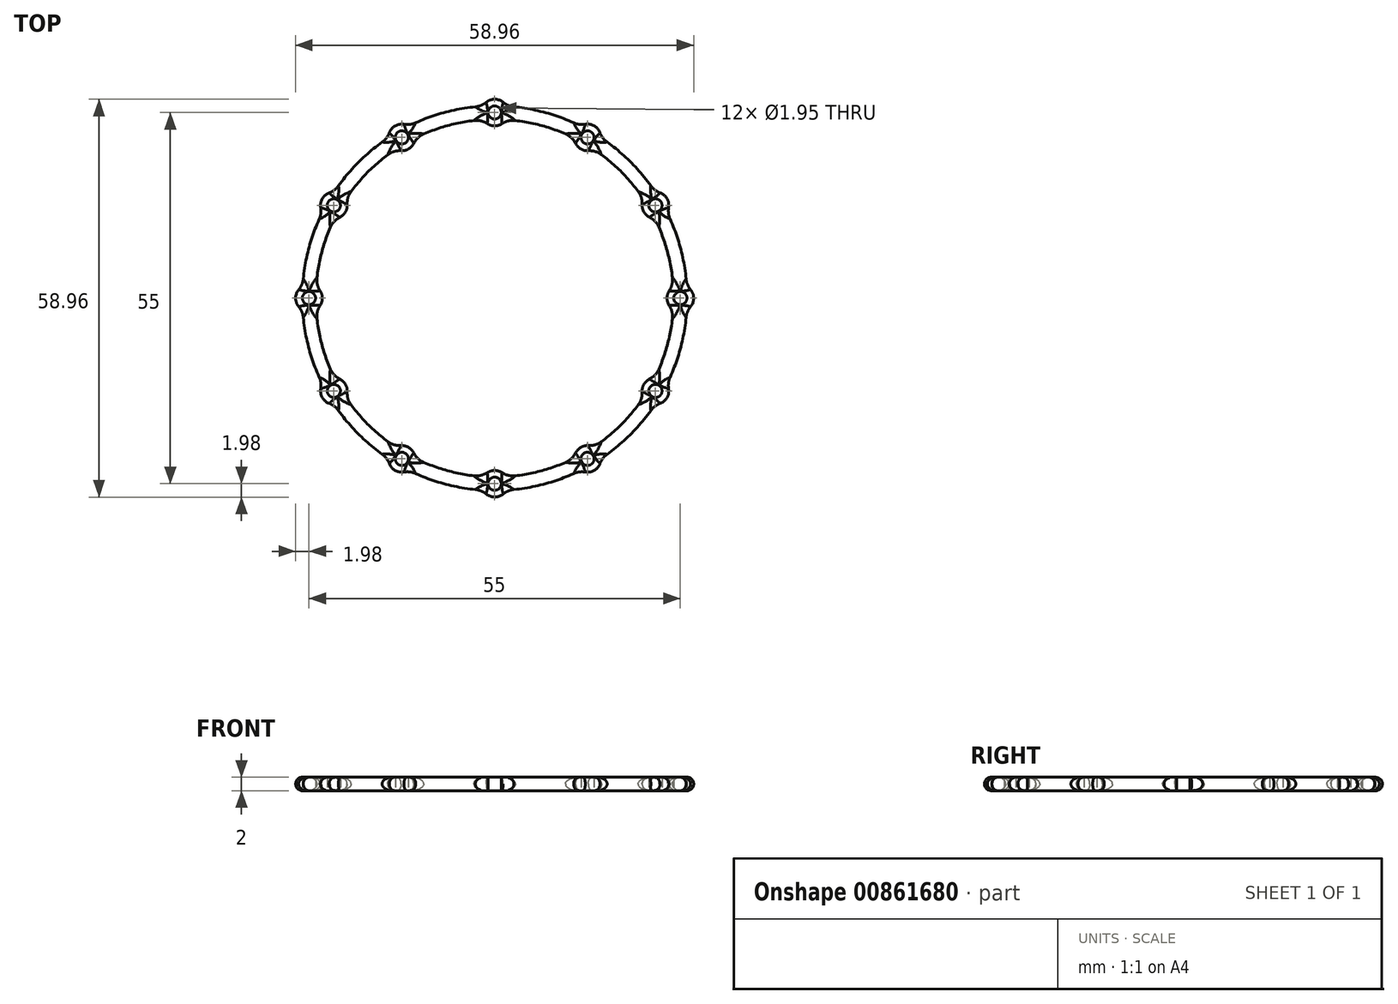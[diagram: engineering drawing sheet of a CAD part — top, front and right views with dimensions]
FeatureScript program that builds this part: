
annotation { "Feature Type Name" : "Feature", "Feature Type Description" : "" }
export const myFeature = defineFeature(function(context is Context, id is Id, definition is map)
    precondition{}
    {
        {
            var Q0;
            Q0=qCreatedBy(makeId("Top.planeOp"),FACE);
            var sketch = newSketch(context, id + "F0", { "sketchPlane" : qUnion([Q0])});
            skCircle(sketch, "E0", {"center": v(0, 0) * mm, "radius": 27.5 * mm});
            skCircle(sketch, "E1", {"center": v(0, 27.5) * mm, "radius": 0.97 * mm});
            skCircle(sketch, "E2.0", {"center": v(0, 27.5) * mm, "radius": 2.98 * mm});
            skCircle(sketch, "E3.0", {"center": v(0, 0) * mm, "radius": 28.5 * mm});
            skCircle(sketch, "E4.0", {"center": v(0, 0) * mm, "radius": 26.5 * mm});
            skCircle(sketch, "E5.0", {"center": v(0, 27.5) * mm, "radius": 1.98 * mm});
            skCircle(sketch, "E6.1.0", {"center": v(13.75, 23.82) * mm, "radius": 2.98 * mm});
            skCircle(sketch, "E6.1.1", {"center": v(13.75, 23.82) * mm, "radius": 1.98 * mm});
            skCircle(sketch, "E6.1.2", {"center": v(13.75, 23.82) * mm, "radius": 0.97 * mm});
            skCircle(sketch, "E6.2.0", {"center": v(23.82, 13.75) * mm, "radius": 2.98 * mm});
            skCircle(sketch, "E6.2.1", {"center": v(23.82, 13.75) * mm, "radius": 1.98 * mm});
            skCircle(sketch, "E6.2.2", {"center": v(23.82, 13.75) * mm, "radius": 0.97 * mm});
            skCircle(sketch, "E6.3.0", {"center": v(27.5, 0) * mm, "radius": 2.98 * mm});
            skCircle(sketch, "E6.3.1", {"center": v(27.5, 0) * mm, "radius": 1.98 * mm});
            skCircle(sketch, "E6.3.2", {"center": v(27.5, 0) * mm, "radius": 0.97 * mm});
            skCircle(sketch, "E6.4.0", {"center": v(23.82, -13.75) * mm, "radius": 2.98 * mm});
            skCircle(sketch, "E6.4.1", {"center": v(23.82, -13.75) * mm, "radius": 1.98 * mm});
            skCircle(sketch, "E6.4.2", {"center": v(23.82, -13.75) * mm, "radius": 0.97 * mm});
            skCircle(sketch, "E6.5.0", {"center": v(13.75, -23.82) * mm, "radius": 2.98 * mm});
            skCircle(sketch, "E6.5.1", {"center": v(13.75, -23.82) * mm, "radius": 1.98 * mm});
            skCircle(sketch, "E6.5.2", {"center": v(13.75, -23.82) * mm, "radius": 0.97 * mm});
            skCircle(sketch, "E6.6.0", {"center": v(0, -27.5) * mm, "radius": 2.98 * mm});
            skCircle(sketch, "E6.6.1", {"center": v(0, -27.5) * mm, "radius": 1.98 * mm});
            skCircle(sketch, "E6.6.2", {"center": v(0, -27.5) * mm, "radius": 0.97 * mm});
            skCircle(sketch, "E6.7.0", {"center": v(-13.75, -23.82) * mm, "radius": 2.98 * mm});
            skCircle(sketch, "E6.7.1", {"center": v(-13.75, -23.82) * mm, "radius": 1.98 * mm});
            skCircle(sketch, "E6.7.2", {"center": v(-13.75, -23.82) * mm, "radius": 0.97 * mm});
            skCircle(sketch, "E6.8.0", {"center": v(-23.82, -13.75) * mm, "radius": 2.98 * mm});
            skCircle(sketch, "E6.8.1", {"center": v(-23.82, -13.75) * mm, "radius": 1.98 * mm});
            skCircle(sketch, "E6.8.2", {"center": v(-23.82, -13.75) * mm, "radius": 0.97 * mm});
            skCircle(sketch, "E6.9.0", {"center": v(-27.5, 0) * mm, "radius": 2.98 * mm});
            skCircle(sketch, "E6.9.1", {"center": v(-27.5, 0) * mm, "radius": 1.98 * mm});
            skCircle(sketch, "E6.9.2", {"center": v(-27.5, 0) * mm, "radius": 0.97 * mm});
            skCircle(sketch, "E6.10.0", {"center": v(-23.82, 13.75) * mm, "radius": 2.98 * mm});
            skCircle(sketch, "E6.10.1", {"center": v(-23.82, 13.75) * mm, "radius": 1.98 * mm});
            skCircle(sketch, "E6.10.2", {"center": v(-23.82, 13.75) * mm, "radius": 0.97 * mm});
            skCircle(sketch, "E6.11.0", {"center": v(-13.75, 23.82) * mm, "radius": 2.98 * mm});
            skCircle(sketch, "E6.11.1", {"center": v(-13.75, 23.82) * mm, "radius": 1.98 * mm});
            skCircle(sketch, "E6.11.2", {"center": v(-13.75, 23.82) * mm, "radius": 0.97 * mm});
            skLineSegment(sketch, "E6.anchor1", {"start": v(0, 0) * mm, "end": v(0, 27.5) * mm, "construction": true});
            skLineSegment(sketch, "E6.anchor2", {"start": v(0, 0) * mm, "end": v(-13.75, 23.82) * mm, "construction": true});
            skSolve(sketch);
        }
        {
            var Q0;
            {var subQ0=sQuery(id+"F0.wireOp",EDGE,"E6.11.0");var subQ1=sQuery(id+"F0.wireOp",EDGE,"E0");var subQ2=makeQuery(id+"F0.imprint","INTERSECT",VERTEX,{"disambiguationData":[OD(1.0)],"derivedFrom":[subQ1,subQ0]});Q0=makeQuery(id+"F0.imprint","IMPRINT",FACE,{"disambiguationData":[TD([[makeQuery(id+"F0.imprint","IMPRINT",EDGE,{"disambiguationData":[TD([[subQ2,-1.0]])],"derivedFrom":subQ1}),-1.0]])]});}
            var Q1;
            {var subQ0=sQuery(id+"F0.wireOp",EDGE,"E6.11.0");var subQ1=sQuery(id+"F0.wireOp",EDGE,"E0");var subQ2=makeQuery(id+"F0.imprint","INTERSECT",VERTEX,{"disambiguationData":[OD(1.0)],"derivedFrom":[subQ1,subQ0]});Q1=makeQuery(id+"F0.imprint","IMPRINT",FACE,{"disambiguationData":[TD([[makeQuery(id+"F0.imprint","IMPRINT",EDGE,{"disambiguationData":[TD([[subQ2,-1.0]])],"derivedFrom":subQ1}),1.0]])]});}
            var Q2;
            {var subQ0=sQuery(id+"F0.wireOp",EDGE,"E6.11.1");var subQ1=sQuery(id+"F0.wireOp",EDGE,"E3.0");var subQ2=makeQuery(id+"F0.imprint","INTERSECT",VERTEX,{"disambiguationData":[OD(0.0)],"derivedFrom":[subQ1,subQ0]});Q2=makeQuery(id+"F0.imprint","IMPRINT",FACE,{"disambiguationData":[TD([[makeQuery(id+"F0.imprint","IMPRINT",EDGE,{"disambiguationData":[TD([[subQ2,-1.0]])],"derivedFrom":subQ1}),-1.0]])]});}
            var Q3;
            {var subQ0=sQuery(id+"F0.wireOp",EDGE,"E6.11.1");var subQ4=sQuery(id+"F0.wireOp",EDGE,"E0");var subQ8=makeQuery(id+"F0.imprint","INTERSECT",VERTEX,{"disambiguationData":[OD(0.0)],"derivedFrom":[subQ4,subQ0]});Q3=makeQuery(id+"F0.imprint","IMPRINT",FACE,{"disambiguationData":[TD([[makeQuery(id+"F0.imprint","IMPRINT",EDGE,{"disambiguationData":[TD([[subQ8,-1.0]])],"derivedFrom":subQ4}),-1.0]])]});}
            var Q4;
            {var subQ0=sQuery(id+"F0.wireOp",EDGE,"E6.11.1");var subQ1=sQuery(id+"F0.wireOp",EDGE,"E0");var subQ6=makeQuery(id+"F0.imprint","INTERSECT",VERTEX,{"disambiguationData":[OD(0.0)],"derivedFrom":[subQ1,subQ0]});Q4=makeQuery(id+"F0.imprint","IMPRINT",FACE,{"disambiguationData":[TD([[makeQuery(id+"F0.imprint","IMPRINT",EDGE,{"disambiguationData":[TD([[subQ6,-1.0]])],"derivedFrom":subQ1}),1.0]])]});}
            var Q5;
            {var subQ0=sQuery(id+"F0.wireOp",EDGE,"E6.11.1");var subQ1=sQuery(id+"F0.wireOp",EDGE,"E4.0");var subQ2=makeQuery(id+"F0.imprint","INTERSECT",VERTEX,{"disambiguationData":[OD(0.0)],"derivedFrom":[subQ1,subQ0]});Q5=makeQuery(id+"F0.imprint","IMPRINT",FACE,{"disambiguationData":[TD([[makeQuery(id+"F0.imprint","IMPRINT",EDGE,{"disambiguationData":[TD([[subQ2,-1.0]])],"derivedFrom":subQ1}),1.0]])]});}
            var Q6;
            {var subQ0=sQuery(id+"F0.wireOp",EDGE,"E6.11.1");var subQ1=sQuery(id+"F0.wireOp",EDGE,"E0");var subQ2=makeQuery(id+"F0.imprint","INTERSECT",VERTEX,{"disambiguationData":[OD(1.0)],"derivedFrom":[subQ1,subQ0]});Q6=makeQuery(id+"F0.imprint","IMPRINT",FACE,{"disambiguationData":[TD([[makeQuery(id+"F0.imprint","IMPRINT",EDGE,{"disambiguationData":[TD([[subQ2,-1.0]])],"derivedFrom":subQ1}),1.0]])]});}
            var Q7;
            {var subQ0=sQuery(id+"F0.wireOp",EDGE,"E6.11.1");var subQ1=sQuery(id+"F0.wireOp",EDGE,"E0");var subQ2=makeQuery(id+"F0.imprint","INTERSECT",VERTEX,{"disambiguationData":[OD(1.0)],"derivedFrom":[subQ1,subQ0]});Q7=makeQuery(id+"F0.imprint","IMPRINT",FACE,{"disambiguationData":[TD([[makeQuery(id+"F0.imprint","IMPRINT",EDGE,{"disambiguationData":[TD([[subQ2,-1.0]])],"derivedFrom":subQ1}),-1.0]])]});}
            var Q8;
            {var subQ0=sQuery(id+"F0.wireOp",EDGE,"E6.11.0");var subQ1=sQuery(id+"F0.wireOp",EDGE,"E0");var subQ2=makeQuery(id+"F0.imprint","INTERSECT",VERTEX,{"disambiguationData":[OD(0.0)],"derivedFrom":[subQ1,subQ0]});Q8=makeQuery(id+"F0.imprint","IMPRINT",FACE,{"disambiguationData":[TD([[makeQuery(id+"F0.imprint","IMPRINT",EDGE,{"disambiguationData":[TD([[subQ2,-1.0]])],"derivedFrom":subQ1}),-1.0]])]});}
            var Q9;
            {var subQ0=sQuery(id+"F0.wireOp",EDGE,"E6.11.0");var subQ1=sQuery(id+"F0.wireOp",EDGE,"E0");var subQ2=makeQuery(id+"F0.imprint","INTERSECT",VERTEX,{"disambiguationData":[OD(0.0)],"derivedFrom":[subQ1,subQ0]});Q9=makeQuery(id+"F0.imprint","IMPRINT",FACE,{"disambiguationData":[TD([[makeQuery(id+"F0.imprint","IMPRINT",EDGE,{"disambiguationData":[TD([[subQ2,-1.0]])],"derivedFrom":subQ1}),1.0]])]});}
            var Q10;
            {var subQ0=sQuery(id+"F0.wireOp",EDGE,"E2.0");var subQ1=sQuery(id+"F0.wireOp",EDGE,"E0");var subQ2=makeQuery(id+"F0.imprint","INTERSECT",VERTEX,{"disambiguationData":[OD(1.0)],"derivedFrom":[subQ1,subQ0]});Q10=makeQuery(id+"F0.imprint","IMPRINT",FACE,{"disambiguationData":[TD([[makeQuery(id+"F0.imprint","IMPRINT",EDGE,{"disambiguationData":[TD([[subQ2,-1.0]])],"derivedFrom":subQ1}),1.0]])]});}
            var Q11;
            {var subQ0=sQuery(id+"F0.wireOp",EDGE,"E2.0");var subQ1=sQuery(id+"F0.wireOp",EDGE,"E0");var subQ2=makeQuery(id+"F0.imprint","INTERSECT",VERTEX,{"disambiguationData":[OD(1.0)],"derivedFrom":[subQ1,subQ0]});Q11=makeQuery(id+"F0.imprint","IMPRINT",FACE,{"disambiguationData":[TD([[makeQuery(id+"F0.imprint","IMPRINT",EDGE,{"disambiguationData":[TD([[subQ2,-1.0]])],"derivedFrom":subQ1}),-1.0]])]});}
            var Q12;
            {var subQ0=sQuery(id+"F0.wireOp",EDGE,"E5.0");var subQ1=sQuery(id+"F0.wireOp",EDGE,"E0");var subQ2=makeQuery(id+"F0.imprint","INTERSECT",VERTEX,{"disambiguationData":[OD(1.0)],"derivedFrom":[subQ1,subQ0]});Q12=makeQuery(id+"F0.imprint","IMPRINT",FACE,{"disambiguationData":[TD([[makeQuery(id+"F0.imprint","IMPRINT",EDGE,{"disambiguationData":[TD([[subQ2,-1.0]])],"derivedFrom":subQ1}),-1.0]])]});}
            var Q13;
            {var subQ0=sQuery(id+"F0.wireOp",EDGE,"E5.0");var subQ1=sQuery(id+"F0.wireOp",EDGE,"E0");var subQ2=makeQuery(id+"F0.imprint","INTERSECT",VERTEX,{"disambiguationData":[OD(1.0)],"derivedFrom":[subQ1,subQ0]});Q13=makeQuery(id+"F0.imprint","IMPRINT",FACE,{"disambiguationData":[TD([[makeQuery(id+"F0.imprint","IMPRINT",EDGE,{"disambiguationData":[TD([[subQ2,-1.0]])],"derivedFrom":subQ1}),1.0]])]});}
            var Q14;
            {var subQ0=sQuery(id+"F0.wireOp",EDGE,"E5.0");var subQ5=sQuery(id+"F0.wireOp",EDGE,"E0");var subQ9=makeQuery(id+"F0.imprint","INTERSECT",VERTEX,{"disambiguationData":[OD(0.0)],"derivedFrom":[subQ5,subQ0]});Q14=makeQuery(id+"F0.imprint","IMPRINT",FACE,{"disambiguationData":[TD([[makeQuery(id+"F0.imprint","IMPRINT",EDGE,{"disambiguationData":[TD([[subQ9,-1.0]])],"derivedFrom":subQ5}),1.0]])]});}
            var Q15;
            {var subQ1=sQuery(id+"F0.wireOp",EDGE,"E0");var subQ4=sQuery(id+"F0.wireOp",EDGE,"E5.0");var subQ9=makeQuery(id+"F0.imprint","INTERSECT",VERTEX,{"disambiguationData":[OD(0.0)],"derivedFrom":[subQ1,subQ4]});Q15=makeQuery(id+"F0.imprint","IMPRINT",FACE,{"disambiguationData":[TD([[makeQuery(id+"F0.imprint","IMPRINT",EDGE,{"disambiguationData":[TD([[subQ9,-1.0]])],"derivedFrom":subQ1}),-1.0]])]});}
            var Q16;
            {var subQ0=sQuery(id+"F0.wireOp",EDGE,"E2.0");var subQ1=sQuery(id+"F0.wireOp",EDGE,"E0");var subQ2=makeQuery(id+"F0.imprint","INTERSECT",VERTEX,{"disambiguationData":[OD(0.0)],"derivedFrom":[subQ1,subQ0]});Q16=makeQuery(id+"F0.imprint","IMPRINT",FACE,{"disambiguationData":[TD([[makeQuery(id+"F0.imprint","IMPRINT",EDGE,{"disambiguationData":[TD([[subQ2,-1.0]])],"derivedFrom":subQ1}),-1.0]])]});}
            var Q17;
            {var subQ0=sQuery(id+"F0.wireOp",EDGE,"E2.0");var subQ1=sQuery(id+"F0.wireOp",EDGE,"E0");var subQ2=makeQuery(id+"F0.imprint","INTERSECT",VERTEX,{"disambiguationData":[OD(0.0)],"derivedFrom":[subQ1,subQ0]});Q17=makeQuery(id+"F0.imprint","IMPRINT",FACE,{"disambiguationData":[TD([[makeQuery(id+"F0.imprint","IMPRINT",EDGE,{"disambiguationData":[TD([[subQ2,-1.0]])],"derivedFrom":subQ1}),1.0]])]});}
            var Q18;
            {var subQ0=sQuery(id+"F0.wireOp",EDGE,"E5.0");var subQ1=sQuery(id+"F0.wireOp",EDGE,"E4.0");var subQ2=makeQuery(id+"F0.imprint","INTERSECT",VERTEX,{"disambiguationData":[OD(0.0)],"derivedFrom":[subQ1,subQ0]});Q18=makeQuery(id+"F0.imprint","IMPRINT",FACE,{"disambiguationData":[TD([[makeQuery(id+"F0.imprint","IMPRINT",EDGE,{"disambiguationData":[TD([[subQ2,-1.0]])],"derivedFrom":subQ1}),1.0]])]});}
            var Q19;
            {var subQ0=sQuery(id+"F0.wireOp",EDGE,"E5.0");var subQ1=sQuery(id+"F0.wireOp",EDGE,"E3.0");var subQ2=makeQuery(id+"F0.imprint","INTERSECT",VERTEX,{"disambiguationData":[OD(0.0)],"derivedFrom":[subQ1,subQ0]});Q19=makeQuery(id+"F0.imprint","IMPRINT",FACE,{"disambiguationData":[TD([[makeQuery(id+"F0.imprint","IMPRINT",EDGE,{"disambiguationData":[TD([[subQ2,-1.0]])],"derivedFrom":subQ1}),-1.0]])]});}
            var Q20;
            {var subQ0=sQuery(id+"F0.wireOp",EDGE,"E6.1.0");var subQ1=sQuery(id+"F0.wireOp",EDGE,"E0");var subQ2=makeQuery(id+"F0.imprint","INTERSECT",VERTEX,{"disambiguationData":[OD(1.0)],"derivedFrom":[subQ1,subQ0]});Q20=makeQuery(id+"F0.imprint","IMPRINT",FACE,{"disambiguationData":[TD([[makeQuery(id+"F0.imprint","IMPRINT",EDGE,{"disambiguationData":[TD([[subQ2,-1.0]])],"derivedFrom":subQ1}),1.0]])]});}
            var Q21;
            {var subQ0=sQuery(id+"F0.wireOp",EDGE,"E6.1.0");var subQ1=sQuery(id+"F0.wireOp",EDGE,"E0");var subQ2=makeQuery(id+"F0.imprint","INTERSECT",VERTEX,{"disambiguationData":[OD(1.0)],"derivedFrom":[subQ1,subQ0]});Q21=makeQuery(id+"F0.imprint","IMPRINT",FACE,{"disambiguationData":[TD([[makeQuery(id+"F0.imprint","IMPRINT",EDGE,{"disambiguationData":[TD([[subQ2,-1.0]])],"derivedFrom":subQ1}),-1.0]])]});}
            var Q22;
            {var subQ0=sQuery(id+"F0.wireOp",EDGE,"E6.1.1");var subQ1=sQuery(id+"F0.wireOp",EDGE,"E0");var subQ2=makeQuery(id+"F0.imprint","INTERSECT",VERTEX,{"disambiguationData":[OD(1.0)],"derivedFrom":[subQ1,subQ0]});Q22=makeQuery(id+"F0.imprint","IMPRINT",FACE,{"disambiguationData":[TD([[makeQuery(id+"F0.imprint","IMPRINT",EDGE,{"disambiguationData":[TD([[subQ2,-1.0]])],"derivedFrom":subQ1}),1.0]])]});}
            var Q23;
            {var subQ0=sQuery(id+"F0.wireOp",EDGE,"E6.1.1");var subQ1=sQuery(id+"F0.wireOp",EDGE,"E0");var subQ2=makeQuery(id+"F0.imprint","INTERSECT",VERTEX,{"disambiguationData":[OD(1.0)],"derivedFrom":[subQ1,subQ0]});Q23=makeQuery(id+"F0.imprint","IMPRINT",FACE,{"disambiguationData":[TD([[makeQuery(id+"F0.imprint","IMPRINT",EDGE,{"disambiguationData":[TD([[subQ2,-1.0]])],"derivedFrom":subQ1}),-1.0]])]});}
            var Q24;
            {var subQ0=sQuery(id+"F0.wireOp",EDGE,"E6.1.1");var subQ1=sQuery(id+"F0.wireOp",EDGE,"E0");var subQ6=makeQuery(id+"F0.imprint","INTERSECT",VERTEX,{"disambiguationData":[OD(0.0)],"derivedFrom":[subQ1,subQ0]});Q24=makeQuery(id+"F0.imprint","IMPRINT",FACE,{"disambiguationData":[TD([[makeQuery(id+"F0.imprint","IMPRINT",EDGE,{"disambiguationData":[TD([[subQ6,-1.0]])],"derivedFrom":subQ1}),-1.0]])]});}
            var Q25;
            {var subQ1=sQuery(id+"F0.wireOp",EDGE,"E0");var subQ3=sQuery(id+"F0.wireOp",EDGE,"E6.1.1");var subQ8=makeQuery(id+"F0.imprint","INTERSECT",VERTEX,{"disambiguationData":[OD(0.0)],"derivedFrom":[subQ1,subQ3]});Q25=makeQuery(id+"F0.imprint","IMPRINT",FACE,{"disambiguationData":[TD([[makeQuery(id+"F0.imprint","IMPRINT",EDGE,{"disambiguationData":[TD([[subQ8,-1.0]])],"derivedFrom":subQ1}),1.0]])]});}
            var Q26;
            {var subQ0=sQuery(id+"F0.wireOp",EDGE,"E6.1.1");var subQ1=sQuery(id+"F0.wireOp",EDGE,"E4.0");var subQ2=makeQuery(id+"F0.imprint","INTERSECT",VERTEX,{"disambiguationData":[OD(0.0)],"derivedFrom":[subQ1,subQ0]});Q26=makeQuery(id+"F0.imprint","IMPRINT",FACE,{"disambiguationData":[TD([[makeQuery(id+"F0.imprint","IMPRINT",EDGE,{"disambiguationData":[TD([[subQ2,-1.0]])],"derivedFrom":subQ1}),1.0]])]});}
            var Q27;
            {var subQ0=sQuery(id+"F0.wireOp",EDGE,"E6.1.1");var subQ1=sQuery(id+"F0.wireOp",EDGE,"E3.0");var subQ2=makeQuery(id+"F0.imprint","INTERSECT",VERTEX,{"disambiguationData":[OD(0.0)],"derivedFrom":[subQ1,subQ0]});Q27=makeQuery(id+"F0.imprint","IMPRINT",FACE,{"disambiguationData":[TD([[makeQuery(id+"F0.imprint","IMPRINT",EDGE,{"disambiguationData":[TD([[subQ2,-1.0]])],"derivedFrom":subQ1}),-1.0]])]});}
            var Q28;
            {var subQ0=sQuery(id+"F0.wireOp",EDGE,"E6.2.0");var subQ1=sQuery(id+"F0.wireOp",EDGE,"E0");var subQ2=makeQuery(id+"F0.imprint","INTERSECT",VERTEX,{"disambiguationData":[OD(1.0)],"derivedFrom":[subQ1,subQ0]});Q28=makeQuery(id+"F0.imprint","IMPRINT",FACE,{"disambiguationData":[TD([[makeQuery(id+"F0.imprint","IMPRINT",EDGE,{"disambiguationData":[TD([[subQ2,-1.0]])],"derivedFrom":subQ1}),1.0]])]});}
            var Q29;
            {var subQ0=sQuery(id+"F0.wireOp",EDGE,"E6.1.0");var subQ1=sQuery(id+"F0.wireOp",EDGE,"E0");var subQ2=makeQuery(id+"F0.imprint","INTERSECT",VERTEX,{"disambiguationData":[OD(0.0)],"derivedFrom":[subQ1,subQ0]});Q29=makeQuery(id+"F0.imprint","IMPRINT",FACE,{"disambiguationData":[TD([[makeQuery(id+"F0.imprint","IMPRINT",EDGE,{"disambiguationData":[TD([[subQ2,-1.0]])],"derivedFrom":subQ1}),-1.0]])]});}
            var Q30;
            {var subQ0=sQuery(id+"F0.wireOp",EDGE,"E6.1.0");var subQ1=sQuery(id+"F0.wireOp",EDGE,"E0");var subQ2=makeQuery(id+"F0.imprint","INTERSECT",VERTEX,{"disambiguationData":[OD(0.0)],"derivedFrom":[subQ1,subQ0]});Q30=makeQuery(id+"F0.imprint","IMPRINT",FACE,{"disambiguationData":[TD([[makeQuery(id+"F0.imprint","IMPRINT",EDGE,{"disambiguationData":[TD([[subQ2,-1.0]])],"derivedFrom":subQ1}),1.0]])]});}
            var Q31;
            {var subQ0=sQuery(id+"F0.wireOp",EDGE,"E6.2.0");var subQ1=sQuery(id+"F0.wireOp",EDGE,"E0");var subQ2=makeQuery(id+"F0.imprint","INTERSECT",VERTEX,{"disambiguationData":[OD(1.0)],"derivedFrom":[subQ1,subQ0]});Q31=makeQuery(id+"F0.imprint","IMPRINT",FACE,{"disambiguationData":[TD([[makeQuery(id+"F0.imprint","IMPRINT",EDGE,{"disambiguationData":[TD([[subQ2,-1.0]])],"derivedFrom":subQ1}),-1.0]])]});}
            var Q32;
            {var subQ0=sQuery(id+"F0.wireOp",EDGE,"E6.2.1");var subQ1=sQuery(id+"F0.wireOp",EDGE,"E0");var subQ2=makeQuery(id+"F0.imprint","INTERSECT",VERTEX,{"disambiguationData":[OD(1.0)],"derivedFrom":[subQ1,subQ0]});Q32=makeQuery(id+"F0.imprint","IMPRINT",FACE,{"disambiguationData":[TD([[makeQuery(id+"F0.imprint","IMPRINT",EDGE,{"disambiguationData":[TD([[subQ2,-1.0]])],"derivedFrom":subQ1}),1.0]])]});}
            var Q33;
            {var subQ0=sQuery(id+"F0.wireOp",EDGE,"E6.2.1");var subQ1=sQuery(id+"F0.wireOp",EDGE,"E0");var subQ2=makeQuery(id+"F0.imprint","INTERSECT",VERTEX,{"disambiguationData":[OD(1.0)],"derivedFrom":[subQ1,subQ0]});Q33=makeQuery(id+"F0.imprint","IMPRINT",FACE,{"disambiguationData":[TD([[makeQuery(id+"F0.imprint","IMPRINT",EDGE,{"disambiguationData":[TD([[subQ2,-1.0]])],"derivedFrom":subQ1}),-1.0]])]});}
            var Q34;
            {var subQ0=sQuery(id+"F0.wireOp",EDGE,"E6.2.1");var subQ5=sQuery(id+"F0.wireOp",EDGE,"E0");var subQ9=makeQuery(id+"F0.imprint","INTERSECT",VERTEX,{"disambiguationData":[OD(0.0)],"derivedFrom":[subQ5,subQ0]});Q34=makeQuery(id+"F0.imprint","IMPRINT",FACE,{"disambiguationData":[TD([[makeQuery(id+"F0.imprint","IMPRINT",EDGE,{"disambiguationData":[TD([[subQ9,-1.0]])],"derivedFrom":subQ5}),1.0]])]});}
            var Q35;
            {var subQ0=sQuery(id+"F0.wireOp",EDGE,"E6.2.1");var subQ1=sQuery(id+"F0.wireOp",EDGE,"E0");var subQ8=makeQuery(id+"F0.imprint","INTERSECT",VERTEX,{"disambiguationData":[OD(0.0)],"derivedFrom":[subQ1,subQ0]});Q35=makeQuery(id+"F0.imprint","IMPRINT",FACE,{"disambiguationData":[TD([[makeQuery(id+"F0.imprint","IMPRINT",EDGE,{"disambiguationData":[TD([[subQ8,-1.0]])],"derivedFrom":subQ1}),-1.0]])]});}
            var Q36;
            {var subQ0=sQuery(id+"F0.wireOp",EDGE,"E6.2.1");var subQ1=sQuery(id+"F0.wireOp",EDGE,"E4.0");var subQ2=makeQuery(id+"F0.imprint","INTERSECT",VERTEX,{"disambiguationData":[OD(0.0)],"derivedFrom":[subQ1,subQ0]});Q36=makeQuery(id+"F0.imprint","IMPRINT",FACE,{"disambiguationData":[TD([[makeQuery(id+"F0.imprint","IMPRINT",EDGE,{"disambiguationData":[TD([[subQ2,-1.0]])],"derivedFrom":subQ1}),1.0]])]});}
            var Q37;
            {var subQ0=sQuery(id+"F0.wireOp",EDGE,"E6.2.1");var subQ1=sQuery(id+"F0.wireOp",EDGE,"E3.0");var subQ2=makeQuery(id+"F0.imprint","INTERSECT",VERTEX,{"disambiguationData":[OD(0.0)],"derivedFrom":[subQ1,subQ0]});Q37=makeQuery(id+"F0.imprint","IMPRINT",FACE,{"disambiguationData":[TD([[makeQuery(id+"F0.imprint","IMPRINT",EDGE,{"disambiguationData":[TD([[subQ2,-1.0]])],"derivedFrom":subQ1}),-1.0]])]});}
            var Q38;
            {var subQ0=sQuery(id+"F0.wireOp",EDGE,"E6.2.0");var subQ1=sQuery(id+"F0.wireOp",EDGE,"E0");var subQ2=makeQuery(id+"F0.imprint","INTERSECT",VERTEX,{"disambiguationData":[OD(0.0)],"derivedFrom":[subQ1,subQ0]});Q38=makeQuery(id+"F0.imprint","IMPRINT",FACE,{"disambiguationData":[TD([[makeQuery(id+"F0.imprint","IMPRINT",EDGE,{"disambiguationData":[TD([[subQ2,-1.0]])],"derivedFrom":subQ1}),1.0]])]});}
            var Q39;
            {var subQ0=sQuery(id+"F0.wireOp",EDGE,"E6.3.0");var subQ1=sQuery(id+"F0.wireOp",EDGE,"E0");var subQ2=makeQuery(id+"F0.imprint","INTERSECT",VERTEX,{"disambiguationData":[OD(0.0)],"derivedFrom":[subQ1,subQ0]});Q39=makeQuery(id+"F0.imprint","IMPRINT",FACE,{"disambiguationData":[TD([[makeQuery(id+"F0.imprint","IMPRINT",EDGE,{"disambiguationData":[TD([[subQ2,-1.0]])],"derivedFrom":subQ1}),-1.0]])]});}
            var Q40;
            {var subQ0=sQuery(id+"F0.wireOp",EDGE,"E6.3.0");var subQ1=sQuery(id+"F0.wireOp",EDGE,"E0");var subQ2=makeQuery(id+"F0.imprint","INTERSECT",VERTEX,{"disambiguationData":[OD(0.0)],"derivedFrom":[subQ1,subQ0]});Q40=makeQuery(id+"F0.imprint","IMPRINT",FACE,{"disambiguationData":[TD([[makeQuery(id+"F0.imprint","IMPRINT",EDGE,{"disambiguationData":[TD([[subQ2,-1.0]])],"derivedFrom":subQ1}),1.0]])]});}
            var Q41;
            {var subQ0=sQuery(id+"F0.wireOp",EDGE,"E6.2.0");var subQ1=sQuery(id+"F0.wireOp",EDGE,"E0");var subQ2=makeQuery(id+"F0.imprint","INTERSECT",VERTEX,{"disambiguationData":[OD(0.0)],"derivedFrom":[subQ1,subQ0]});Q41=makeQuery(id+"F0.imprint","IMPRINT",FACE,{"disambiguationData":[TD([[makeQuery(id+"F0.imprint","IMPRINT",EDGE,{"disambiguationData":[TD([[subQ2,-1.0]])],"derivedFrom":subQ1}),-1.0]])]});}
            var Q42;
            {var subQ0=sQuery(id+"F0.wireOp",EDGE,"E6.3.1");var subQ1=sQuery(id+"F0.wireOp",EDGE,"E4.0");var subQ2=makeQuery(id+"F0.imprint","INTERSECT",VERTEX,{"disambiguationData":[OD(0.0)],"derivedFrom":[subQ1,subQ0]});Q42=makeQuery(id+"F0.imprint","IMPRINT",FACE,{"disambiguationData":[TD([[makeQuery(id+"F0.imprint","IMPRINT",EDGE,{"disambiguationData":[TD([[subQ2,1.0]])],"derivedFrom":subQ1}),1.0]])]});}
            var Q43;
            {var subQ0=sQuery(id+"F0.wireOp",EDGE,"E6.3.1");var subQ1=sQuery(id+"F0.wireOp",EDGE,"E0");var subQ2=makeQuery(id+"F0.imprint","INTERSECT",VERTEX,{"disambiguationData":[OD(0.0)],"derivedFrom":[subQ1,subQ0]});Q43=makeQuery(id+"F0.imprint","IMPRINT",FACE,{"disambiguationData":[TD([[makeQuery(id+"F0.imprint","IMPRINT",EDGE,{"disambiguationData":[TD([[subQ2,1.0]])],"derivedFrom":subQ1}),1.0]])]});}
            var Q44;
            {var subQ0=sQuery(id+"F0.wireOp",EDGE,"E6.3.1");var subQ1=sQuery(id+"F0.wireOp",EDGE,"E0");var subQ2=makeQuery(id+"F0.imprint","INTERSECT",VERTEX,{"disambiguationData":[OD(0.0)],"derivedFrom":[subQ1,subQ0]});Q44=makeQuery(id+"F0.imprint","IMPRINT",FACE,{"disambiguationData":[TD([[makeQuery(id+"F0.imprint","IMPRINT",EDGE,{"disambiguationData":[TD([[subQ2,1.0]])],"derivedFrom":subQ1}),-1.0]])]});}
            var Q45;
            {var subQ0=sQuery(id+"F0.wireOp",EDGE,"E6.3.1");var subQ1=sQuery(id+"F0.wireOp",EDGE,"E0");var subQ2=makeQuery(id+"F0.imprint","INTERSECT",VERTEX,{"disambiguationData":[OD(0.0)],"derivedFrom":[subQ1,subQ0]});Q45=makeQuery(id+"F0.imprint","IMPRINT",FACE,{"disambiguationData":[TD([[makeQuery(id+"F0.imprint","IMPRINT",EDGE,{"disambiguationData":[TD([[subQ2,-1.0]])],"derivedFrom":subQ1}),1.0]])]});}
            var Q46;
            {var subQ0=sQuery(id+"F0.wireOp",EDGE,"E6.3.1");var subQ1=sQuery(id+"F0.wireOp",EDGE,"E0");var subQ2=makeQuery(id+"F0.imprint","INTERSECT",VERTEX,{"disambiguationData":[OD(0.0)],"derivedFrom":[subQ1,subQ0]});Q46=makeQuery(id+"F0.imprint","IMPRINT",FACE,{"disambiguationData":[TD([[makeQuery(id+"F0.imprint","IMPRINT",EDGE,{"disambiguationData":[TD([[subQ2,-1.0]])],"derivedFrom":subQ1}),-1.0]])]});}
            var Q47;
            {var subQ0=sQuery(id+"F0.wireOp",EDGE,"E6.3.0");var subQ1=sQuery(id+"F0.wireOp",EDGE,"E0");var subQ2=makeQuery(id+"F0.imprint","INTERSECT",VERTEX,{"disambiguationData":[OD(1.0)],"derivedFrom":[subQ1,subQ0]});Q47=makeQuery(id+"F0.imprint","IMPRINT",FACE,{"disambiguationData":[TD([[makeQuery(id+"F0.imprint","IMPRINT",EDGE,{"disambiguationData":[TD([[subQ2,-1.0]])],"derivedFrom":subQ1}),-1.0]])]});}
            var Q48;
            {var subQ0=sQuery(id+"F0.wireOp",EDGE,"E6.4.0");var subQ1=sQuery(id+"F0.wireOp",EDGE,"E0");var subQ2=makeQuery(id+"F0.imprint","INTERSECT",VERTEX,{"disambiguationData":[OD(1.0)],"derivedFrom":[subQ1,subQ0]});Q48=makeQuery(id+"F0.imprint","IMPRINT",FACE,{"disambiguationData":[TD([[makeQuery(id+"F0.imprint","IMPRINT",EDGE,{"disambiguationData":[TD([[subQ2,-1.0]])],"derivedFrom":subQ1}),1.0]])]});}
            var Q49;
            {var subQ0=sQuery(id+"F0.wireOp",EDGE,"E6.3.0");var subQ1=sQuery(id+"F0.wireOp",EDGE,"E0");var subQ2=makeQuery(id+"F0.imprint","INTERSECT",VERTEX,{"disambiguationData":[OD(1.0)],"derivedFrom":[subQ1,subQ0]});Q49=makeQuery(id+"F0.imprint","IMPRINT",FACE,{"disambiguationData":[TD([[makeQuery(id+"F0.imprint","IMPRINT",EDGE,{"disambiguationData":[TD([[subQ2,-1.0]])],"derivedFrom":subQ1}),1.0]])]});}
            var Q50;
            {var subQ0=sQuery(id+"F0.wireOp",EDGE,"E6.4.0");var subQ1=sQuery(id+"F0.wireOp",EDGE,"E0");var subQ2=makeQuery(id+"F0.imprint","INTERSECT",VERTEX,{"disambiguationData":[OD(1.0)],"derivedFrom":[subQ1,subQ0]});Q50=makeQuery(id+"F0.imprint","IMPRINT",FACE,{"disambiguationData":[TD([[makeQuery(id+"F0.imprint","IMPRINT",EDGE,{"disambiguationData":[TD([[subQ2,-1.0]])],"derivedFrom":subQ1}),-1.0]])]});}
            var Q51;
            {var subQ0=sQuery(id+"F0.wireOp",EDGE,"E6.5.1");var subQ1=sQuery(id+"F0.wireOp",EDGE,"E4.0");var subQ2=makeQuery(id+"F0.imprint","INTERSECT",VERTEX,{"disambiguationData":[OD(0.0)],"derivedFrom":[subQ1,subQ0]});Q51=makeQuery(id+"F0.imprint","IMPRINT",FACE,{"disambiguationData":[TD([[makeQuery(id+"F0.imprint","IMPRINT",EDGE,{"disambiguationData":[TD([[subQ2,-1.0]])],"derivedFrom":subQ1}),1.0]])]});}
            var Q52;
            {var subQ0=sQuery(id+"F0.wireOp",EDGE,"E6.4.1");var subQ1=sQuery(id+"F0.wireOp",EDGE,"E4.0");var subQ2=makeQuery(id+"F0.imprint","INTERSECT",VERTEX,{"disambiguationData":[OD(0.0)],"derivedFrom":[subQ1,subQ0]});Q52=makeQuery(id+"F0.imprint","IMPRINT",FACE,{"disambiguationData":[TD([[makeQuery(id+"F0.imprint","IMPRINT",EDGE,{"disambiguationData":[TD([[subQ2,-1.0]])],"derivedFrom":subQ1}),1.0]])]});}
            var Q53;
            {var subQ0=sQuery(id+"F0.wireOp",EDGE,"E6.4.1");var subQ1=sQuery(id+"F0.wireOp",EDGE,"E3.0");var subQ2=makeQuery(id+"F0.imprint","INTERSECT",VERTEX,{"disambiguationData":[OD(0.0)],"derivedFrom":[subQ1,subQ0]});Q53=makeQuery(id+"F0.imprint","IMPRINT",FACE,{"disambiguationData":[TD([[makeQuery(id+"F0.imprint","IMPRINT",EDGE,{"disambiguationData":[TD([[subQ2,-1.0]])],"derivedFrom":subQ1}),-1.0]])]});}
            var Q54;
            {var subQ0=sQuery(id+"F0.wireOp",EDGE,"E6.5.1");var subQ1=sQuery(id+"F0.wireOp",EDGE,"E3.0");var subQ2=makeQuery(id+"F0.imprint","INTERSECT",VERTEX,{"disambiguationData":[OD(0.0)],"derivedFrom":[subQ1,subQ0]});Q54=makeQuery(id+"F0.imprint","IMPRINT",FACE,{"disambiguationData":[TD([[makeQuery(id+"F0.imprint","IMPRINT",EDGE,{"disambiguationData":[TD([[subQ2,-1.0]])],"derivedFrom":subQ1}),-1.0]])]});}
            var Q55;
            {var subQ0=sQuery(id+"F0.wireOp",EDGE,"E6.5.1");var subQ5=sQuery(id+"F0.wireOp",EDGE,"E0");var subQ9=makeQuery(id+"F0.imprint","INTERSECT",VERTEX,{"disambiguationData":[OD(0.0)],"derivedFrom":[subQ5,subQ0]});Q55=makeQuery(id+"F0.imprint","IMPRINT",FACE,{"disambiguationData":[TD([[makeQuery(id+"F0.imprint","IMPRINT",EDGE,{"disambiguationData":[TD([[subQ9,-1.0]])],"derivedFrom":subQ5}),-1.0]])]});}
            var Q56;
            {var subQ0=sQuery(id+"F0.wireOp",EDGE,"E6.5.1");var subQ1=sQuery(id+"F0.wireOp",EDGE,"E0");var subQ8=makeQuery(id+"F0.imprint","INTERSECT",VERTEX,{"disambiguationData":[OD(0.0)],"derivedFrom":[subQ1,subQ0]});Q56=makeQuery(id+"F0.imprint","IMPRINT",FACE,{"disambiguationData":[TD([[makeQuery(id+"F0.imprint","IMPRINT",EDGE,{"disambiguationData":[TD([[subQ8,-1.0]])],"derivedFrom":subQ1}),1.0]])]});}
            var Q57;
            {var subQ0=sQuery(id+"F0.wireOp",EDGE,"E6.4.1");var subQ4=sQuery(id+"F0.wireOp",EDGE,"E0");var subQ8=makeQuery(id+"F0.imprint","INTERSECT",VERTEX,{"disambiguationData":[OD(0.0)],"derivedFrom":[subQ4,subQ0]});Q57=makeQuery(id+"F0.imprint","IMPRINT",FACE,{"disambiguationData":[TD([[makeQuery(id+"F0.imprint","IMPRINT",EDGE,{"disambiguationData":[TD([[subQ8,-1.0]])],"derivedFrom":subQ4}),-1.0]])]});}
            var Q58;
            {var subQ0=sQuery(id+"F0.wireOp",EDGE,"E6.4.1");var subQ1=sQuery(id+"F0.wireOp",EDGE,"E0");var subQ8=makeQuery(id+"F0.imprint","INTERSECT",VERTEX,{"disambiguationData":[OD(0.0)],"derivedFrom":[subQ1,subQ0]});Q58=makeQuery(id+"F0.imprint","IMPRINT",FACE,{"disambiguationData":[TD([[makeQuery(id+"F0.imprint","IMPRINT",EDGE,{"disambiguationData":[TD([[subQ8,-1.0]])],"derivedFrom":subQ1}),1.0]])]});}
            var Q59;
            {var subQ0=sQuery(id+"F0.wireOp",EDGE,"E6.5.0");var subQ1=sQuery(id+"F0.wireOp",EDGE,"E0");var subQ2=makeQuery(id+"F0.imprint","INTERSECT",VERTEX,{"disambiguationData":[OD(1.0)],"derivedFrom":[subQ1,subQ0]});Q59=makeQuery(id+"F0.imprint","IMPRINT",FACE,{"disambiguationData":[TD([[makeQuery(id+"F0.imprint","IMPRINT",EDGE,{"disambiguationData":[TD([[subQ2,-1.0]])],"derivedFrom":subQ1}),-1.0]])]});}
            var Q60;
            {var subQ0=sQuery(id+"F0.wireOp",EDGE,"E6.6.0");var subQ1=sQuery(id+"F0.wireOp",EDGE,"E0");var subQ2=makeQuery(id+"F0.imprint","INTERSECT",VERTEX,{"disambiguationData":[OD(1.0)],"derivedFrom":[subQ1,subQ0]});Q60=makeQuery(id+"F0.imprint","IMPRINT",FACE,{"disambiguationData":[TD([[makeQuery(id+"F0.imprint","IMPRINT",EDGE,{"disambiguationData":[TD([[subQ2,-1.0]])],"derivedFrom":subQ1}),-1.0]])]});}
            var Q61;
            {var subQ0=sQuery(id+"F0.wireOp",EDGE,"E6.4.1");var subQ1=sQuery(id+"F0.wireOp",EDGE,"E0");var subQ2=makeQuery(id+"F0.imprint","INTERSECT",VERTEX,{"disambiguationData":[OD(1.0)],"derivedFrom":[subQ1,subQ0]});Q61=makeQuery(id+"F0.imprint","IMPRINT",FACE,{"disambiguationData":[TD([[makeQuery(id+"F0.imprint","IMPRINT",EDGE,{"disambiguationData":[TD([[subQ2,-1.0]])],"derivedFrom":subQ1}),1.0]])]});}
            var Q62;
            {var subQ0=sQuery(id+"F0.wireOp",EDGE,"E6.4.1");var subQ1=sQuery(id+"F0.wireOp",EDGE,"E0");var subQ2=makeQuery(id+"F0.imprint","INTERSECT",VERTEX,{"disambiguationData":[OD(1.0)],"derivedFrom":[subQ1,subQ0]});Q62=makeQuery(id+"F0.imprint","IMPRINT",FACE,{"disambiguationData":[TD([[makeQuery(id+"F0.imprint","IMPRINT",EDGE,{"disambiguationData":[TD([[subQ2,-1.0]])],"derivedFrom":subQ1}),-1.0]])]});}
            var Q63;
            {var subQ0=sQuery(id+"F0.wireOp",EDGE,"E6.4.0");var subQ1=sQuery(id+"F0.wireOp",EDGE,"E0");var subQ2=makeQuery(id+"F0.imprint","INTERSECT",VERTEX,{"disambiguationData":[OD(0.0)],"derivedFrom":[subQ1,subQ0]});Q63=makeQuery(id+"F0.imprint","IMPRINT",FACE,{"disambiguationData":[TD([[makeQuery(id+"F0.imprint","IMPRINT",EDGE,{"disambiguationData":[TD([[subQ2,-1.0]])],"derivedFrom":subQ1}),1.0]])]});}
            var Q64;
            {var subQ0=sQuery(id+"F0.wireOp",EDGE,"E6.4.0");var subQ1=sQuery(id+"F0.wireOp",EDGE,"E0");var subQ2=makeQuery(id+"F0.imprint","INTERSECT",VERTEX,{"disambiguationData":[OD(0.0)],"derivedFrom":[subQ1,subQ0]});Q64=makeQuery(id+"F0.imprint","IMPRINT",FACE,{"disambiguationData":[TD([[makeQuery(id+"F0.imprint","IMPRINT",EDGE,{"disambiguationData":[TD([[subQ2,-1.0]])],"derivedFrom":subQ1}),-1.0]])]});}
            var Q65;
            {var subQ0=sQuery(id+"F0.wireOp",EDGE,"E6.5.0");var subQ1=sQuery(id+"F0.wireOp",EDGE,"E0");var subQ2=makeQuery(id+"F0.imprint","INTERSECT",VERTEX,{"disambiguationData":[OD(1.0)],"derivedFrom":[subQ1,subQ0]});Q65=makeQuery(id+"F0.imprint","IMPRINT",FACE,{"disambiguationData":[TD([[makeQuery(id+"F0.imprint","IMPRINT",EDGE,{"disambiguationData":[TD([[subQ2,-1.0]])],"derivedFrom":subQ1}),1.0]])]});}
            var Q66;
            {var subQ0=sQuery(id+"F0.wireOp",EDGE,"E6.5.1");var subQ1=sQuery(id+"F0.wireOp",EDGE,"E0");var subQ2=makeQuery(id+"F0.imprint","INTERSECT",VERTEX,{"disambiguationData":[OD(1.0)],"derivedFrom":[subQ1,subQ0]});Q66=makeQuery(id+"F0.imprint","IMPRINT",FACE,{"disambiguationData":[TD([[makeQuery(id+"F0.imprint","IMPRINT",EDGE,{"disambiguationData":[TD([[subQ2,-1.0]])],"derivedFrom":subQ1}),1.0]])]});}
            var Q67;
            {var subQ0=sQuery(id+"F0.wireOp",EDGE,"E6.5.1");var subQ1=sQuery(id+"F0.wireOp",EDGE,"E0");var subQ2=makeQuery(id+"F0.imprint","INTERSECT",VERTEX,{"disambiguationData":[OD(1.0)],"derivedFrom":[subQ1,subQ0]});Q67=makeQuery(id+"F0.imprint","IMPRINT",FACE,{"disambiguationData":[TD([[makeQuery(id+"F0.imprint","IMPRINT",EDGE,{"disambiguationData":[TD([[subQ2,-1.0]])],"derivedFrom":subQ1}),-1.0]])]});}
            var Q68;
            {var subQ0=sQuery(id+"F0.wireOp",EDGE,"E6.5.0");var subQ1=sQuery(id+"F0.wireOp",EDGE,"E0");var subQ2=makeQuery(id+"F0.imprint","INTERSECT",VERTEX,{"disambiguationData":[OD(0.0)],"derivedFrom":[subQ1,subQ0]});Q68=makeQuery(id+"F0.imprint","IMPRINT",FACE,{"disambiguationData":[TD([[makeQuery(id+"F0.imprint","IMPRINT",EDGE,{"disambiguationData":[TD([[subQ2,-1.0]])],"derivedFrom":subQ1}),1.0]])]});}
            var Q69;
            {var subQ0=sQuery(id+"F0.wireOp",EDGE,"E6.5.0");var subQ1=sQuery(id+"F0.wireOp",EDGE,"E0");var subQ2=makeQuery(id+"F0.imprint","INTERSECT",VERTEX,{"disambiguationData":[OD(0.0)],"derivedFrom":[subQ1,subQ0]});Q69=makeQuery(id+"F0.imprint","IMPRINT",FACE,{"disambiguationData":[TD([[makeQuery(id+"F0.imprint","IMPRINT",EDGE,{"disambiguationData":[TD([[subQ2,-1.0]])],"derivedFrom":subQ1}),-1.0]])]});}
            var Q70;
            {var subQ0=sQuery(id+"F0.wireOp",EDGE,"E6.6.0");var subQ1=sQuery(id+"F0.wireOp",EDGE,"E0");var subQ2=makeQuery(id+"F0.imprint","INTERSECT",VERTEX,{"disambiguationData":[OD(1.0)],"derivedFrom":[subQ1,subQ0]});Q70=makeQuery(id+"F0.imprint","IMPRINT",FACE,{"disambiguationData":[TD([[makeQuery(id+"F0.imprint","IMPRINT",EDGE,{"disambiguationData":[TD([[subQ2,-1.0]])],"derivedFrom":subQ1}),1.0]])]});}
            var Q71;
            {var subQ0=sQuery(id+"F0.wireOp",EDGE,"E6.10.1");var subQ1=sQuery(id+"F0.wireOp",EDGE,"E4.0");var subQ2=makeQuery(id+"F0.imprint","INTERSECT",VERTEX,{"disambiguationData":[OD(0.0)],"derivedFrom":[subQ1,subQ0]});Q71=makeQuery(id+"F0.imprint","IMPRINT",FACE,{"disambiguationData":[TD([[makeQuery(id+"F0.imprint","IMPRINT",EDGE,{"disambiguationData":[TD([[subQ2,-1.0]])],"derivedFrom":subQ1}),1.0]])]});}
            var Q72;
            {var subQ0=sQuery(id+"F0.wireOp",EDGE,"E6.10.1");var subQ1=sQuery(id+"F0.wireOp",EDGE,"E3.0");var subQ2=makeQuery(id+"F0.imprint","INTERSECT",VERTEX,{"disambiguationData":[OD(0.0)],"derivedFrom":[subQ1,subQ0]});Q72=makeQuery(id+"F0.imprint","IMPRINT",FACE,{"disambiguationData":[TD([[makeQuery(id+"F0.imprint","IMPRINT",EDGE,{"disambiguationData":[TD([[subQ2,-1.0]])],"derivedFrom":subQ1}),-1.0]])]});}
            var Q73;
            {var subQ0=sQuery(id+"F0.wireOp",EDGE,"E6.10.1");var subQ4=sQuery(id+"F0.wireOp",EDGE,"E0");var subQ5=makeQuery(id+"F0.imprint","INTERSECT",VERTEX,{"disambiguationData":[OD(0.0)],"derivedFrom":[subQ4,subQ0]});Q73=makeQuery(id+"F0.imprint","IMPRINT",FACE,{"disambiguationData":[TD([[makeQuery(id+"F0.imprint","IMPRINT",EDGE,{"disambiguationData":[TD([[subQ5,-1.0]])],"derivedFrom":subQ4}),-1.0]])]});}
            var Q74;
            {var subQ0=sQuery(id+"F0.wireOp",EDGE,"E6.10.1");var subQ1=sQuery(id+"F0.wireOp",EDGE,"E0");var subQ8=makeQuery(id+"F0.imprint","INTERSECT",VERTEX,{"disambiguationData":[OD(0.0)],"derivedFrom":[subQ1,subQ0]});Q74=makeQuery(id+"F0.imprint","IMPRINT",FACE,{"disambiguationData":[TD([[makeQuery(id+"F0.imprint","IMPRINT",EDGE,{"disambiguationData":[TD([[subQ8,-1.0]])],"derivedFrom":subQ1}),1.0]])]});}
            var Q75;
            {var subQ0=sQuery(id+"F0.wireOp",EDGE,"E6.10.0");var subQ1=sQuery(id+"F0.wireOp",EDGE,"E0");var subQ2=makeQuery(id+"F0.imprint","INTERSECT",VERTEX,{"disambiguationData":[OD(1.0)],"derivedFrom":[subQ1,subQ0]});Q75=makeQuery(id+"F0.imprint","IMPRINT",FACE,{"disambiguationData":[TD([[makeQuery(id+"F0.imprint","IMPRINT",EDGE,{"disambiguationData":[TD([[subQ2,-1.0]])],"derivedFrom":subQ1}),1.0]])]});}
            var Q76;
            {var subQ0=sQuery(id+"F0.wireOp",EDGE,"E6.10.0");var subQ1=sQuery(id+"F0.wireOp",EDGE,"E0");var subQ2=makeQuery(id+"F0.imprint","INTERSECT",VERTEX,{"disambiguationData":[OD(1.0)],"derivedFrom":[subQ1,subQ0]});Q76=makeQuery(id+"F0.imprint","IMPRINT",FACE,{"disambiguationData":[TD([[makeQuery(id+"F0.imprint","IMPRINT",EDGE,{"disambiguationData":[TD([[subQ2,-1.0]])],"derivedFrom":subQ1}),-1.0]])]});}
            var Q77;
            {var subQ0=sQuery(id+"F0.wireOp",EDGE,"E6.10.0");var subQ1=sQuery(id+"F0.wireOp",EDGE,"E0");var subQ2=makeQuery(id+"F0.imprint","INTERSECT",VERTEX,{"disambiguationData":[OD(0.0)],"derivedFrom":[subQ1,subQ0]});Q77=makeQuery(id+"F0.imprint","IMPRINT",FACE,{"disambiguationData":[TD([[makeQuery(id+"F0.imprint","IMPRINT",EDGE,{"disambiguationData":[TD([[subQ2,-1.0]])],"derivedFrom":subQ1}),-1.0]])]});}
            var Q78;
            {var subQ0=sQuery(id+"F0.wireOp",EDGE,"E6.10.1");var subQ1=sQuery(id+"F0.wireOp",EDGE,"E0");var subQ2=makeQuery(id+"F0.imprint","INTERSECT",VERTEX,{"disambiguationData":[OD(1.0)],"derivedFrom":[subQ1,subQ0]});Q78=makeQuery(id+"F0.imprint","IMPRINT",FACE,{"disambiguationData":[TD([[makeQuery(id+"F0.imprint","IMPRINT",EDGE,{"disambiguationData":[TD([[subQ2,-1.0]])],"derivedFrom":subQ1}),-1.0]])]});}
            var Q79;
            {var subQ0=sQuery(id+"F0.wireOp",EDGE,"E6.10.1");var subQ1=sQuery(id+"F0.wireOp",EDGE,"E0");var subQ2=makeQuery(id+"F0.imprint","INTERSECT",VERTEX,{"disambiguationData":[OD(1.0)],"derivedFrom":[subQ1,subQ0]});Q79=makeQuery(id+"F0.imprint","IMPRINT",FACE,{"disambiguationData":[TD([[makeQuery(id+"F0.imprint","IMPRINT",EDGE,{"disambiguationData":[TD([[subQ2,-1.0]])],"derivedFrom":subQ1}),1.0]])]});}
            var Q80;
            {var subQ0=sQuery(id+"F0.wireOp",EDGE,"E6.10.0");var subQ1=sQuery(id+"F0.wireOp",EDGE,"E0");var subQ2=makeQuery(id+"F0.imprint","INTERSECT",VERTEX,{"disambiguationData":[OD(0.0)],"derivedFrom":[subQ1,subQ0]});Q80=makeQuery(id+"F0.imprint","IMPRINT",FACE,{"disambiguationData":[TD([[makeQuery(id+"F0.imprint","IMPRINT",EDGE,{"disambiguationData":[TD([[subQ2,-1.0]])],"derivedFrom":subQ1}),1.0]])]});}
            var Q81;
            {var subQ0=sQuery(id+"F0.wireOp",EDGE,"E6.3.1");var subQ1=sQuery(id+"F0.wireOp",EDGE,"E3.0");var subQ2=makeQuery(id+"F0.imprint","INTERSECT",VERTEX,{"disambiguationData":[OD(0.0)],"derivedFrom":[subQ1,subQ0]});Q81=makeQuery(id+"F0.imprint","IMPRINT",FACE,{"disambiguationData":[TD([[makeQuery(id+"F0.imprint","IMPRINT",EDGE,{"disambiguationData":[TD([[subQ2,1.0]])],"derivedFrom":subQ1}),-1.0]])]});}
            var Q82;
            {var subQ0=sQuery(id+"F0.wireOp",EDGE,"E6.9.1");var subQ1=sQuery(id+"F0.wireOp",EDGE,"E4.0");var subQ2=makeQuery(id+"F0.imprint","INTERSECT",VERTEX,{"disambiguationData":[OD(0.0)],"derivedFrom":[subQ1,subQ0]});Q82=makeQuery(id+"F0.imprint","IMPRINT",FACE,{"disambiguationData":[TD([[makeQuery(id+"F0.imprint","IMPRINT",EDGE,{"disambiguationData":[TD([[subQ2,-1.0]])],"derivedFrom":subQ1}),1.0]])]});}
            var Q83;
            {var subQ0=sQuery(id+"F0.wireOp",EDGE,"E6.9.1");var subQ4=sQuery(id+"F0.wireOp",EDGE,"E0");var subQ8=makeQuery(id+"F0.imprint","INTERSECT",VERTEX,{"disambiguationData":[OD(0.0)],"derivedFrom":[subQ4,subQ0]});Q83=makeQuery(id+"F0.imprint","IMPRINT",FACE,{"disambiguationData":[TD([[makeQuery(id+"F0.imprint","IMPRINT",EDGE,{"disambiguationData":[TD([[subQ8,-1.0]])],"derivedFrom":subQ4}),-1.0]])]});}
            var Q84;
            {var subQ0=sQuery(id+"F0.wireOp",EDGE,"E6.9.0");var subQ1=sQuery(id+"F0.wireOp",EDGE,"E0");var subQ2=makeQuery(id+"F0.imprint","INTERSECT",VERTEX,{"disambiguationData":[OD(0.0)],"derivedFrom":[subQ1,subQ0]});Q84=makeQuery(id+"F0.imprint","IMPRINT",FACE,{"disambiguationData":[TD([[makeQuery(id+"F0.imprint","IMPRINT",EDGE,{"disambiguationData":[TD([[subQ2,-1.0]])],"derivedFrom":subQ1}),-1.0]])]});}
            var Q85;
            {var subQ0=sQuery(id+"F0.wireOp",EDGE,"E6.9.0");var subQ1=sQuery(id+"F0.wireOp",EDGE,"E0");var subQ2=makeQuery(id+"F0.imprint","INTERSECT",VERTEX,{"disambiguationData":[OD(0.0)],"derivedFrom":[subQ1,subQ0]});Q85=makeQuery(id+"F0.imprint","IMPRINT",FACE,{"disambiguationData":[TD([[makeQuery(id+"F0.imprint","IMPRINT",EDGE,{"disambiguationData":[TD([[subQ2,-1.0]])],"derivedFrom":subQ1}),1.0]])]});}
            var Q86;
            {var subQ0=sQuery(id+"F0.wireOp",EDGE,"E6.9.1");var subQ1=sQuery(id+"F0.wireOp",EDGE,"E0");var subQ8=makeQuery(id+"F0.imprint","INTERSECT",VERTEX,{"disambiguationData":[OD(0.0)],"derivedFrom":[subQ1,subQ0]});Q86=makeQuery(id+"F0.imprint","IMPRINT",FACE,{"disambiguationData":[TD([[makeQuery(id+"F0.imprint","IMPRINT",EDGE,{"disambiguationData":[TD([[subQ8,-1.0]])],"derivedFrom":subQ1}),1.0]])]});}
            var Q87;
            {var subQ0=sQuery(id+"F0.wireOp",EDGE,"E6.9.1");var subQ1=sQuery(id+"F0.wireOp",EDGE,"E0");var subQ2=makeQuery(id+"F0.imprint","INTERSECT",VERTEX,{"disambiguationData":[OD(1.0)],"derivedFrom":[subQ1,subQ0]});Q87=makeQuery(id+"F0.imprint","IMPRINT",FACE,{"disambiguationData":[TD([[makeQuery(id+"F0.imprint","IMPRINT",EDGE,{"disambiguationData":[TD([[subQ2,-1.0]])],"derivedFrom":subQ1}),1.0]])]});}
            var Q88;
            {var subQ0=sQuery(id+"F0.wireOp",EDGE,"E6.9.1");var subQ1=sQuery(id+"F0.wireOp",EDGE,"E0");var subQ2=makeQuery(id+"F0.imprint","INTERSECT",VERTEX,{"disambiguationData":[OD(1.0)],"derivedFrom":[subQ1,subQ0]});Q88=makeQuery(id+"F0.imprint","IMPRINT",FACE,{"disambiguationData":[TD([[makeQuery(id+"F0.imprint","IMPRINT",EDGE,{"disambiguationData":[TD([[subQ2,-1.0]])],"derivedFrom":subQ1}),-1.0]])]});}
            var Q89;
            {var subQ0=sQuery(id+"F0.wireOp",EDGE,"E6.9.0");var subQ1=sQuery(id+"F0.wireOp",EDGE,"E0");var subQ2=makeQuery(id+"F0.imprint","INTERSECT",VERTEX,{"disambiguationData":[OD(1.0)],"derivedFrom":[subQ1,subQ0]});Q89=makeQuery(id+"F0.imprint","IMPRINT",FACE,{"disambiguationData":[TD([[makeQuery(id+"F0.imprint","IMPRINT",EDGE,{"disambiguationData":[TD([[subQ2,-1.0]])],"derivedFrom":subQ1}),-1.0]])]});}
            var Q90;
            {var subQ0=sQuery(id+"F0.wireOp",EDGE,"E6.9.0");var subQ1=sQuery(id+"F0.wireOp",EDGE,"E0");var subQ2=makeQuery(id+"F0.imprint","INTERSECT",VERTEX,{"disambiguationData":[OD(1.0)],"derivedFrom":[subQ1,subQ0]});Q90=makeQuery(id+"F0.imprint","IMPRINT",FACE,{"disambiguationData":[TD([[makeQuery(id+"F0.imprint","IMPRINT",EDGE,{"disambiguationData":[TD([[subQ2,-1.0]])],"derivedFrom":subQ1}),1.0]])]});}
            var Q91;
            {var subQ0=sQuery(id+"F0.wireOp",EDGE,"E6.8.0");var subQ1=sQuery(id+"F0.wireOp",EDGE,"E0");var subQ2=makeQuery(id+"F0.imprint","INTERSECT",VERTEX,{"disambiguationData":[OD(0.0)],"derivedFrom":[subQ1,subQ0]});Q91=makeQuery(id+"F0.imprint","IMPRINT",FACE,{"disambiguationData":[TD([[makeQuery(id+"F0.imprint","IMPRINT",EDGE,{"disambiguationData":[TD([[subQ2,-1.0]])],"derivedFrom":subQ1}),-1.0]])]});}
            var Q92;
            {var subQ0=sQuery(id+"F0.wireOp",EDGE,"E6.8.0");var subQ1=sQuery(id+"F0.wireOp",EDGE,"E0");var subQ2=makeQuery(id+"F0.imprint","INTERSECT",VERTEX,{"disambiguationData":[OD(0.0)],"derivedFrom":[subQ1,subQ0]});Q92=makeQuery(id+"F0.imprint","IMPRINT",FACE,{"disambiguationData":[TD([[makeQuery(id+"F0.imprint","IMPRINT",EDGE,{"disambiguationData":[TD([[subQ2,-1.0]])],"derivedFrom":subQ1}),1.0]])]});}
            var Q93;
            {var subQ0=sQuery(id+"F0.wireOp",EDGE,"E6.8.1");var subQ1=sQuery(id+"F0.wireOp",EDGE,"E0");var subQ8=makeQuery(id+"F0.imprint","INTERSECT",VERTEX,{"disambiguationData":[OD(0.0)],"derivedFrom":[subQ1,subQ0]});Q93=makeQuery(id+"F0.imprint","IMPRINT",FACE,{"disambiguationData":[TD([[makeQuery(id+"F0.imprint","IMPRINT",EDGE,{"disambiguationData":[TD([[subQ8,-1.0]])],"derivedFrom":subQ1}),-1.0]])]});}
            var Q94;
            {var subQ0=sQuery(id+"F0.wireOp",EDGE,"E6.8.1");var subQ1=sQuery(id+"F0.wireOp",EDGE,"E0");var subQ2=makeQuery(id+"F0.imprint","INTERSECT",VERTEX,{"disambiguationData":[OD(1.0)],"derivedFrom":[subQ1,subQ0]});Q94=makeQuery(id+"F0.imprint","IMPRINT",FACE,{"disambiguationData":[TD([[makeQuery(id+"F0.imprint","IMPRINT",EDGE,{"disambiguationData":[TD([[subQ2,-1.0]])],"derivedFrom":subQ1}),-1.0]])]});}
            var Q95;
            {var subQ0=sQuery(id+"F0.wireOp",EDGE,"E6.8.1");var subQ1=sQuery(id+"F0.wireOp",EDGE,"E0");var subQ2=makeQuery(id+"F0.imprint","INTERSECT",VERTEX,{"disambiguationData":[OD(1.0)],"derivedFrom":[subQ1,subQ0]});Q95=makeQuery(id+"F0.imprint","IMPRINT",FACE,{"disambiguationData":[TD([[makeQuery(id+"F0.imprint","IMPRINT",EDGE,{"disambiguationData":[TD([[subQ2,-1.0]])],"derivedFrom":subQ1}),1.0]])]});}
            var Q96;
            {var subQ0=sQuery(id+"F0.wireOp",EDGE,"E6.8.1");var subQ1=sQuery(id+"F0.wireOp",EDGE,"E0");var subQ8=makeQuery(id+"F0.imprint","INTERSECT",VERTEX,{"disambiguationData":[OD(0.0)],"derivedFrom":[subQ1,subQ0]});Q96=makeQuery(id+"F0.imprint","IMPRINT",FACE,{"disambiguationData":[TD([[makeQuery(id+"F0.imprint","IMPRINT",EDGE,{"disambiguationData":[TD([[subQ8,-1.0]])],"derivedFrom":subQ1}),1.0]])]});}
            var Q97;
            {var subQ0=sQuery(id+"F0.wireOp",EDGE,"E6.9.1");var subQ1=sQuery(id+"F0.wireOp",EDGE,"E3.0");var subQ2=makeQuery(id+"F0.imprint","INTERSECT",VERTEX,{"disambiguationData":[OD(0.0)],"derivedFrom":[subQ1,subQ0]});Q97=makeQuery(id+"F0.imprint","IMPRINT",FACE,{"disambiguationData":[TD([[makeQuery(id+"F0.imprint","IMPRINT",EDGE,{"disambiguationData":[TD([[subQ2,-1.0]])],"derivedFrom":subQ1}),-1.0]])]});}
            var Q98;
            {var subQ0=sQuery(id+"F0.wireOp",EDGE,"E6.8.1");var subQ1=sQuery(id+"F0.wireOp",EDGE,"E3.0");var subQ2=makeQuery(id+"F0.imprint","INTERSECT",VERTEX,{"disambiguationData":[OD(0.0)],"derivedFrom":[subQ1,subQ0]});Q98=makeQuery(id+"F0.imprint","IMPRINT",FACE,{"disambiguationData":[TD([[makeQuery(id+"F0.imprint","IMPRINT",EDGE,{"disambiguationData":[TD([[subQ2,-1.0]])],"derivedFrom":subQ1}),-1.0]])]});}
            var Q99;
            {var subQ0=sQuery(id+"F0.wireOp",EDGE,"E6.8.1");var subQ1=sQuery(id+"F0.wireOp",EDGE,"E4.0");var subQ2=makeQuery(id+"F0.imprint","INTERSECT",VERTEX,{"disambiguationData":[OD(0.0)],"derivedFrom":[subQ1,subQ0]});Q99=makeQuery(id+"F0.imprint","IMPRINT",FACE,{"disambiguationData":[TD([[makeQuery(id+"F0.imprint","IMPRINT",EDGE,{"disambiguationData":[TD([[subQ2,-1.0]])],"derivedFrom":subQ1}),1.0]])]});}
            var Q100;
            {var subQ0=sQuery(id+"F0.wireOp",EDGE,"E6.7.1");var subQ1=sQuery(id+"F0.wireOp",EDGE,"E3.0");var subQ2=makeQuery(id+"F0.imprint","INTERSECT",VERTEX,{"disambiguationData":[OD(0.0)],"derivedFrom":[subQ1,subQ0]});Q100=makeQuery(id+"F0.imprint","IMPRINT",FACE,{"disambiguationData":[TD([[makeQuery(id+"F0.imprint","IMPRINT",EDGE,{"disambiguationData":[TD([[subQ2,-1.0]])],"derivedFrom":subQ1}),-1.0]])]});}
            var Q101;
            {var subQ0=sQuery(id+"F0.wireOp",EDGE,"E6.7.1");var subQ1=sQuery(id+"F0.wireOp",EDGE,"E4.0");var subQ2=makeQuery(id+"F0.imprint","INTERSECT",VERTEX,{"disambiguationData":[OD(0.0)],"derivedFrom":[subQ1,subQ0]});Q101=makeQuery(id+"F0.imprint","IMPRINT",FACE,{"disambiguationData":[TD([[makeQuery(id+"F0.imprint","IMPRINT",EDGE,{"disambiguationData":[TD([[subQ2,-1.0]])],"derivedFrom":subQ1}),1.0]])]});}
            var Q102;
            {var subQ0=sQuery(id+"F0.wireOp",EDGE,"E6.7.1");var subQ1=sQuery(id+"F0.wireOp",EDGE,"E0");var subQ9=makeQuery(id+"F0.imprint","INTERSECT",VERTEX,{"disambiguationData":[OD(0.0)],"derivedFrom":[subQ1,subQ0]});Q102=makeQuery(id+"F0.imprint","IMPRINT",FACE,{"disambiguationData":[TD([[makeQuery(id+"F0.imprint","IMPRINT",EDGE,{"disambiguationData":[TD([[subQ9,-1.0]])],"derivedFrom":subQ1}),-1.0]])]});}
            var Q103;
            {var subQ0=sQuery(id+"F0.wireOp",EDGE,"E6.7.1");var subQ1=sQuery(id+"F0.wireOp",EDGE,"E0");var subQ8=makeQuery(id+"F0.imprint","INTERSECT",VERTEX,{"disambiguationData":[OD(0.0)],"derivedFrom":[subQ1,subQ0]});Q103=makeQuery(id+"F0.imprint","IMPRINT",FACE,{"disambiguationData":[TD([[makeQuery(id+"F0.imprint","IMPRINT",EDGE,{"disambiguationData":[TD([[subQ8,-1.0]])],"derivedFrom":subQ1}),1.0]])]});}
            var Q104;
            {var subQ0=sQuery(id+"F0.wireOp",EDGE,"E6.8.0");var subQ1=sQuery(id+"F0.wireOp",EDGE,"E0");var subQ2=makeQuery(id+"F0.imprint","INTERSECT",VERTEX,{"disambiguationData":[OD(1.0)],"derivedFrom":[subQ1,subQ0]});Q104=makeQuery(id+"F0.imprint","IMPRINT",FACE,{"disambiguationData":[TD([[makeQuery(id+"F0.imprint","IMPRINT",EDGE,{"disambiguationData":[TD([[subQ2,-1.0]])],"derivedFrom":subQ1}),-1.0]])]});}
            var Q105;
            {var subQ0=sQuery(id+"F0.wireOp",EDGE,"E6.8.0");var subQ1=sQuery(id+"F0.wireOp",EDGE,"E0");var subQ2=makeQuery(id+"F0.imprint","INTERSECT",VERTEX,{"disambiguationData":[OD(1.0)],"derivedFrom":[subQ1,subQ0]});Q105=makeQuery(id+"F0.imprint","IMPRINT",FACE,{"disambiguationData":[TD([[makeQuery(id+"F0.imprint","IMPRINT",EDGE,{"disambiguationData":[TD([[subQ2,-1.0]])],"derivedFrom":subQ1}),1.0]])]});}
            var Q106;
            {var subQ0=sQuery(id+"F0.wireOp",EDGE,"E6.7.0");var subQ1=sQuery(id+"F0.wireOp",EDGE,"E0");var subQ2=makeQuery(id+"F0.imprint","INTERSECT",VERTEX,{"disambiguationData":[OD(1.0)],"derivedFrom":[subQ1,subQ0]});Q106=makeQuery(id+"F0.imprint","IMPRINT",FACE,{"disambiguationData":[TD([[makeQuery(id+"F0.imprint","IMPRINT",EDGE,{"disambiguationData":[TD([[subQ2,-1.0]])],"derivedFrom":subQ1}),-1.0]])]});}
            var Q107;
            {var subQ0=sQuery(id+"F0.wireOp",EDGE,"E6.7.0");var subQ1=sQuery(id+"F0.wireOp",EDGE,"E0");var subQ2=makeQuery(id+"F0.imprint","INTERSECT",VERTEX,{"disambiguationData":[OD(1.0)],"derivedFrom":[subQ1,subQ0]});Q107=makeQuery(id+"F0.imprint","IMPRINT",FACE,{"disambiguationData":[TD([[makeQuery(id+"F0.imprint","IMPRINT",EDGE,{"disambiguationData":[TD([[subQ2,-1.0]])],"derivedFrom":subQ1}),1.0]])]});}
            var Q108;
            {var subQ0=sQuery(id+"F0.wireOp",EDGE,"E6.6.0");var subQ1=sQuery(id+"F0.wireOp",EDGE,"E0");var subQ2=makeQuery(id+"F0.imprint","INTERSECT",VERTEX,{"disambiguationData":[OD(0.0)],"derivedFrom":[subQ1,subQ0]});Q108=makeQuery(id+"F0.imprint","IMPRINT",FACE,{"disambiguationData":[TD([[makeQuery(id+"F0.imprint","IMPRINT",EDGE,{"disambiguationData":[TD([[subQ2,-1.0]])],"derivedFrom":subQ1}),-1.0]])]});}
            var Q109;
            {var subQ0=sQuery(id+"F0.wireOp",EDGE,"E6.6.0");var subQ1=sQuery(id+"F0.wireOp",EDGE,"E0");var subQ2=makeQuery(id+"F0.imprint","INTERSECT",VERTEX,{"disambiguationData":[OD(0.0)],"derivedFrom":[subQ1,subQ0]});Q109=makeQuery(id+"F0.imprint","IMPRINT",FACE,{"disambiguationData":[TD([[makeQuery(id+"F0.imprint","IMPRINT",EDGE,{"disambiguationData":[TD([[subQ2,-1.0]])],"derivedFrom":subQ1}),1.0]])]});}
            var Q110;
            {var subQ0=sQuery(id+"F0.wireOp",EDGE,"E6.6.1");var subQ1=sQuery(id+"F0.wireOp",EDGE,"E0");var subQ6=makeQuery(id+"F0.imprint","INTERSECT",VERTEX,{"disambiguationData":[OD(0.0)],"derivedFrom":[subQ1,subQ0]});Q110=makeQuery(id+"F0.imprint","IMPRINT",FACE,{"disambiguationData":[TD([[makeQuery(id+"F0.imprint","IMPRINT",EDGE,{"disambiguationData":[TD([[subQ6,-1.0]])],"derivedFrom":subQ1}),1.0]])]});}
            var Q111;
            {var subQ0=sQuery(id+"F0.wireOp",EDGE,"E6.6.1");var subQ1=sQuery(id+"F0.wireOp",EDGE,"E3.0");var subQ2=makeQuery(id+"F0.imprint","INTERSECT",VERTEX,{"disambiguationData":[OD(0.0)],"derivedFrom":[subQ1,subQ0]});Q111=makeQuery(id+"F0.imprint","IMPRINT",FACE,{"disambiguationData":[TD([[makeQuery(id+"F0.imprint","IMPRINT",EDGE,{"disambiguationData":[TD([[subQ2,-1.0]])],"derivedFrom":subQ1}),-1.0]])]});}
            var Q112;
            {var subQ0=sQuery(id+"F0.wireOp",EDGE,"E6.6.1");var subQ1=sQuery(id+"F0.wireOp",EDGE,"E0");var subQ2=makeQuery(id+"F0.imprint","INTERSECT",VERTEX,{"disambiguationData":[OD(1.0)],"derivedFrom":[subQ1,subQ0]});Q112=makeQuery(id+"F0.imprint","IMPRINT",FACE,{"disambiguationData":[TD([[makeQuery(id+"F0.imprint","IMPRINT",EDGE,{"disambiguationData":[TD([[subQ2,-1.0]])],"derivedFrom":subQ1}),-1.0]])]});}
            var Q113;
            {var subQ0=sQuery(id+"F0.wireOp",EDGE,"E6.6.1");var subQ1=sQuery(id+"F0.wireOp",EDGE,"E0");var subQ2=makeQuery(id+"F0.imprint","INTERSECT",VERTEX,{"disambiguationData":[OD(1.0)],"derivedFrom":[subQ1,subQ0]});Q113=makeQuery(id+"F0.imprint","IMPRINT",FACE,{"disambiguationData":[TD([[makeQuery(id+"F0.imprint","IMPRINT",EDGE,{"disambiguationData":[TD([[subQ2,-1.0]])],"derivedFrom":subQ1}),1.0]])]});}
            var Q114;
            {var subQ0=sQuery(id+"F0.wireOp",EDGE,"E6.7.1");var subQ1=sQuery(id+"F0.wireOp",EDGE,"E0");var subQ2=makeQuery(id+"F0.imprint","INTERSECT",VERTEX,{"disambiguationData":[OD(1.0)],"derivedFrom":[subQ1,subQ0]});Q114=makeQuery(id+"F0.imprint","IMPRINT",FACE,{"disambiguationData":[TD([[makeQuery(id+"F0.imprint","IMPRINT",EDGE,{"disambiguationData":[TD([[subQ2,-1.0]])],"derivedFrom":subQ1}),-1.0]])]});}
            var Q115;
            {var subQ0=sQuery(id+"F0.wireOp",EDGE,"E6.7.1");var subQ1=sQuery(id+"F0.wireOp",EDGE,"E0");var subQ2=makeQuery(id+"F0.imprint","INTERSECT",VERTEX,{"disambiguationData":[OD(1.0)],"derivedFrom":[subQ1,subQ0]});Q115=makeQuery(id+"F0.imprint","IMPRINT",FACE,{"disambiguationData":[TD([[makeQuery(id+"F0.imprint","IMPRINT",EDGE,{"disambiguationData":[TD([[subQ2,-1.0]])],"derivedFrom":subQ1}),1.0]])]});}
            var Q116;
            {var subQ0=sQuery(id+"F0.wireOp",EDGE,"E6.7.0");var subQ1=sQuery(id+"F0.wireOp",EDGE,"E0");var subQ2=makeQuery(id+"F0.imprint","INTERSECT",VERTEX,{"disambiguationData":[OD(0.0)],"derivedFrom":[subQ1,subQ0]});Q116=makeQuery(id+"F0.imprint","IMPRINT",FACE,{"disambiguationData":[TD([[makeQuery(id+"F0.imprint","IMPRINT",EDGE,{"disambiguationData":[TD([[subQ2,-1.0]])],"derivedFrom":subQ1}),-1.0]])]});}
            var Q117;
            {var subQ0=sQuery(id+"F0.wireOp",EDGE,"E6.7.0");var subQ1=sQuery(id+"F0.wireOp",EDGE,"E0");var subQ2=makeQuery(id+"F0.imprint","INTERSECT",VERTEX,{"disambiguationData":[OD(0.0)],"derivedFrom":[subQ1,subQ0]});Q117=makeQuery(id+"F0.imprint","IMPRINT",FACE,{"disambiguationData":[TD([[makeQuery(id+"F0.imprint","IMPRINT",EDGE,{"disambiguationData":[TD([[subQ2,-1.0]])],"derivedFrom":subQ1}),1.0]])]});}
            var Q118;
            {var subQ0=sQuery(id+"F0.wireOp",EDGE,"E6.6.1");var subQ1=sQuery(id+"F0.wireOp",EDGE,"E4.0");var subQ2=makeQuery(id+"F0.imprint","INTERSECT",VERTEX,{"disambiguationData":[OD(0.0)],"derivedFrom":[subQ1,subQ0]});Q118=makeQuery(id+"F0.imprint","IMPRINT",FACE,{"disambiguationData":[TD([[makeQuery(id+"F0.imprint","IMPRINT",EDGE,{"disambiguationData":[TD([[subQ2,-1.0]])],"derivedFrom":subQ1}),1.0]])]});}
            var Q119;
            {var subQ0=sQuery(id+"F0.wireOp",EDGE,"E6.6.1");var subQ4=sQuery(id+"F0.wireOp",EDGE,"E0");var subQ8=makeQuery(id+"F0.imprint","INTERSECT",VERTEX,{"disambiguationData":[OD(0.0)],"derivedFrom":[subQ4,subQ0]});Q119=makeQuery(id+"F0.imprint","IMPRINT",FACE,{"disambiguationData":[TD([[makeQuery(id+"F0.imprint","IMPRINT",EDGE,{"disambiguationData":[TD([[subQ8,-1.0]])],"derivedFrom":subQ4}),-1.0]])]});}
            extrude(context, id + "F1", {"entities" : qUnion([Q0, Q1, Q2, Q3, Q4, Q5, Q6, Q7, Q8, Q9, Q10, Q11, Q12, Q13, Q14, Q15, Q16, Q17, Q18, Q19, Q20, Q21, Q22, Q23, Q24, Q25, Q26, Q27, Q28, Q29, Q30, Q31, Q32, Q33, Q34, Q35, Q36, Q37, Q38, Q39, Q40, Q41, Q42, Q43, Q44, Q45, Q46, Q47, Q48, Q49, Q50, Q51, Q52, Q53, Q54, Q55, Q56, Q57, Q58, Q59, Q60, Q61, Q62, Q63, Q64, Q65, Q66, Q67, Q68, Q69, Q70, Q71, Q72, Q73, Q74, Q75, Q76, Q77, Q78, Q79, Q80, Q81, Q82, Q83, Q84, Q85, Q86, Q87, Q88, Q89, Q90, Q91, Q92, Q93, Q94, Q95, Q96, Q97, Q98, Q99, Q100, Q101, Q102, Q103, Q104, Q105, Q106, Q107, Q108, Q109, Q110, Q111, Q112, Q113, Q114, Q115, Q116, Q117, Q118, Q119]), "depth" : 2 * mm, "offsetDistance" : 25 * mm});
        }
        {
            var Q0;
            {var subQ0=sQuery(id+"F0.wireOp",EDGE,"E4.0");var subQ1=makeQuery(id+"F0.imprint","INTERSECT",VERTEX,{"disambiguationData":[OD(0.0)],"derivedFrom":[subQ0,sQuery(id+"F0.wireOp",EDGE,"E6.11.0")]});var subQ2=makeQuery(id+"F0.imprint","INTERSECT",VERTEX,{"disambiguationData":[OD(0.0)],"derivedFrom":[sQuery(id+"F0.wireOp",EDGE,"E2.0"),subQ0]});Q0=makeQuery(id+"F1.opExtrude","CAP_EDGE",EDGE,{"disambiguationData":[OSD([subQ0]),TDD([makeQuery(id+"F0.imprint","IMPRINT",EDGE,{"disambiguationData":[TD([[subQ2,1.0]])],"derivedFrom":subQ0}),makeQuery(id+"F0.imprint","IMPRINT",EDGE,{"disambiguationData":[TD([[subQ2,-1.0]])],"derivedFrom":subQ0}),makeQuery(id+"F0.imprint","IMPRINT",EDGE,{"disambiguationData":[TD([[subQ1,-1.0]])],"derivedFrom":subQ0})])],"isStart":false});}
            var Q1;
            {var subQ0=sQuery(id+"F0.wireOp",EDGE,"E4.0");var subQ1=makeQuery(id+"F0.imprint","INTERSECT",VERTEX,{"disambiguationData":[OD(1.0)],"derivedFrom":[sQuery(id+"F0.wireOp",EDGE,"E2.0"),subQ0]});Q1=makeQuery(id+"F1.opExtrude","CAP_EDGE",EDGE,{"disambiguationData":[OSD([subQ0]),TDD([makeQuery(id+"F0.imprint","IMPRINT",EDGE,{"disambiguationData":[TD([[makeQuery(id+"F0.imprint","INTERSECT",VERTEX,{"disambiguationData":[OD(1.0)],"derivedFrom":[subQ0,sQuery(id+"F0.wireOp",EDGE,"E6.1.1")]}),-1.0]])],"derivedFrom":subQ0}),makeQuery(id+"F0.imprint","IMPRINT",EDGE,{"disambiguationData":[TD([[subQ1,1.0]])],"derivedFrom":subQ0}),makeQuery(id+"F0.imprint","IMPRINT",EDGE,{"disambiguationData":[TD([[subQ1,-1.0]])],"derivedFrom":subQ0})])],"isStart":false});}
            var Q2;
            {var subQ0=sQuery(id+"F0.wireOp",EDGE,"E4.0");var subQ1=makeQuery(id+"F0.imprint","INTERSECT",VERTEX,{"disambiguationData":[OD(0.0)],"derivedFrom":[subQ0,sQuery(id+"F0.wireOp",EDGE,"E6.1.0")]});var subQ2=makeQuery(id+"F0.imprint","INTERSECT",VERTEX,{"disambiguationData":[OD(1.0)],"derivedFrom":[subQ0,sQuery(id+"F0.wireOp",EDGE,"E6.2.0")]});Q2=makeQuery(id+"F1.opExtrude","CAP_EDGE",EDGE,{"disambiguationData":[OSD([subQ0]),TDD([makeQuery(id+"F0.imprint","IMPRINT",EDGE,{"disambiguationData":[TD([[makeQuery(id+"F0.imprint","INTERSECT",VERTEX,{"disambiguationData":[OD(1.0)],"derivedFrom":[subQ0,sQuery(id+"F0.wireOp",EDGE,"E6.2.1")]}),-1.0]])],"derivedFrom":subQ0}),makeQuery(id+"F0.imprint","IMPRINT",EDGE,{"disambiguationData":[TD([[subQ2,-1.0]])],"derivedFrom":subQ0}),makeQuery(id+"F0.imprint","IMPRINT",EDGE,{"disambiguationData":[TD([[subQ1,-1.0]])],"derivedFrom":subQ0})])],"isStart":false});}
            var Q3;
            {var subQ0=sQuery(id+"F0.wireOp",EDGE,"E4.0");var subQ1=makeQuery(id+"F0.imprint","INTERSECT",VERTEX,{"disambiguationData":[OD(0.0)],"derivedFrom":[subQ0,sQuery(id+"F0.wireOp",EDGE,"E6.2.0")]});var subQ2=makeQuery(id+"F0.imprint","INTERSECT",VERTEX,{"disambiguationData":[OD(0.0)],"derivedFrom":[subQ0,sQuery(id+"F0.wireOp",EDGE,"E6.3.0")]});Q3=makeQuery(id+"F1.opExtrude","CAP_EDGE",EDGE,{"disambiguationData":[OSD([subQ0]),TDD([makeQuery(id+"F0.imprint","IMPRINT",EDGE,{"disambiguationData":[TD([[subQ2,1.0]])],"derivedFrom":subQ0}),makeQuery(id+"F0.imprint","IMPRINT",EDGE,{"disambiguationData":[TD([[subQ2,-1.0]])],"derivedFrom":subQ0}),makeQuery(id+"F0.imprint","IMPRINT",EDGE,{"disambiguationData":[TD([[subQ1,-1.0]])],"derivedFrom":subQ0})])],"isStart":false});}
            var Q4;
            {var subQ0=sQuery(id+"F0.wireOp",EDGE,"E4.0");var subQ1=makeQuery(id+"F0.imprint","INTERSECT",VERTEX,{"disambiguationData":[OD(1.0)],"derivedFrom":[subQ0,sQuery(id+"F0.wireOp",EDGE,"E6.3.0")]});var subQ2=makeQuery(id+"F0.imprint","INTERSECT",VERTEX,{"disambiguationData":[OD(1.0)],"derivedFrom":[subQ0,sQuery(id+"F0.wireOp",EDGE,"E6.4.0")]});Q4=makeQuery(id+"F1.opExtrude","CAP_EDGE",EDGE,{"disambiguationData":[OSD([subQ0]),TDD([makeQuery(id+"F0.imprint","IMPRINT",EDGE,{"disambiguationData":[TD([[makeQuery(id+"F0.imprint","INTERSECT",VERTEX,{"disambiguationData":[OD(1.0)],"derivedFrom":[subQ0,sQuery(id+"F0.wireOp",EDGE,"E6.4.1")]}),-1.0]])],"derivedFrom":subQ0}),makeQuery(id+"F0.imprint","IMPRINT",EDGE,{"disambiguationData":[TD([[subQ2,-1.0]])],"derivedFrom":subQ0}),makeQuery(id+"F0.imprint","IMPRINT",EDGE,{"disambiguationData":[TD([[subQ1,-1.0]])],"derivedFrom":subQ0})])],"isStart":false});}
            var Q5;
            {var subQ0=sQuery(id+"F0.wireOp",EDGE,"E4.0");var subQ1=makeQuery(id+"F0.imprint","INTERSECT",VERTEX,{"disambiguationData":[OD(0.0)],"derivedFrom":[subQ0,sQuery(id+"F0.wireOp",EDGE,"E6.10.0")]});var subQ2=makeQuery(id+"F0.imprint","INTERSECT",VERTEX,{"disambiguationData":[OD(1.0)],"derivedFrom":[subQ0,sQuery(id+"F0.wireOp",EDGE,"E6.11.0")]});Q5=makeQuery(id+"F1.opExtrude","CAP_EDGE",EDGE,{"disambiguationData":[OSD([subQ0]),TDD([makeQuery(id+"F0.imprint","IMPRINT",EDGE,{"disambiguationData":[TD([[makeQuery(id+"F0.imprint","INTERSECT",VERTEX,{"disambiguationData":[OD(1.0)],"derivedFrom":[subQ0,sQuery(id+"F0.wireOp",EDGE,"E6.11.1")]}),-1.0]])],"derivedFrom":subQ0}),makeQuery(id+"F0.imprint","IMPRINT",EDGE,{"disambiguationData":[TD([[subQ2,-1.0]])],"derivedFrom":subQ0}),makeQuery(id+"F0.imprint","IMPRINT",EDGE,{"disambiguationData":[TD([[subQ1,-1.0]])],"derivedFrom":subQ0})])],"isStart":false});}
            var Q6;
            {var subQ0=sQuery(id+"F0.wireOp",EDGE,"E4.0");var subQ1=makeQuery(id+"F0.imprint","INTERSECT",VERTEX,{"disambiguationData":[OD(0.0)],"derivedFrom":[subQ0,sQuery(id+"F0.wireOp",EDGE,"E6.9.0")]});var subQ2=makeQuery(id+"F0.imprint","INTERSECT",VERTEX,{"disambiguationData":[OD(1.0)],"derivedFrom":[subQ0,sQuery(id+"F0.wireOp",EDGE,"E6.10.0")]});Q6=makeQuery(id+"F1.opExtrude","CAP_EDGE",EDGE,{"disambiguationData":[OSD([subQ0]),TDD([makeQuery(id+"F0.imprint","IMPRINT",EDGE,{"disambiguationData":[TD([[makeQuery(id+"F0.imprint","INTERSECT",VERTEX,{"disambiguationData":[OD(1.0)],"derivedFrom":[subQ0,sQuery(id+"F0.wireOp",EDGE,"E6.10.1")]}),-1.0]])],"derivedFrom":subQ0}),makeQuery(id+"F0.imprint","IMPRINT",EDGE,{"disambiguationData":[TD([[subQ2,-1.0]])],"derivedFrom":subQ0}),makeQuery(id+"F0.imprint","IMPRINT",EDGE,{"disambiguationData":[TD([[subQ1,-1.0]])],"derivedFrom":subQ0})])],"isStart":false});}
            var Q7;
            {var subQ0=sQuery(id+"F0.wireOp",EDGE,"E4.0");var subQ1=makeQuery(id+"F0.imprint","INTERSECT",VERTEX,{"disambiguationData":[OD(0.0)],"derivedFrom":[subQ0,sQuery(id+"F0.wireOp",EDGE,"E6.8.0")]});var subQ2=makeQuery(id+"F0.imprint","INTERSECT",VERTEX,{"disambiguationData":[OD(1.0)],"derivedFrom":[subQ0,sQuery(id+"F0.wireOp",EDGE,"E6.9.0")]});Q7=makeQuery(id+"F1.opExtrude","CAP_EDGE",EDGE,{"disambiguationData":[OSD([subQ0]),TDD([makeQuery(id+"F0.imprint","IMPRINT",EDGE,{"disambiguationData":[TD([[makeQuery(id+"F0.imprint","INTERSECT",VERTEX,{"disambiguationData":[OD(1.0)],"derivedFrom":[subQ0,sQuery(id+"F0.wireOp",EDGE,"E6.9.1")]}),-1.0]])],"derivedFrom":subQ0}),makeQuery(id+"F0.imprint","IMPRINT",EDGE,{"disambiguationData":[TD([[subQ2,-1.0]])],"derivedFrom":subQ0}),makeQuery(id+"F0.imprint","IMPRINT",EDGE,{"disambiguationData":[TD([[subQ1,-1.0]])],"derivedFrom":subQ0})])],"isStart":false});}
            var Q8;
            {var subQ0=sQuery(id+"F0.wireOp",EDGE,"E4.0");var subQ1=makeQuery(id+"F0.imprint","INTERSECT",VERTEX,{"disambiguationData":[OD(0.0)],"derivedFrom":[subQ0,sQuery(id+"F0.wireOp",EDGE,"E6.7.0")]});var subQ2=makeQuery(id+"F0.imprint","INTERSECT",VERTEX,{"disambiguationData":[OD(1.0)],"derivedFrom":[subQ0,sQuery(id+"F0.wireOp",EDGE,"E6.8.0")]});Q8=makeQuery(id+"F1.opExtrude","CAP_EDGE",EDGE,{"disambiguationData":[OSD([subQ0]),TDD([makeQuery(id+"F0.imprint","IMPRINT",EDGE,{"disambiguationData":[TD([[makeQuery(id+"F0.imprint","INTERSECT",VERTEX,{"disambiguationData":[OD(1.0)],"derivedFrom":[subQ0,sQuery(id+"F0.wireOp",EDGE,"E6.8.1")]}),-1.0]])],"derivedFrom":subQ0}),makeQuery(id+"F0.imprint","IMPRINT",EDGE,{"disambiguationData":[TD([[subQ2,-1.0]])],"derivedFrom":subQ0}),makeQuery(id+"F0.imprint","IMPRINT",EDGE,{"disambiguationData":[TD([[subQ1,-1.0]])],"derivedFrom":subQ0})])],"isStart":false});}
            var Q9;
            {var subQ0=sQuery(id+"F0.wireOp",EDGE,"E4.0");var subQ1=makeQuery(id+"F0.imprint","INTERSECT",VERTEX,{"disambiguationData":[OD(0.0)],"derivedFrom":[subQ0,sQuery(id+"F0.wireOp",EDGE,"E6.6.0")]});var subQ2=makeQuery(id+"F0.imprint","INTERSECT",VERTEX,{"disambiguationData":[OD(1.0)],"derivedFrom":[subQ0,sQuery(id+"F0.wireOp",EDGE,"E6.7.0")]});Q9=makeQuery(id+"F1.opExtrude","CAP_EDGE",EDGE,{"disambiguationData":[OSD([subQ0]),TDD([makeQuery(id+"F0.imprint","IMPRINT",EDGE,{"disambiguationData":[TD([[makeQuery(id+"F0.imprint","INTERSECT",VERTEX,{"disambiguationData":[OD(1.0)],"derivedFrom":[subQ0,sQuery(id+"F0.wireOp",EDGE,"E6.7.1")]}),-1.0]])],"derivedFrom":subQ0}),makeQuery(id+"F0.imprint","IMPRINT",EDGE,{"disambiguationData":[TD([[subQ2,-1.0]])],"derivedFrom":subQ0}),makeQuery(id+"F0.imprint","IMPRINT",EDGE,{"disambiguationData":[TD([[subQ1,-1.0]])],"derivedFrom":subQ0})])],"isStart":false});}
            var Q10;
            {var subQ0=sQuery(id+"F0.wireOp",EDGE,"E4.0");var subQ1=makeQuery(id+"F0.imprint","INTERSECT",VERTEX,{"disambiguationData":[OD(0.0)],"derivedFrom":[subQ0,sQuery(id+"F0.wireOp",EDGE,"E6.5.0")]});var subQ2=makeQuery(id+"F0.imprint","INTERSECT",VERTEX,{"disambiguationData":[OD(1.0)],"derivedFrom":[subQ0,sQuery(id+"F0.wireOp",EDGE,"E6.6.0")]});Q10=makeQuery(id+"F1.opExtrude","CAP_EDGE",EDGE,{"disambiguationData":[OSD([subQ0]),TDD([makeQuery(id+"F0.imprint","IMPRINT",EDGE,{"disambiguationData":[TD([[makeQuery(id+"F0.imprint","INTERSECT",VERTEX,{"disambiguationData":[OD(1.0)],"derivedFrom":[subQ0,sQuery(id+"F0.wireOp",EDGE,"E6.6.1")]}),-1.0]])],"derivedFrom":subQ0}),makeQuery(id+"F0.imprint","IMPRINT",EDGE,{"disambiguationData":[TD([[subQ2,-1.0]])],"derivedFrom":subQ0}),makeQuery(id+"F0.imprint","IMPRINT",EDGE,{"disambiguationData":[TD([[subQ1,-1.0]])],"derivedFrom":subQ0})])],"isStart":false});}
            var Q11;
            {var subQ0=sQuery(id+"F0.wireOp",EDGE,"E4.0");var subQ1=makeQuery(id+"F0.imprint","INTERSECT",VERTEX,{"disambiguationData":[OD(0.0)],"derivedFrom":[subQ0,sQuery(id+"F0.wireOp",EDGE,"E6.4.0")]});var subQ2=makeQuery(id+"F0.imprint","INTERSECT",VERTEX,{"disambiguationData":[OD(1.0)],"derivedFrom":[subQ0,sQuery(id+"F0.wireOp",EDGE,"E6.5.0")]});Q11=makeQuery(id+"F1.opExtrude","CAP_EDGE",EDGE,{"disambiguationData":[OSD([subQ0]),TDD([makeQuery(id+"F0.imprint","IMPRINT",EDGE,{"disambiguationData":[TD([[makeQuery(id+"F0.imprint","INTERSECT",VERTEX,{"disambiguationData":[OD(1.0)],"derivedFrom":[subQ0,sQuery(id+"F0.wireOp",EDGE,"E6.5.1")]}),-1.0]])],"derivedFrom":subQ0}),makeQuery(id+"F0.imprint","IMPRINT",EDGE,{"disambiguationData":[TD([[subQ2,-1.0]])],"derivedFrom":subQ0}),makeQuery(id+"F0.imprint","IMPRINT",EDGE,{"disambiguationData":[TD([[subQ1,-1.0]])],"derivedFrom":subQ0})])],"isStart":false});}
            var Q12;
            {var subQ0=sQuery(id+"F0.wireOp",EDGE,"E4.0");var subQ1=makeQuery(id+"F0.imprint","INTERSECT",VERTEX,{"disambiguationData":[OD(0.0)],"derivedFrom":[subQ0,sQuery(id+"F0.wireOp",EDGE,"E6.6.0")]});var subQ2=makeQuery(id+"F0.imprint","INTERSECT",VERTEX,{"disambiguationData":[OD(1.0)],"derivedFrom":[subQ0,sQuery(id+"F0.wireOp",EDGE,"E6.7.0")]});Q12=makeQuery(id+"F1.opExtrude","CAP_EDGE",EDGE,{"disambiguationData":[OSD([subQ0]),TDD([makeQuery(id+"F0.imprint","IMPRINT",EDGE,{"disambiguationData":[TD([[makeQuery(id+"F0.imprint","INTERSECT",VERTEX,{"disambiguationData":[OD(1.0)],"derivedFrom":[subQ0,sQuery(id+"F0.wireOp",EDGE,"E6.7.1")]}),-1.0]])],"derivedFrom":subQ0}),makeQuery(id+"F0.imprint","IMPRINT",EDGE,{"disambiguationData":[TD([[subQ2,-1.0]])],"derivedFrom":subQ0}),makeQuery(id+"F0.imprint","IMPRINT",EDGE,{"disambiguationData":[TD([[subQ1,-1.0]])],"derivedFrom":subQ0})])],"isStart":true});}
            var Q13;
            {var subQ0=sQuery(id+"F0.wireOp",EDGE,"E4.0");var subQ1=makeQuery(id+"F0.imprint","INTERSECT",VERTEX,{"disambiguationData":[OD(0.0)],"derivedFrom":[subQ0,sQuery(id+"F0.wireOp",EDGE,"E6.5.0")]});var subQ2=makeQuery(id+"F0.imprint","INTERSECT",VERTEX,{"disambiguationData":[OD(1.0)],"derivedFrom":[subQ0,sQuery(id+"F0.wireOp",EDGE,"E6.6.0")]});Q13=makeQuery(id+"F1.opExtrude","CAP_EDGE",EDGE,{"disambiguationData":[OSD([subQ0]),TDD([makeQuery(id+"F0.imprint","IMPRINT",EDGE,{"disambiguationData":[TD([[makeQuery(id+"F0.imprint","INTERSECT",VERTEX,{"disambiguationData":[OD(1.0)],"derivedFrom":[subQ0,sQuery(id+"F0.wireOp",EDGE,"E6.6.1")]}),-1.0]])],"derivedFrom":subQ0}),makeQuery(id+"F0.imprint","IMPRINT",EDGE,{"disambiguationData":[TD([[subQ2,-1.0]])],"derivedFrom":subQ0}),makeQuery(id+"F0.imprint","IMPRINT",EDGE,{"disambiguationData":[TD([[subQ1,-1.0]])],"derivedFrom":subQ0})])],"isStart":true});}
            var Q14;
            {var subQ0=sQuery(id+"F0.wireOp",EDGE,"E4.0");var subQ1=makeQuery(id+"F0.imprint","INTERSECT",VERTEX,{"disambiguationData":[OD(0.0)],"derivedFrom":[subQ0,sQuery(id+"F0.wireOp",EDGE,"E6.7.0")]});var subQ2=makeQuery(id+"F0.imprint","INTERSECT",VERTEX,{"disambiguationData":[OD(1.0)],"derivedFrom":[subQ0,sQuery(id+"F0.wireOp",EDGE,"E6.8.0")]});Q14=makeQuery(id+"F1.opExtrude","CAP_EDGE",EDGE,{"disambiguationData":[OSD([subQ0]),TDD([makeQuery(id+"F0.imprint","IMPRINT",EDGE,{"disambiguationData":[TD([[makeQuery(id+"F0.imprint","INTERSECT",VERTEX,{"disambiguationData":[OD(1.0)],"derivedFrom":[subQ0,sQuery(id+"F0.wireOp",EDGE,"E6.8.1")]}),-1.0]])],"derivedFrom":subQ0}),makeQuery(id+"F0.imprint","IMPRINT",EDGE,{"disambiguationData":[TD([[subQ2,-1.0]])],"derivedFrom":subQ0}),makeQuery(id+"F0.imprint","IMPRINT",EDGE,{"disambiguationData":[TD([[subQ1,-1.0]])],"derivedFrom":subQ0})])],"isStart":true});}
            var Q15;
            {var subQ0=sQuery(id+"F0.wireOp",EDGE,"E4.0");var subQ1=makeQuery(id+"F0.imprint","INTERSECT",VERTEX,{"disambiguationData":[OD(0.0)],"derivedFrom":[subQ0,sQuery(id+"F0.wireOp",EDGE,"E6.8.0")]});var subQ2=makeQuery(id+"F0.imprint","INTERSECT",VERTEX,{"disambiguationData":[OD(1.0)],"derivedFrom":[subQ0,sQuery(id+"F0.wireOp",EDGE,"E6.9.0")]});Q15=makeQuery(id+"F1.opExtrude","CAP_EDGE",EDGE,{"disambiguationData":[OSD([subQ0]),TDD([makeQuery(id+"F0.imprint","IMPRINT",EDGE,{"disambiguationData":[TD([[makeQuery(id+"F0.imprint","INTERSECT",VERTEX,{"disambiguationData":[OD(1.0)],"derivedFrom":[subQ0,sQuery(id+"F0.wireOp",EDGE,"E6.9.1")]}),-1.0]])],"derivedFrom":subQ0}),makeQuery(id+"F0.imprint","IMPRINT",EDGE,{"disambiguationData":[TD([[subQ2,-1.0]])],"derivedFrom":subQ0}),makeQuery(id+"F0.imprint","IMPRINT",EDGE,{"disambiguationData":[TD([[subQ1,-1.0]])],"derivedFrom":subQ0})])],"isStart":true});}
            var Q16;
            {var subQ0=sQuery(id+"F0.wireOp",EDGE,"E4.0");var subQ1=makeQuery(id+"F0.imprint","INTERSECT",VERTEX,{"disambiguationData":[OD(0.0)],"derivedFrom":[subQ0,sQuery(id+"F0.wireOp",EDGE,"E6.9.0")]});var subQ2=makeQuery(id+"F0.imprint","INTERSECT",VERTEX,{"disambiguationData":[OD(1.0)],"derivedFrom":[subQ0,sQuery(id+"F0.wireOp",EDGE,"E6.10.0")]});Q16=makeQuery(id+"F1.opExtrude","CAP_EDGE",EDGE,{"disambiguationData":[OSD([subQ0]),TDD([makeQuery(id+"F0.imprint","IMPRINT",EDGE,{"disambiguationData":[TD([[makeQuery(id+"F0.imprint","INTERSECT",VERTEX,{"disambiguationData":[OD(1.0)],"derivedFrom":[subQ0,sQuery(id+"F0.wireOp",EDGE,"E6.10.1")]}),-1.0]])],"derivedFrom":subQ0}),makeQuery(id+"F0.imprint","IMPRINT",EDGE,{"disambiguationData":[TD([[subQ2,-1.0]])],"derivedFrom":subQ0}),makeQuery(id+"F0.imprint","IMPRINT",EDGE,{"disambiguationData":[TD([[subQ1,-1.0]])],"derivedFrom":subQ0})])],"isStart":true});}
            var Q17;
            {var subQ0=sQuery(id+"F0.wireOp",EDGE,"E4.0");var subQ1=makeQuery(id+"F0.imprint","INTERSECT",VERTEX,{"disambiguationData":[OD(0.0)],"derivedFrom":[subQ0,sQuery(id+"F0.wireOp",EDGE,"E6.4.0")]});var subQ2=makeQuery(id+"F0.imprint","INTERSECT",VERTEX,{"disambiguationData":[OD(1.0)],"derivedFrom":[subQ0,sQuery(id+"F0.wireOp",EDGE,"E6.5.0")]});Q17=makeQuery(id+"F1.opExtrude","CAP_EDGE",EDGE,{"disambiguationData":[OSD([subQ0]),TDD([makeQuery(id+"F0.imprint","IMPRINT",EDGE,{"disambiguationData":[TD([[makeQuery(id+"F0.imprint","INTERSECT",VERTEX,{"disambiguationData":[OD(1.0)],"derivedFrom":[subQ0,sQuery(id+"F0.wireOp",EDGE,"E6.5.1")]}),-1.0]])],"derivedFrom":subQ0}),makeQuery(id+"F0.imprint","IMPRINT",EDGE,{"disambiguationData":[TD([[subQ2,-1.0]])],"derivedFrom":subQ0}),makeQuery(id+"F0.imprint","IMPRINT",EDGE,{"disambiguationData":[TD([[subQ1,-1.0]])],"derivedFrom":subQ0})])],"isStart":true});}
            var Q18;
            {var subQ0=sQuery(id+"F0.wireOp",EDGE,"E4.0");var subQ1=makeQuery(id+"F0.imprint","INTERSECT",VERTEX,{"disambiguationData":[OD(1.0)],"derivedFrom":[subQ0,sQuery(id+"F0.wireOp",EDGE,"E6.3.0")]});var subQ2=makeQuery(id+"F0.imprint","INTERSECT",VERTEX,{"disambiguationData":[OD(1.0)],"derivedFrom":[subQ0,sQuery(id+"F0.wireOp",EDGE,"E6.4.0")]});Q18=makeQuery(id+"F1.opExtrude","CAP_EDGE",EDGE,{"disambiguationData":[OSD([subQ0]),TDD([makeQuery(id+"F0.imprint","IMPRINT",EDGE,{"disambiguationData":[TD([[makeQuery(id+"F0.imprint","INTERSECT",VERTEX,{"disambiguationData":[OD(1.0)],"derivedFrom":[subQ0,sQuery(id+"F0.wireOp",EDGE,"E6.4.1")]}),-1.0]])],"derivedFrom":subQ0}),makeQuery(id+"F0.imprint","IMPRINT",EDGE,{"disambiguationData":[TD([[subQ2,-1.0]])],"derivedFrom":subQ0}),makeQuery(id+"F0.imprint","IMPRINT",EDGE,{"disambiguationData":[TD([[subQ1,-1.0]])],"derivedFrom":subQ0})])],"isStart":true});}
            var Q19;
            {var subQ0=sQuery(id+"F0.wireOp",EDGE,"E4.0");var subQ1=makeQuery(id+"F0.imprint","INTERSECT",VERTEX,{"disambiguationData":[OD(0.0)],"derivedFrom":[subQ0,sQuery(id+"F0.wireOp",EDGE,"E6.2.0")]});var subQ2=makeQuery(id+"F0.imprint","INTERSECT",VERTEX,{"disambiguationData":[OD(0.0)],"derivedFrom":[subQ0,sQuery(id+"F0.wireOp",EDGE,"E6.3.0")]});Q19=makeQuery(id+"F1.opExtrude","CAP_EDGE",EDGE,{"disambiguationData":[OSD([subQ0]),TDD([makeQuery(id+"F0.imprint","IMPRINT",EDGE,{"disambiguationData":[TD([[subQ2,1.0]])],"derivedFrom":subQ0}),makeQuery(id+"F0.imprint","IMPRINT",EDGE,{"disambiguationData":[TD([[subQ2,-1.0]])],"derivedFrom":subQ0}),makeQuery(id+"F0.imprint","IMPRINT",EDGE,{"disambiguationData":[TD([[subQ1,-1.0]])],"derivedFrom":subQ0})])],"isStart":true});}
            var Q20;
            {var subQ0=sQuery(id+"F0.wireOp",EDGE,"E4.0");var subQ1=makeQuery(id+"F0.imprint","INTERSECT",VERTEX,{"disambiguationData":[OD(0.0)],"derivedFrom":[subQ0,sQuery(id+"F0.wireOp",EDGE,"E6.1.0")]});var subQ2=makeQuery(id+"F0.imprint","INTERSECT",VERTEX,{"disambiguationData":[OD(1.0)],"derivedFrom":[subQ0,sQuery(id+"F0.wireOp",EDGE,"E6.2.0")]});Q20=makeQuery(id+"F1.opExtrude","CAP_EDGE",EDGE,{"disambiguationData":[OSD([subQ0]),TDD([makeQuery(id+"F0.imprint","IMPRINT",EDGE,{"disambiguationData":[TD([[makeQuery(id+"F0.imprint","INTERSECT",VERTEX,{"disambiguationData":[OD(1.0)],"derivedFrom":[subQ0,sQuery(id+"F0.wireOp",EDGE,"E6.2.1")]}),-1.0]])],"derivedFrom":subQ0}),makeQuery(id+"F0.imprint","IMPRINT",EDGE,{"disambiguationData":[TD([[subQ2,-1.0]])],"derivedFrom":subQ0}),makeQuery(id+"F0.imprint","IMPRINT",EDGE,{"disambiguationData":[TD([[subQ1,-1.0]])],"derivedFrom":subQ0})])],"isStart":true});}
            var Q21;
            {var subQ0=sQuery(id+"F0.wireOp",EDGE,"E4.0");var subQ1=makeQuery(id+"F0.imprint","INTERSECT",VERTEX,{"disambiguationData":[OD(1.0)],"derivedFrom":[sQuery(id+"F0.wireOp",EDGE,"E2.0"),subQ0]});Q21=makeQuery(id+"F1.opExtrude","CAP_EDGE",EDGE,{"disambiguationData":[OSD([subQ0]),TDD([makeQuery(id+"F0.imprint","IMPRINT",EDGE,{"disambiguationData":[TD([[makeQuery(id+"F0.imprint","INTERSECT",VERTEX,{"disambiguationData":[OD(1.0)],"derivedFrom":[subQ0,sQuery(id+"F0.wireOp",EDGE,"E6.1.1")]}),-1.0]])],"derivedFrom":subQ0}),makeQuery(id+"F0.imprint","IMPRINT",EDGE,{"disambiguationData":[TD([[subQ1,1.0]])],"derivedFrom":subQ0}),makeQuery(id+"F0.imprint","IMPRINT",EDGE,{"disambiguationData":[TD([[subQ1,-1.0]])],"derivedFrom":subQ0})])],"isStart":true});}
            var Q22;
            {var subQ0=sQuery(id+"F0.wireOp",EDGE,"E4.0");var subQ1=makeQuery(id+"F0.imprint","INTERSECT",VERTEX,{"disambiguationData":[OD(0.0)],"derivedFrom":[subQ0,sQuery(id+"F0.wireOp",EDGE,"E6.11.0")]});var subQ2=makeQuery(id+"F0.imprint","INTERSECT",VERTEX,{"disambiguationData":[OD(0.0)],"derivedFrom":[sQuery(id+"F0.wireOp",EDGE,"E2.0"),subQ0]});Q22=makeQuery(id+"F1.opExtrude","CAP_EDGE",EDGE,{"disambiguationData":[OSD([subQ0]),TDD([makeQuery(id+"F0.imprint","IMPRINT",EDGE,{"disambiguationData":[TD([[subQ2,1.0]])],"derivedFrom":subQ0}),makeQuery(id+"F0.imprint","IMPRINT",EDGE,{"disambiguationData":[TD([[subQ2,-1.0]])],"derivedFrom":subQ0}),makeQuery(id+"F0.imprint","IMPRINT",EDGE,{"disambiguationData":[TD([[subQ1,-1.0]])],"derivedFrom":subQ0})])],"isStart":true});}
            var Q23;
            {var subQ0=sQuery(id+"F0.wireOp",EDGE,"E4.0");var subQ1=makeQuery(id+"F0.imprint","INTERSECT",VERTEX,{"disambiguationData":[OD(0.0)],"derivedFrom":[subQ0,sQuery(id+"F0.wireOp",EDGE,"E6.10.0")]});var subQ2=makeQuery(id+"F0.imprint","INTERSECT",VERTEX,{"disambiguationData":[OD(1.0)],"derivedFrom":[subQ0,sQuery(id+"F0.wireOp",EDGE,"E6.11.0")]});Q23=makeQuery(id+"F1.opExtrude","CAP_EDGE",EDGE,{"disambiguationData":[OSD([subQ0]),TDD([makeQuery(id+"F0.imprint","IMPRINT",EDGE,{"disambiguationData":[TD([[makeQuery(id+"F0.imprint","INTERSECT",VERTEX,{"disambiguationData":[OD(1.0)],"derivedFrom":[subQ0,sQuery(id+"F0.wireOp",EDGE,"E6.11.1")]}),-1.0]])],"derivedFrom":subQ0}),makeQuery(id+"F0.imprint","IMPRINT",EDGE,{"disambiguationData":[TD([[subQ2,-1.0]])],"derivedFrom":subQ0}),makeQuery(id+"F0.imprint","IMPRINT",EDGE,{"disambiguationData":[TD([[subQ1,-1.0]])],"derivedFrom":subQ0})])],"isStart":true});}
            fillet(context, id + "F2", {"entities" : qUnion([Q0, Q1, Q2, Q3, Q4, Q5, Q6, Q7, Q8, Q9, Q10, Q11, Q12, Q13, Q14, Q15, Q16, Q17, Q18, Q19, Q20, Q21, Q22, Q23]), "radius" : 1 * mm, "tangentPropagation" : true, "allowEdgeOverflow" : false});
        }
        {
            var Q0;
            {var subQ0=sQuery(id+"F0.wireOp",EDGE,"E3.0");var subQ1=makeQuery(id+"F0.imprint","INTERSECT",VERTEX,{"disambiguationData":[OD(0.0)],"derivedFrom":[subQ0,sQuery(id+"F0.wireOp",EDGE,"E6.1.0")]});var subQ2=makeQuery(id+"F0.imprint","INTERSECT",VERTEX,{"disambiguationData":[OD(1.0)],"derivedFrom":[subQ0,sQuery(id+"F0.wireOp",EDGE,"E6.2.0")]});Q0=makeQuery(id+"F1.opExtrude","CAP_EDGE",EDGE,{"disambiguationData":[OSD([subQ0]),TDD([makeQuery(id+"F0.imprint","IMPRINT",EDGE,{"disambiguationData":[TD([[subQ2,1.0]])],"derivedFrom":subQ0}),makeQuery(id+"F0.imprint","IMPRINT",EDGE,{"disambiguationData":[TD([[subQ2,-1.0]])],"derivedFrom":subQ0}),makeQuery(id+"F0.imprint","IMPRINT",EDGE,{"disambiguationData":[TD([[subQ1,-1.0]])],"derivedFrom":subQ0})])],"isStart":false});}
            var Q1;
            {var subQ0=sQuery(id+"F0.wireOp",EDGE,"E3.0");var subQ1=makeQuery(id+"F0.imprint","INTERSECT",VERTEX,{"disambiguationData":[OD(0.0)],"derivedFrom":[subQ0,sQuery(id+"F0.wireOp",EDGE,"E6.2.0")]});var subQ2=makeQuery(id+"F0.imprint","INTERSECT",VERTEX,{"disambiguationData":[OD(0.0)],"derivedFrom":[subQ0,sQuery(id+"F0.wireOp",EDGE,"E6.3.0")]});Q1=makeQuery(id+"F1.opExtrude","CAP_EDGE",EDGE,{"disambiguationData":[OSD([subQ0]),TDD([makeQuery(id+"F0.imprint","IMPRINT",EDGE,{"disambiguationData":[TD([[subQ2,1.0]])],"derivedFrom":subQ0}),makeQuery(id+"F0.imprint","IMPRINT",EDGE,{"disambiguationData":[TD([[subQ2,-1.0]])],"derivedFrom":subQ0}),makeQuery(id+"F0.imprint","IMPRINT",EDGE,{"disambiguationData":[TD([[subQ1,-1.0]])],"derivedFrom":subQ0})])],"isStart":false});}
            var Q2;
            {var subQ0=sQuery(id+"F0.wireOp",EDGE,"E3.0");var subQ1=makeQuery(id+"F0.imprint","INTERSECT",VERTEX,{"disambiguationData":[OD(1.0)],"derivedFrom":[subQ0,sQuery(id+"F0.wireOp",EDGE,"E6.3.0")]});var subQ2=makeQuery(id+"F0.imprint","INTERSECT",VERTEX,{"disambiguationData":[OD(1.0)],"derivedFrom":[subQ0,sQuery(id+"F0.wireOp",EDGE,"E6.4.0")]});Q2=makeQuery(id+"F1.opExtrude","CAP_EDGE",EDGE,{"disambiguationData":[OSD([subQ0]),TDD([makeQuery(id+"F0.imprint","IMPRINT",EDGE,{"disambiguationData":[TD([[subQ2,1.0]])],"derivedFrom":subQ0}),makeQuery(id+"F0.imprint","IMPRINT",EDGE,{"disambiguationData":[TD([[subQ2,-1.0]])],"derivedFrom":subQ0}),makeQuery(id+"F0.imprint","IMPRINT",EDGE,{"disambiguationData":[TD([[subQ1,-1.0]])],"derivedFrom":subQ0})])],"isStart":false});}
            var Q3;
            {var subQ0=sQuery(id+"F0.wireOp",EDGE,"E3.0");var subQ1=makeQuery(id+"F0.imprint","INTERSECT",VERTEX,{"disambiguationData":[OD(0.0)],"derivedFrom":[subQ0,sQuery(id+"F0.wireOp",EDGE,"E6.4.0")]});var subQ2=makeQuery(id+"F0.imprint","INTERSECT",VERTEX,{"disambiguationData":[OD(1.0)],"derivedFrom":[subQ0,sQuery(id+"F0.wireOp",EDGE,"E6.5.0")]});Q3=makeQuery(id+"F1.opExtrude","CAP_EDGE",EDGE,{"disambiguationData":[OSD([subQ0]),TDD([makeQuery(id+"F0.imprint","IMPRINT",EDGE,{"disambiguationData":[TD([[subQ2,1.0]])],"derivedFrom":subQ0}),makeQuery(id+"F0.imprint","IMPRINT",EDGE,{"disambiguationData":[TD([[subQ2,-1.0]])],"derivedFrom":subQ0}),makeQuery(id+"F0.imprint","IMPRINT",EDGE,{"disambiguationData":[TD([[subQ1,-1.0]])],"derivedFrom":subQ0})])],"isStart":false});}
            var Q4;
            {var subQ0=sQuery(id+"F0.wireOp",EDGE,"E3.0");var subQ1=makeQuery(id+"F0.imprint","INTERSECT",VERTEX,{"disambiguationData":[OD(0.0)],"derivedFrom":[subQ0,sQuery(id+"F0.wireOp",EDGE,"E6.5.0")]});var subQ2=makeQuery(id+"F0.imprint","INTERSECT",VERTEX,{"disambiguationData":[OD(1.0)],"derivedFrom":[subQ0,sQuery(id+"F0.wireOp",EDGE,"E6.6.0")]});Q4=makeQuery(id+"F1.opExtrude","CAP_EDGE",EDGE,{"disambiguationData":[OSD([subQ0]),TDD([makeQuery(id+"F0.imprint","IMPRINT",EDGE,{"disambiguationData":[TD([[subQ2,1.0]])],"derivedFrom":subQ0}),makeQuery(id+"F0.imprint","IMPRINT",EDGE,{"disambiguationData":[TD([[subQ2,-1.0]])],"derivedFrom":subQ0}),makeQuery(id+"F0.imprint","IMPRINT",EDGE,{"disambiguationData":[TD([[subQ1,-1.0]])],"derivedFrom":subQ0})])],"isStart":false});}
            var Q5;
            {var subQ0=sQuery(id+"F0.wireOp",EDGE,"E3.0");var subQ1=makeQuery(id+"F0.imprint","INTERSECT",VERTEX,{"disambiguationData":[OD(1.0)],"derivedFrom":[sQuery(id+"F0.wireOp",EDGE,"E2.0"),subQ0]});var subQ2=makeQuery(id+"F0.imprint","INTERSECT",VERTEX,{"disambiguationData":[OD(1.0)],"derivedFrom":[subQ0,sQuery(id+"F0.wireOp",EDGE,"E6.1.0")]});Q5=makeQuery(id+"F1.opExtrude","CAP_EDGE",EDGE,{"disambiguationData":[OSD([subQ0]),TDD([makeQuery(id+"F0.imprint","IMPRINT",EDGE,{"disambiguationData":[TD([[subQ2,1.0]])],"derivedFrom":subQ0}),makeQuery(id+"F0.imprint","IMPRINT",EDGE,{"disambiguationData":[TD([[subQ1,1.0]])],"derivedFrom":subQ0}),makeQuery(id+"F0.imprint","IMPRINT",EDGE,{"disambiguationData":[TD([[subQ1,-1.0]])],"derivedFrom":subQ0})])],"isStart":false});}
            var Q6;
            {var subQ0=sQuery(id+"F0.wireOp",EDGE,"E3.0");var subQ1=makeQuery(id+"F0.imprint","INTERSECT",VERTEX,{"disambiguationData":[OD(0.0)],"derivedFrom":[subQ0,sQuery(id+"F0.wireOp",EDGE,"E6.1.0")]});var subQ2=makeQuery(id+"F0.imprint","INTERSECT",VERTEX,{"disambiguationData":[OD(1.0)],"derivedFrom":[subQ0,sQuery(id+"F0.wireOp",EDGE,"E6.2.0")]});Q6=makeQuery(id+"F1.opExtrude","CAP_EDGE",EDGE,{"disambiguationData":[OSD([subQ0]),TDD([makeQuery(id+"F0.imprint","IMPRINT",EDGE,{"disambiguationData":[TD([[subQ2,1.0]])],"derivedFrom":subQ0}),makeQuery(id+"F0.imprint","IMPRINT",EDGE,{"disambiguationData":[TD([[subQ2,-1.0]])],"derivedFrom":subQ0}),makeQuery(id+"F0.imprint","IMPRINT",EDGE,{"disambiguationData":[TD([[subQ1,-1.0]])],"derivedFrom":subQ0})])],"isStart":true});}
            var Q7;
            {var subQ0=sQuery(id+"F0.wireOp",EDGE,"E6.2.1");var subQ1=sQuery(id+"F0.wireOp",EDGE,"E3.0");Q7=makeQuery(id+"F1.opExtrude","CAP_EDGE",EDGE,{"disambiguationData":[OSD([subQ0]),TDD([makeQuery(id+"F0.imprint","IMPRINT",EDGE,{"disambiguationData":[TD([[makeQuery(id+"F0.imprint","INTERSECT",VERTEX,{"disambiguationData":[OD(0.0)],"derivedFrom":[subQ1,subQ0]}),-1.0]])],"derivedFrom":subQ0})])],"isStart":false});}
            var Q8;
            {var subQ0=sQuery(id+"F0.wireOp",EDGE,"E3.0");var subQ1=makeQuery(id+"F0.imprint","INTERSECT",VERTEX,{"disambiguationData":[OD(1.0)],"derivedFrom":[sQuery(id+"F0.wireOp",EDGE,"E2.0"),subQ0]});var subQ2=makeQuery(id+"F0.imprint","INTERSECT",VERTEX,{"disambiguationData":[OD(1.0)],"derivedFrom":[subQ0,sQuery(id+"F0.wireOp",EDGE,"E6.1.0")]});Q8=makeQuery(id+"F1.opExtrude","CAP_EDGE",EDGE,{"disambiguationData":[OSD([subQ0]),TDD([makeQuery(id+"F0.imprint","IMPRINT",EDGE,{"disambiguationData":[TD([[subQ2,1.0]])],"derivedFrom":subQ0}),makeQuery(id+"F0.imprint","IMPRINT",EDGE,{"disambiguationData":[TD([[subQ1,1.0]])],"derivedFrom":subQ0}),makeQuery(id+"F0.imprint","IMPRINT",EDGE,{"disambiguationData":[TD([[subQ1,-1.0]])],"derivedFrom":subQ0})])],"isStart":true});}
            var Q9;
            {var subQ0=sQuery(id+"F0.wireOp",EDGE,"E3.0");var subQ1=makeQuery(id+"F0.imprint","INTERSECT",VERTEX,{"disambiguationData":[OD(0.0)],"derivedFrom":[subQ0,sQuery(id+"F0.wireOp",EDGE,"E6.11.0")]});var subQ2=makeQuery(id+"F0.imprint","INTERSECT",VERTEX,{"disambiguationData":[OD(0.0)],"derivedFrom":[sQuery(id+"F0.wireOp",EDGE,"E2.0"),subQ0]});Q9=makeQuery(id+"F1.opExtrude","CAP_EDGE",EDGE,{"disambiguationData":[OSD([subQ0]),TDD([makeQuery(id+"F0.imprint","IMPRINT",EDGE,{"disambiguationData":[TD([[subQ2,1.0]])],"derivedFrom":subQ0}),makeQuery(id+"F0.imprint","IMPRINT",EDGE,{"disambiguationData":[TD([[subQ2,-1.0]])],"derivedFrom":subQ0}),makeQuery(id+"F0.imprint","IMPRINT",EDGE,{"disambiguationData":[TD([[subQ1,-1.0]])],"derivedFrom":subQ0})])],"isStart":true});}
            var Q10;
            {var subQ0=sQuery(id+"F0.wireOp",EDGE,"E3.0");var subQ1=makeQuery(id+"F0.imprint","INTERSECT",VERTEX,{"disambiguationData":[OD(0.0)],"derivedFrom":[subQ0,sQuery(id+"F0.wireOp",EDGE,"E6.11.0")]});var subQ2=makeQuery(id+"F0.imprint","INTERSECT",VERTEX,{"disambiguationData":[OD(0.0)],"derivedFrom":[sQuery(id+"F0.wireOp",EDGE,"E2.0"),subQ0]});Q10=makeQuery(id+"F1.opExtrude","CAP_EDGE",EDGE,{"disambiguationData":[OSD([subQ0]),TDD([makeQuery(id+"F0.imprint","IMPRINT",EDGE,{"disambiguationData":[TD([[subQ2,1.0]])],"derivedFrom":subQ0}),makeQuery(id+"F0.imprint","IMPRINT",EDGE,{"disambiguationData":[TD([[subQ2,-1.0]])],"derivedFrom":subQ0}),makeQuery(id+"F0.imprint","IMPRINT",EDGE,{"disambiguationData":[TD([[subQ1,-1.0]])],"derivedFrom":subQ0})])],"isStart":false});}
            var Q11;
            {var subQ0=sQuery(id+"F0.wireOp",EDGE,"E3.0");var subQ1=makeQuery(id+"F0.imprint","INTERSECT",VERTEX,{"disambiguationData":[OD(0.0)],"derivedFrom":[subQ0,sQuery(id+"F0.wireOp",EDGE,"E6.10.0")]});var subQ2=makeQuery(id+"F0.imprint","INTERSECT",VERTEX,{"disambiguationData":[OD(1.0)],"derivedFrom":[subQ0,sQuery(id+"F0.wireOp",EDGE,"E6.11.0")]});Q11=makeQuery(id+"F1.opExtrude","CAP_EDGE",EDGE,{"disambiguationData":[OSD([subQ0]),TDD([makeQuery(id+"F0.imprint","IMPRINT",EDGE,{"disambiguationData":[TD([[subQ2,1.0]])],"derivedFrom":subQ0}),makeQuery(id+"F0.imprint","IMPRINT",EDGE,{"disambiguationData":[TD([[subQ2,-1.0]])],"derivedFrom":subQ0}),makeQuery(id+"F0.imprint","IMPRINT",EDGE,{"disambiguationData":[TD([[subQ1,-1.0]])],"derivedFrom":subQ0})])],"isStart":true});}
            var Q12;
            {var subQ0=sQuery(id+"F0.wireOp",EDGE,"E3.0");var subQ1=makeQuery(id+"F0.imprint","INTERSECT",VERTEX,{"disambiguationData":[OD(0.0)],"derivedFrom":[subQ0,sQuery(id+"F0.wireOp",EDGE,"E6.6.0")]});var subQ2=makeQuery(id+"F0.imprint","INTERSECT",VERTEX,{"disambiguationData":[OD(1.0)],"derivedFrom":[subQ0,sQuery(id+"F0.wireOp",EDGE,"E6.7.0")]});Q12=makeQuery(id+"F1.opExtrude","CAP_EDGE",EDGE,{"disambiguationData":[OSD([subQ0]),TDD([makeQuery(id+"F0.imprint","IMPRINT",EDGE,{"disambiguationData":[TD([[subQ2,1.0]])],"derivedFrom":subQ0}),makeQuery(id+"F0.imprint","IMPRINT",EDGE,{"disambiguationData":[TD([[subQ2,-1.0]])],"derivedFrom":subQ0}),makeQuery(id+"F0.imprint","IMPRINT",EDGE,{"disambiguationData":[TD([[subQ1,-1.0]])],"derivedFrom":subQ0})])],"isStart":false});}
            var Q13;
            {var subQ0=sQuery(id+"F0.wireOp",EDGE,"E3.0");var subQ1=makeQuery(id+"F0.imprint","INTERSECT",VERTEX,{"disambiguationData":[OD(0.0)],"derivedFrom":[subQ0,sQuery(id+"F0.wireOp",EDGE,"E6.7.0")]});var subQ2=makeQuery(id+"F0.imprint","INTERSECT",VERTEX,{"disambiguationData":[OD(1.0)],"derivedFrom":[subQ0,sQuery(id+"F0.wireOp",EDGE,"E6.8.0")]});Q13=makeQuery(id+"F1.opExtrude","CAP_EDGE",EDGE,{"disambiguationData":[OSD([subQ0]),TDD([makeQuery(id+"F0.imprint","IMPRINT",EDGE,{"disambiguationData":[TD([[subQ2,1.0]])],"derivedFrom":subQ0}),makeQuery(id+"F0.imprint","IMPRINT",EDGE,{"disambiguationData":[TD([[subQ2,-1.0]])],"derivedFrom":subQ0}),makeQuery(id+"F0.imprint","IMPRINT",EDGE,{"disambiguationData":[TD([[subQ1,-1.0]])],"derivedFrom":subQ0})])],"isStart":false});}
            var Q14;
            {var subQ0=sQuery(id+"F0.wireOp",EDGE,"E3.0");var subQ1=makeQuery(id+"F0.imprint","INTERSECT",VERTEX,{"disambiguationData":[OD(0.0)],"derivedFrom":[subQ0,sQuery(id+"F0.wireOp",EDGE,"E6.10.0")]});var subQ2=makeQuery(id+"F0.imprint","INTERSECT",VERTEX,{"disambiguationData":[OD(1.0)],"derivedFrom":[subQ0,sQuery(id+"F0.wireOp",EDGE,"E6.11.0")]});Q14=makeQuery(id+"F1.opExtrude","CAP_EDGE",EDGE,{"disambiguationData":[OSD([subQ0]),TDD([makeQuery(id+"F0.imprint","IMPRINT",EDGE,{"disambiguationData":[TD([[subQ2,1.0]])],"derivedFrom":subQ0}),makeQuery(id+"F0.imprint","IMPRINT",EDGE,{"disambiguationData":[TD([[subQ2,-1.0]])],"derivedFrom":subQ0}),makeQuery(id+"F0.imprint","IMPRINT",EDGE,{"disambiguationData":[TD([[subQ1,-1.0]])],"derivedFrom":subQ0})])],"isStart":false});}
            var Q15;
            {var subQ0=sQuery(id+"F0.wireOp",EDGE,"E3.0");var subQ1=makeQuery(id+"F0.imprint","INTERSECT",VERTEX,{"disambiguationData":[OD(0.0)],"derivedFrom":[subQ0,sQuery(id+"F0.wireOp",EDGE,"E6.9.0")]});var subQ2=makeQuery(id+"F0.imprint","INTERSECT",VERTEX,{"disambiguationData":[OD(1.0)],"derivedFrom":[subQ0,sQuery(id+"F0.wireOp",EDGE,"E6.10.0")]});Q15=makeQuery(id+"F1.opExtrude","CAP_EDGE",EDGE,{"disambiguationData":[OSD([subQ0]),TDD([makeQuery(id+"F0.imprint","IMPRINT",EDGE,{"disambiguationData":[TD([[subQ2,1.0]])],"derivedFrom":subQ0}),makeQuery(id+"F0.imprint","IMPRINT",EDGE,{"disambiguationData":[TD([[subQ2,-1.0]])],"derivedFrom":subQ0}),makeQuery(id+"F0.imprint","IMPRINT",EDGE,{"disambiguationData":[TD([[subQ1,-1.0]])],"derivedFrom":subQ0})])],"isStart":false});}
            var Q16;
            {var subQ0=sQuery(id+"F0.wireOp",EDGE,"E3.0");var subQ1=makeQuery(id+"F0.imprint","INTERSECT",VERTEX,{"disambiguationData":[OD(0.0)],"derivedFrom":[subQ0,sQuery(id+"F0.wireOp",EDGE,"E6.9.0")]});var subQ2=makeQuery(id+"F0.imprint","INTERSECT",VERTEX,{"disambiguationData":[OD(1.0)],"derivedFrom":[subQ0,sQuery(id+"F0.wireOp",EDGE,"E6.10.0")]});Q16=makeQuery(id+"F1.opExtrude","CAP_EDGE",EDGE,{"disambiguationData":[OSD([subQ0]),TDD([makeQuery(id+"F0.imprint","IMPRINT",EDGE,{"disambiguationData":[TD([[subQ2,1.0]])],"derivedFrom":subQ0}),makeQuery(id+"F0.imprint","IMPRINT",EDGE,{"disambiguationData":[TD([[subQ2,-1.0]])],"derivedFrom":subQ0}),makeQuery(id+"F0.imprint","IMPRINT",EDGE,{"disambiguationData":[TD([[subQ1,-1.0]])],"derivedFrom":subQ0})])],"isStart":true});}
            var Q17;
            {var subQ0=sQuery(id+"F0.wireOp",EDGE,"E3.0");var subQ1=makeQuery(id+"F0.imprint","INTERSECT",VERTEX,{"disambiguationData":[OD(0.0)],"derivedFrom":[subQ0,sQuery(id+"F0.wireOp",EDGE,"E6.8.0")]});var subQ2=makeQuery(id+"F0.imprint","INTERSECT",VERTEX,{"disambiguationData":[OD(1.0)],"derivedFrom":[subQ0,sQuery(id+"F0.wireOp",EDGE,"E6.9.0")]});Q17=makeQuery(id+"F1.opExtrude","CAP_EDGE",EDGE,{"disambiguationData":[OSD([subQ0]),TDD([makeQuery(id+"F0.imprint","IMPRINT",EDGE,{"disambiguationData":[TD([[subQ2,1.0]])],"derivedFrom":subQ0}),makeQuery(id+"F0.imprint","IMPRINT",EDGE,{"disambiguationData":[TD([[subQ2,-1.0]])],"derivedFrom":subQ0}),makeQuery(id+"F0.imprint","IMPRINT",EDGE,{"disambiguationData":[TD([[subQ1,-1.0]])],"derivedFrom":subQ0})])],"isStart":false});}
            var Q18;
            {var subQ0=sQuery(id+"F0.wireOp",EDGE,"E3.0");var subQ1=makeQuery(id+"F0.imprint","INTERSECT",VERTEX,{"disambiguationData":[OD(0.0)],"derivedFrom":[subQ0,sQuery(id+"F0.wireOp",EDGE,"E6.6.0")]});var subQ2=makeQuery(id+"F0.imprint","INTERSECT",VERTEX,{"disambiguationData":[OD(1.0)],"derivedFrom":[subQ0,sQuery(id+"F0.wireOp",EDGE,"E6.7.0")]});Q18=makeQuery(id+"F1.opExtrude","CAP_EDGE",EDGE,{"disambiguationData":[OSD([subQ0]),TDD([makeQuery(id+"F0.imprint","IMPRINT",EDGE,{"disambiguationData":[TD([[subQ2,1.0]])],"derivedFrom":subQ0}),makeQuery(id+"F0.imprint","IMPRINT",EDGE,{"disambiguationData":[TD([[subQ2,-1.0]])],"derivedFrom":subQ0}),makeQuery(id+"F0.imprint","IMPRINT",EDGE,{"disambiguationData":[TD([[subQ1,-1.0]])],"derivedFrom":subQ0})])],"isStart":true});}
            var Q19;
            {var subQ0=sQuery(id+"F0.wireOp",EDGE,"E3.0");var subQ1=makeQuery(id+"F0.imprint","INTERSECT",VERTEX,{"disambiguationData":[OD(0.0)],"derivedFrom":[subQ0,sQuery(id+"F0.wireOp",EDGE,"E6.5.0")]});var subQ2=makeQuery(id+"F0.imprint","INTERSECT",VERTEX,{"disambiguationData":[OD(1.0)],"derivedFrom":[subQ0,sQuery(id+"F0.wireOp",EDGE,"E6.6.0")]});Q19=makeQuery(id+"F1.opExtrude","CAP_EDGE",EDGE,{"disambiguationData":[OSD([subQ0]),TDD([makeQuery(id+"F0.imprint","IMPRINT",EDGE,{"disambiguationData":[TD([[subQ2,1.0]])],"derivedFrom":subQ0}),makeQuery(id+"F0.imprint","IMPRINT",EDGE,{"disambiguationData":[TD([[subQ2,-1.0]])],"derivedFrom":subQ0}),makeQuery(id+"F0.imprint","IMPRINT",EDGE,{"disambiguationData":[TD([[subQ1,-1.0]])],"derivedFrom":subQ0})])],"isStart":true});}
            var Q20;
            {var subQ0=sQuery(id+"F0.wireOp",EDGE,"E3.0");var subQ1=makeQuery(id+"F0.imprint","INTERSECT",VERTEX,{"disambiguationData":[OD(0.0)],"derivedFrom":[subQ0,sQuery(id+"F0.wireOp",EDGE,"E6.4.0")]});var subQ2=makeQuery(id+"F0.imprint","INTERSECT",VERTEX,{"disambiguationData":[OD(1.0)],"derivedFrom":[subQ0,sQuery(id+"F0.wireOp",EDGE,"E6.5.0")]});Q20=makeQuery(id+"F1.opExtrude","CAP_EDGE",EDGE,{"disambiguationData":[OSD([subQ0]),TDD([makeQuery(id+"F0.imprint","IMPRINT",EDGE,{"disambiguationData":[TD([[subQ2,1.0]])],"derivedFrom":subQ0}),makeQuery(id+"F0.imprint","IMPRINT",EDGE,{"disambiguationData":[TD([[subQ2,-1.0]])],"derivedFrom":subQ0}),makeQuery(id+"F0.imprint","IMPRINT",EDGE,{"disambiguationData":[TD([[subQ1,-1.0]])],"derivedFrom":subQ0})])],"isStart":true});}
            var Q21;
            {var subQ0=sQuery(id+"F0.wireOp",EDGE,"E3.0");var subQ1=makeQuery(id+"F0.imprint","INTERSECT",VERTEX,{"disambiguationData":[OD(1.0)],"derivedFrom":[subQ0,sQuery(id+"F0.wireOp",EDGE,"E6.3.0")]});var subQ2=makeQuery(id+"F0.imprint","INTERSECT",VERTEX,{"disambiguationData":[OD(1.0)],"derivedFrom":[subQ0,sQuery(id+"F0.wireOp",EDGE,"E6.4.0")]});Q21=makeQuery(id+"F1.opExtrude","CAP_EDGE",EDGE,{"disambiguationData":[OSD([subQ0]),TDD([makeQuery(id+"F0.imprint","IMPRINT",EDGE,{"disambiguationData":[TD([[subQ2,1.0]])],"derivedFrom":subQ0}),makeQuery(id+"F0.imprint","IMPRINT",EDGE,{"disambiguationData":[TD([[subQ2,-1.0]])],"derivedFrom":subQ0}),makeQuery(id+"F0.imprint","IMPRINT",EDGE,{"disambiguationData":[TD([[subQ1,-1.0]])],"derivedFrom":subQ0})])],"isStart":true});}
            var Q22;
            {var subQ0=sQuery(id+"F0.wireOp",EDGE,"E3.0");var subQ1=makeQuery(id+"F0.imprint","INTERSECT",VERTEX,{"disambiguationData":[OD(0.0)],"derivedFrom":[subQ0,sQuery(id+"F0.wireOp",EDGE,"E6.2.0")]});var subQ2=makeQuery(id+"F0.imprint","INTERSECT",VERTEX,{"disambiguationData":[OD(0.0)],"derivedFrom":[subQ0,sQuery(id+"F0.wireOp",EDGE,"E6.3.0")]});Q22=makeQuery(id+"F1.opExtrude","CAP_EDGE",EDGE,{"disambiguationData":[OSD([subQ0]),TDD([makeQuery(id+"F0.imprint","IMPRINT",EDGE,{"disambiguationData":[TD([[subQ2,1.0]])],"derivedFrom":subQ0}),makeQuery(id+"F0.imprint","IMPRINT",EDGE,{"disambiguationData":[TD([[subQ2,-1.0]])],"derivedFrom":subQ0}),makeQuery(id+"F0.imprint","IMPRINT",EDGE,{"disambiguationData":[TD([[subQ1,-1.0]])],"derivedFrom":subQ0})])],"isStart":true});}
            var Q23;
            {var subQ0=sQuery(id+"F0.wireOp",EDGE,"E3.0");var subQ1=makeQuery(id+"F0.imprint","INTERSECT",VERTEX,{"disambiguationData":[OD(0.0)],"derivedFrom":[subQ0,sQuery(id+"F0.wireOp",EDGE,"E6.8.0")]});var subQ2=makeQuery(id+"F0.imprint","INTERSECT",VERTEX,{"disambiguationData":[OD(1.0)],"derivedFrom":[subQ0,sQuery(id+"F0.wireOp",EDGE,"E6.9.0")]});Q23=makeQuery(id+"F1.opExtrude","CAP_EDGE",EDGE,{"disambiguationData":[OSD([subQ0]),TDD([makeQuery(id+"F0.imprint","IMPRINT",EDGE,{"disambiguationData":[TD([[subQ2,1.0]])],"derivedFrom":subQ0}),makeQuery(id+"F0.imprint","IMPRINT",EDGE,{"disambiguationData":[TD([[subQ2,-1.0]])],"derivedFrom":subQ0}),makeQuery(id+"F0.imprint","IMPRINT",EDGE,{"disambiguationData":[TD([[subQ1,-1.0]])],"derivedFrom":subQ0})])],"isStart":true});}
            var Q24;
            {var subQ0=sQuery(id+"F0.wireOp",EDGE,"E3.0");var subQ1=makeQuery(id+"F0.imprint","INTERSECT",VERTEX,{"disambiguationData":[OD(0.0)],"derivedFrom":[subQ0,sQuery(id+"F0.wireOp",EDGE,"E6.7.0")]});var subQ2=makeQuery(id+"F0.imprint","INTERSECT",VERTEX,{"disambiguationData":[OD(1.0)],"derivedFrom":[subQ0,sQuery(id+"F0.wireOp",EDGE,"E6.8.0")]});Q24=makeQuery(id+"F1.opExtrude","CAP_EDGE",EDGE,{"disambiguationData":[OSD([subQ0]),TDD([makeQuery(id+"F0.imprint","IMPRINT",EDGE,{"disambiguationData":[TD([[subQ2,1.0]])],"derivedFrom":subQ0}),makeQuery(id+"F0.imprint","IMPRINT",EDGE,{"disambiguationData":[TD([[subQ2,-1.0]])],"derivedFrom":subQ0}),makeQuery(id+"F0.imprint","IMPRINT",EDGE,{"disambiguationData":[TD([[subQ1,-1.0]])],"derivedFrom":subQ0})])],"isStart":true});}
            var Q25;
            {var subQ0=sQuery(id+"F0.wireOp",EDGE,"E6.1.1");var subQ1=sQuery(id+"F0.wireOp",EDGE,"E3.0");Q25=makeQuery(id+"F1.opExtrude","CAP_EDGE",EDGE,{"disambiguationData":[OSD([subQ0]),TDD([makeQuery(id+"F0.imprint","IMPRINT",EDGE,{"disambiguationData":[TD([[makeQuery(id+"F0.imprint","INTERSECT",VERTEX,{"disambiguationData":[OD(0.0)],"derivedFrom":[subQ1,subQ0]}),-1.0]])],"derivedFrom":subQ0})])],"isStart":false});}
            var Q26;
            {var subQ0=sQuery(id+"F0.wireOp",EDGE,"E5.0");var subQ1=sQuery(id+"F0.wireOp",EDGE,"E3.0");Q26=makeQuery(id+"F1.opExtrude","CAP_EDGE",EDGE,{"disambiguationData":[OSD([subQ0]),TDD([makeQuery(id+"F0.imprint","IMPRINT",EDGE,{"disambiguationData":[TD([[makeQuery(id+"F0.imprint","INTERSECT",VERTEX,{"disambiguationData":[OD(0.0)],"derivedFrom":[subQ1,subQ0]}),-1.0]])],"derivedFrom":subQ0})])],"isStart":false});}
            var Q27;
            {var subQ0=sQuery(id+"F0.wireOp",EDGE,"E6.11.1");var subQ1=sQuery(id+"F0.wireOp",EDGE,"E3.0");Q27=makeQuery(id+"F1.opExtrude","CAP_EDGE",EDGE,{"disambiguationData":[OSD([subQ0]),TDD([makeQuery(id+"F0.imprint","IMPRINT",EDGE,{"disambiguationData":[TD([[makeQuery(id+"F0.imprint","INTERSECT",VERTEX,{"disambiguationData":[OD(0.0)],"derivedFrom":[subQ1,subQ0]}),-1.0]])],"derivedFrom":subQ0})])],"isStart":false});}
            var Q28;
            {var subQ0=sQuery(id+"F0.wireOp",EDGE,"E6.10.1");var subQ1=sQuery(id+"F0.wireOp",EDGE,"E3.0");Q28=makeQuery(id+"F1.opExtrude","CAP_EDGE",EDGE,{"disambiguationData":[OSD([subQ0]),TDD([makeQuery(id+"F0.imprint","IMPRINT",EDGE,{"disambiguationData":[TD([[makeQuery(id+"F0.imprint","INTERSECT",VERTEX,{"disambiguationData":[OD(0.0)],"derivedFrom":[subQ1,subQ0]}),-1.0]])],"derivedFrom":subQ0})])],"isStart":false});}
            var Q29;
            {var subQ0=sQuery(id+"F0.wireOp",EDGE,"E6.9.1");var subQ1=sQuery(id+"F0.wireOp",EDGE,"E3.0");Q29=makeQuery(id+"F1.opExtrude","CAP_EDGE",EDGE,{"disambiguationData":[OSD([subQ0]),TDD([makeQuery(id+"F0.imprint","IMPRINT",EDGE,{"disambiguationData":[TD([[makeQuery(id+"F0.imprint","INTERSECT",VERTEX,{"disambiguationData":[OD(0.0)],"derivedFrom":[subQ1,subQ0]}),-1.0]])],"derivedFrom":subQ0})])],"isStart":false});}
            var Q30;
            {var subQ0=sQuery(id+"F0.wireOp",EDGE,"E6.8.1");var subQ1=sQuery(id+"F0.wireOp",EDGE,"E3.0");Q30=makeQuery(id+"F1.opExtrude","CAP_EDGE",EDGE,{"disambiguationData":[OSD([subQ0]),TDD([makeQuery(id+"F0.imprint","IMPRINT",EDGE,{"disambiguationData":[TD([[makeQuery(id+"F0.imprint","INTERSECT",VERTEX,{"disambiguationData":[OD(0.0)],"derivedFrom":[subQ1,subQ0]}),-1.0]])],"derivedFrom":subQ0})])],"isStart":false});}
            var Q31;
            {var subQ0=sQuery(id+"F0.wireOp",EDGE,"E6.7.1");var subQ1=sQuery(id+"F0.wireOp",EDGE,"E3.0");Q31=makeQuery(id+"F1.opExtrude","CAP_EDGE",EDGE,{"disambiguationData":[OSD([subQ0]),TDD([makeQuery(id+"F0.imprint","IMPRINT",EDGE,{"disambiguationData":[TD([[makeQuery(id+"F0.imprint","INTERSECT",VERTEX,{"disambiguationData":[OD(0.0)],"derivedFrom":[subQ1,subQ0]}),-1.0]])],"derivedFrom":subQ0})])],"isStart":false});}
            var Q32;
            {var subQ0=sQuery(id+"F0.wireOp",EDGE,"E6.5.1");var subQ1=sQuery(id+"F0.wireOp",EDGE,"E3.0");Q32=makeQuery(id+"F1.opExtrude","CAP_EDGE",EDGE,{"disambiguationData":[OSD([subQ0]),TDD([makeQuery(id+"F0.imprint","IMPRINT",EDGE,{"disambiguationData":[TD([[makeQuery(id+"F0.imprint","INTERSECT",VERTEX,{"disambiguationData":[OD(0.0)],"derivedFrom":[subQ1,subQ0]}),-1.0]])],"derivedFrom":subQ0})])],"isStart":false});}
            var Q33;
            {var subQ0=sQuery(id+"F0.wireOp",EDGE,"E6.6.1");var subQ1=sQuery(id+"F0.wireOp",EDGE,"E3.0");Q33=makeQuery(id+"F1.opExtrude","CAP_EDGE",EDGE,{"disambiguationData":[OSD([subQ0]),TDD([makeQuery(id+"F0.imprint","IMPRINT",EDGE,{"disambiguationData":[TD([[makeQuery(id+"F0.imprint","INTERSECT",VERTEX,{"disambiguationData":[OD(0.0)],"derivedFrom":[subQ1,subQ0]}),-1.0]])],"derivedFrom":subQ0})])],"isStart":false});}
            var Q34;
            {var subQ0=sQuery(id+"F0.wireOp",EDGE,"E6.4.1");var subQ1=sQuery(id+"F0.wireOp",EDGE,"E3.0");Q34=makeQuery(id+"F1.opExtrude","CAP_EDGE",EDGE,{"disambiguationData":[OSD([subQ0]),TDD([makeQuery(id+"F0.imprint","IMPRINT",EDGE,{"disambiguationData":[TD([[makeQuery(id+"F0.imprint","INTERSECT",VERTEX,{"disambiguationData":[OD(0.0)],"derivedFrom":[subQ1,subQ0]}),-1.0]])],"derivedFrom":subQ0})])],"isStart":false});}
            var Q35;
            {var subQ0=sQuery(id+"F0.wireOp",EDGE,"E6.3.1");var subQ1=sQuery(id+"F0.wireOp",EDGE,"E3.0");Q35=makeQuery(id+"F1.opExtrude","CAP_EDGE",EDGE,{"disambiguationData":[OSD([subQ0]),TDD([makeQuery(id+"F0.imprint","IMPRINT",EDGE,{"disambiguationData":[TD([[makeQuery(id+"F0.imprint","INTERSECT",VERTEX,{"disambiguationData":[OD(0.0)],"derivedFrom":[subQ1,subQ0]}),1.0]])],"derivedFrom":subQ0})])],"isStart":false});}
            var Q36;
            {var subQ0=sQuery(id+"F0.wireOp",EDGE,"E6.6.1");var subQ1=sQuery(id+"F0.wireOp",EDGE,"E3.0");Q36=makeQuery(id+"F1.opExtrude","CAP_EDGE",EDGE,{"disambiguationData":[OSD([subQ0]),TDD([makeQuery(id+"F0.imprint","IMPRINT",EDGE,{"disambiguationData":[TD([[makeQuery(id+"F0.imprint","INTERSECT",VERTEX,{"disambiguationData":[OD(0.0)],"derivedFrom":[subQ1,subQ0]}),-1.0]])],"derivedFrom":subQ0})])],"isStart":true});}
            var Q37;
            {var subQ0=sQuery(id+"F0.wireOp",EDGE,"E6.7.1");var subQ1=sQuery(id+"F0.wireOp",EDGE,"E3.0");Q37=makeQuery(id+"F1.opExtrude","CAP_EDGE",EDGE,{"disambiguationData":[OSD([subQ0]),TDD([makeQuery(id+"F0.imprint","IMPRINT",EDGE,{"disambiguationData":[TD([[makeQuery(id+"F0.imprint","INTERSECT",VERTEX,{"disambiguationData":[OD(0.0)],"derivedFrom":[subQ1,subQ0]}),-1.0]])],"derivedFrom":subQ0})])],"isStart":true});}
            var Q38;
            {var subQ0=sQuery(id+"F0.wireOp",EDGE,"E6.8.1");var subQ1=sQuery(id+"F0.wireOp",EDGE,"E3.0");Q38=makeQuery(id+"F1.opExtrude","CAP_EDGE",EDGE,{"disambiguationData":[OSD([subQ0]),TDD([makeQuery(id+"F0.imprint","IMPRINT",EDGE,{"disambiguationData":[TD([[makeQuery(id+"F0.imprint","INTERSECT",VERTEX,{"disambiguationData":[OD(0.0)],"derivedFrom":[subQ1,subQ0]}),-1.0]])],"derivedFrom":subQ0})])],"isStart":true});}
            var Q39;
            {var subQ0=sQuery(id+"F0.wireOp",EDGE,"E6.9.1");var subQ1=sQuery(id+"F0.wireOp",EDGE,"E3.0");Q39=makeQuery(id+"F1.opExtrude","CAP_EDGE",EDGE,{"disambiguationData":[OSD([subQ0]),TDD([makeQuery(id+"F0.imprint","IMPRINT",EDGE,{"disambiguationData":[TD([[makeQuery(id+"F0.imprint","INTERSECT",VERTEX,{"disambiguationData":[OD(0.0)],"derivedFrom":[subQ1,subQ0]}),-1.0]])],"derivedFrom":subQ0})])],"isStart":true});}
            var Q40;
            {var subQ0=sQuery(id+"F0.wireOp",EDGE,"E6.10.1");var subQ1=sQuery(id+"F0.wireOp",EDGE,"E3.0");Q40=makeQuery(id+"F1.opExtrude","CAP_EDGE",EDGE,{"disambiguationData":[OSD([subQ0]),TDD([makeQuery(id+"F0.imprint","IMPRINT",EDGE,{"disambiguationData":[TD([[makeQuery(id+"F0.imprint","INTERSECT",VERTEX,{"disambiguationData":[OD(0.0)],"derivedFrom":[subQ1,subQ0]}),-1.0]])],"derivedFrom":subQ0})])],"isStart":true});}
            var Q41;
            {var subQ0=sQuery(id+"F0.wireOp",EDGE,"E6.11.1");var subQ1=sQuery(id+"F0.wireOp",EDGE,"E3.0");Q41=makeQuery(id+"F1.opExtrude","CAP_EDGE",EDGE,{"disambiguationData":[OSD([subQ0]),TDD([makeQuery(id+"F0.imprint","IMPRINT",EDGE,{"disambiguationData":[TD([[makeQuery(id+"F0.imprint","INTERSECT",VERTEX,{"disambiguationData":[OD(0.0)],"derivedFrom":[subQ1,subQ0]}),-1.0]])],"derivedFrom":subQ0})])],"isStart":true});}
            var Q42;
            {var subQ0=sQuery(id+"F0.wireOp",EDGE,"E5.0");var subQ1=sQuery(id+"F0.wireOp",EDGE,"E3.0");Q42=makeQuery(id+"F1.opExtrude","CAP_EDGE",EDGE,{"disambiguationData":[OSD([subQ0]),TDD([makeQuery(id+"F0.imprint","IMPRINT",EDGE,{"disambiguationData":[TD([[makeQuery(id+"F0.imprint","INTERSECT",VERTEX,{"disambiguationData":[OD(0.0)],"derivedFrom":[subQ1,subQ0]}),-1.0]])],"derivedFrom":subQ0})])],"isStart":true});}
            var Q43;
            {var subQ0=sQuery(id+"F0.wireOp",EDGE,"E6.1.1");var subQ1=sQuery(id+"F0.wireOp",EDGE,"E3.0");Q43=makeQuery(id+"F1.opExtrude","CAP_EDGE",EDGE,{"disambiguationData":[OSD([subQ0]),TDD([makeQuery(id+"F0.imprint","IMPRINT",EDGE,{"disambiguationData":[TD([[makeQuery(id+"F0.imprint","INTERSECT",VERTEX,{"disambiguationData":[OD(0.0)],"derivedFrom":[subQ1,subQ0]}),-1.0]])],"derivedFrom":subQ0})])],"isStart":true});}
            var Q44;
            {var subQ0=sQuery(id+"F0.wireOp",EDGE,"E6.2.1");var subQ1=sQuery(id+"F0.wireOp",EDGE,"E3.0");Q44=makeQuery(id+"F1.opExtrude","CAP_EDGE",EDGE,{"disambiguationData":[OSD([subQ0]),TDD([makeQuery(id+"F0.imprint","IMPRINT",EDGE,{"disambiguationData":[TD([[makeQuery(id+"F0.imprint","INTERSECT",VERTEX,{"disambiguationData":[OD(0.0)],"derivedFrom":[subQ1,subQ0]}),-1.0]])],"derivedFrom":subQ0})])],"isStart":true});}
            var Q45;
            {var subQ0=sQuery(id+"F0.wireOp",EDGE,"E6.3.1");var subQ1=sQuery(id+"F0.wireOp",EDGE,"E3.0");Q45=makeQuery(id+"F1.opExtrude","CAP_EDGE",EDGE,{"disambiguationData":[OSD([subQ0]),TDD([makeQuery(id+"F0.imprint","IMPRINT",EDGE,{"disambiguationData":[TD([[makeQuery(id+"F0.imprint","INTERSECT",VERTEX,{"disambiguationData":[OD(0.0)],"derivedFrom":[subQ1,subQ0]}),1.0]])],"derivedFrom":subQ0})])],"isStart":true});}
            var Q46;
            {var subQ0=sQuery(id+"F0.wireOp",EDGE,"E6.4.1");var subQ1=sQuery(id+"F0.wireOp",EDGE,"E3.0");Q46=makeQuery(id+"F1.opExtrude","CAP_EDGE",EDGE,{"disambiguationData":[OSD([subQ0]),TDD([makeQuery(id+"F0.imprint","IMPRINT",EDGE,{"disambiguationData":[TD([[makeQuery(id+"F0.imprint","INTERSECT",VERTEX,{"disambiguationData":[OD(0.0)],"derivedFrom":[subQ1,subQ0]}),-1.0]])],"derivedFrom":subQ0})])],"isStart":true});}
            var Q47;
            {var subQ0=sQuery(id+"F0.wireOp",EDGE,"E6.5.1");var subQ1=sQuery(id+"F0.wireOp",EDGE,"E3.0");Q47=makeQuery(id+"F1.opExtrude","CAP_EDGE",EDGE,{"disambiguationData":[OSD([subQ0]),TDD([makeQuery(id+"F0.imprint","IMPRINT",EDGE,{"disambiguationData":[TD([[makeQuery(id+"F0.imprint","INTERSECT",VERTEX,{"disambiguationData":[OD(0.0)],"derivedFrom":[subQ1,subQ0]}),-1.0]])],"derivedFrom":subQ0})])],"isStart":true});}
            fillet(context, id + "F3", {"entities" : qUnion([Q0, Q1, Q2, Q3, Q4, Q5, Q6, Q7, Q8, Q9, Q10, Q11, Q12, Q13, Q14, Q15, Q16, Q17, Q18, Q19, Q20, Q21, Q22, Q23, Q24, Q25, Q26, Q27, Q28, Q29, Q30, Q31, Q32, Q33, Q34, Q35, Q36, Q37, Q38, Q39, Q40, Q41, Q42, Q43, Q44, Q45, Q46, Q47]), "radius" : 1 * mm, "allowEdgeOverflow" : false});
        }
        {
            var Q0;
            {var subQ0=sQuery(id+"F0.wireOp",EDGE,"E6.4.1");var subQ1=sQuery(id+"F0.wireOp",EDGE,"E3.0");var subQ3=makeQuery(id+"F0.imprint","INTERSECT",VERTEX,{"disambiguationData":[OD(1.0)],"derivedFrom":[subQ1,sQuery(id+"F0.wireOp",EDGE,"E6.3.0")]});var subQ4=makeQuery(id+"F0.imprint","INTERSECT",VERTEX,{"disambiguationData":[OD(1.0)],"derivedFrom":[subQ1,sQuery(id+"F0.wireOp",EDGE,"E6.4.0")]});Q0=makeQuery(id+"F3.opFillet","BLEND_EDGE",EDGE,{"blendedFrom":[makeQuery(id+"F1.opExtrude","CAP_EDGE",EDGE,{"disambiguationData":[OSD([subQ1]),TDD([makeQuery(id+"F0.imprint","IMPRINT",EDGE,{"disambiguationData":[TD([[subQ4,1.0]])],"derivedFrom":subQ1}),makeQuery(id+"F0.imprint","IMPRINT",EDGE,{"disambiguationData":[TD([[subQ4,-1.0]])],"derivedFrom":subQ1}),makeQuery(id+"F0.imprint","IMPRINT",EDGE,{"disambiguationData":[TD([[subQ3,-1.0]])],"derivedFrom":subQ1})])],"isStart":false}),makeQuery(id+"F1.opExtrude","CAP_EDGE",EDGE,{"disambiguationData":[OSD([subQ0]),TDD([makeQuery(id+"F0.imprint","IMPRINT",EDGE,{"disambiguationData":[TD([[makeQuery(id+"F0.imprint","INTERSECT",VERTEX,{"disambiguationData":[OD(0.0)],"derivedFrom":[subQ1,subQ0]}),-1.0]])],"derivedFrom":subQ0})])],"isStart":false})],"blendedInto":[]});}
            var Q1;
            {var subQ0=sQuery(id+"F0.wireOp",EDGE,"E6.3.1");var subQ1=sQuery(id+"F0.wireOp",EDGE,"E3.0");var subQ3=makeQuery(id+"F0.imprint","INTERSECT",VERTEX,{"disambiguationData":[OD(1.0)],"derivedFrom":[subQ1,sQuery(id+"F0.wireOp",EDGE,"E6.3.0")]});var subQ4=makeQuery(id+"F0.imprint","INTERSECT",VERTEX,{"disambiguationData":[OD(1.0)],"derivedFrom":[subQ1,sQuery(id+"F0.wireOp",EDGE,"E6.4.0")]});Q1=makeQuery(id+"F3.opFillet","BLEND_EDGE",EDGE,{"blendedFrom":[makeQuery(id+"F1.opExtrude","CAP_EDGE",EDGE,{"disambiguationData":[OSD([subQ1]),TDD([makeQuery(id+"F0.imprint","IMPRINT",EDGE,{"disambiguationData":[TD([[subQ4,1.0]])],"derivedFrom":subQ1}),makeQuery(id+"F0.imprint","IMPRINT",EDGE,{"disambiguationData":[TD([[subQ4,-1.0]])],"derivedFrom":subQ1}),makeQuery(id+"F0.imprint","IMPRINT",EDGE,{"disambiguationData":[TD([[subQ3,-1.0]])],"derivedFrom":subQ1})])],"isStart":false}),makeQuery(id+"F1.opExtrude","CAP_EDGE",EDGE,{"disambiguationData":[OSD([subQ0]),TDD([makeQuery(id+"F0.imprint","IMPRINT",EDGE,{"disambiguationData":[TD([[makeQuery(id+"F0.imprint","INTERSECT",VERTEX,{"disambiguationData":[OD(0.0)],"derivedFrom":[subQ1,subQ0]}),1.0]])],"derivedFrom":subQ0})])],"isStart":false})],"blendedInto":[]});}
            var Q2;
            {var subQ0=sQuery(id+"F0.wireOp",EDGE,"E6.2.1");var subQ1=sQuery(id+"F0.wireOp",EDGE,"E3.0");var subQ2=makeQuery(id+"F0.imprint","INTERSECT",VERTEX,{"disambiguationData":[OD(0.0)],"derivedFrom":[subQ1,subQ0]});var subQ3=makeQuery(id+"F0.imprint","INTERSECT",VERTEX,{"disambiguationData":[OD(0.0)],"derivedFrom":[subQ1,sQuery(id+"F0.wireOp",EDGE,"E6.2.0")]});var subQ4=makeQuery(id+"F0.imprint","INTERSECT",VERTEX,{"disambiguationData":[OD(0.0)],"derivedFrom":[subQ1,sQuery(id+"F0.wireOp",EDGE,"E6.3.0")]});Q2=makeQuery(id+"F3.opFillet","BLEND_EDGE",EDGE,{"blendedFrom":[makeQuery(id+"F1.opExtrude","CAP_EDGE",EDGE,{"disambiguationData":[OSD([subQ1]),TDD([makeQuery(id+"F0.imprint","IMPRINT",EDGE,{"disambiguationData":[TD([[subQ4,1.0]])],"derivedFrom":subQ1}),makeQuery(id+"F0.imprint","IMPRINT",EDGE,{"disambiguationData":[TD([[subQ4,-1.0]])],"derivedFrom":subQ1}),makeQuery(id+"F0.imprint","IMPRINT",EDGE,{"disambiguationData":[TD([[subQ3,-1.0]])],"derivedFrom":subQ1})])],"isStart":false}),makeQuery(id+"F1.opExtrude","CAP_EDGE",EDGE,{"disambiguationData":[OSD([subQ0]),TDD([makeQuery(id+"F0.imprint","IMPRINT",EDGE,{"disambiguationData":[TD([[subQ2,-1.0]])],"derivedFrom":subQ0})])],"isStart":false})],"blendedInto":[]});}
            var Q3;
            {var subQ0=sQuery(id+"F0.wireOp",EDGE,"E6.2.1");var subQ1=sQuery(id+"F0.wireOp",EDGE,"E3.0");var subQ3=makeQuery(id+"F0.imprint","INTERSECT",VERTEX,{"disambiguationData":[OD(0.0)],"derivedFrom":[subQ1,sQuery(id+"F0.wireOp",EDGE,"E6.1.0")]});var subQ4=makeQuery(id+"F0.imprint","INTERSECT",VERTEX,{"disambiguationData":[OD(1.0)],"derivedFrom":[subQ1,sQuery(id+"F0.wireOp",EDGE,"E6.2.0")]});Q3=makeQuery(id+"F3.opFillet","BLEND_EDGE",EDGE,{"blendedFrom":[makeQuery(id+"F1.opExtrude","CAP_EDGE",EDGE,{"disambiguationData":[OSD([subQ1]),TDD([makeQuery(id+"F0.imprint","IMPRINT",EDGE,{"disambiguationData":[TD([[subQ4,1.0]])],"derivedFrom":subQ1}),makeQuery(id+"F0.imprint","IMPRINT",EDGE,{"disambiguationData":[TD([[subQ4,-1.0]])],"derivedFrom":subQ1}),makeQuery(id+"F0.imprint","IMPRINT",EDGE,{"disambiguationData":[TD([[subQ3,-1.0]])],"derivedFrom":subQ1})])],"isStart":false}),makeQuery(id+"F1.opExtrude","CAP_EDGE",EDGE,{"disambiguationData":[OSD([subQ0]),TDD([makeQuery(id+"F0.imprint","IMPRINT",EDGE,{"disambiguationData":[TD([[makeQuery(id+"F0.imprint","INTERSECT",VERTEX,{"disambiguationData":[OD(0.0)],"derivedFrom":[subQ1,subQ0]}),-1.0]])],"derivedFrom":subQ0})])],"isStart":false})],"blendedInto":[]});}
            var Q4;
            {var subQ0=sQuery(id+"F0.wireOp",EDGE,"E6.1.1");var subQ1=sQuery(id+"F0.wireOp",EDGE,"E3.0");var subQ2=makeQuery(id+"F0.imprint","INTERSECT",VERTEX,{"disambiguationData":[OD(0.0)],"derivedFrom":[subQ1,subQ0]});var subQ3=makeQuery(id+"F0.imprint","INTERSECT",VERTEX,{"disambiguationData":[OD(0.0)],"derivedFrom":[subQ1,sQuery(id+"F0.wireOp",EDGE,"E6.1.0")]});var subQ4=makeQuery(id+"F0.imprint","INTERSECT",VERTEX,{"disambiguationData":[OD(1.0)],"derivedFrom":[subQ1,sQuery(id+"F0.wireOp",EDGE,"E6.2.0")]});Q4=makeQuery(id+"F3.opFillet","BLEND_EDGE",EDGE,{"blendedFrom":[makeQuery(id+"F1.opExtrude","CAP_EDGE",EDGE,{"disambiguationData":[OSD([subQ1]),TDD([makeQuery(id+"F0.imprint","IMPRINT",EDGE,{"disambiguationData":[TD([[subQ4,1.0]])],"derivedFrom":subQ1}),makeQuery(id+"F0.imprint","IMPRINT",EDGE,{"disambiguationData":[TD([[subQ4,-1.0]])],"derivedFrom":subQ1}),makeQuery(id+"F0.imprint","IMPRINT",EDGE,{"disambiguationData":[TD([[subQ3,-1.0]])],"derivedFrom":subQ1})])],"isStart":false}),makeQuery(id+"F1.opExtrude","CAP_EDGE",EDGE,{"disambiguationData":[OSD([subQ0]),TDD([makeQuery(id+"F0.imprint","IMPRINT",EDGE,{"disambiguationData":[TD([[subQ2,-1.0]])],"derivedFrom":subQ0})])],"isStart":false})],"blendedInto":[]});}
            var Q5;
            {var subQ0=sQuery(id+"F0.wireOp",EDGE,"E6.1.1");var subQ1=sQuery(id+"F0.wireOp",EDGE,"E3.0");var subQ3=makeQuery(id+"F0.imprint","INTERSECT",VERTEX,{"disambiguationData":[OD(1.0)],"derivedFrom":[sQuery(id+"F0.wireOp",EDGE,"E2.0"),subQ1]});var subQ4=makeQuery(id+"F0.imprint","INTERSECT",VERTEX,{"disambiguationData":[OD(1.0)],"derivedFrom":[subQ1,sQuery(id+"F0.wireOp",EDGE,"E6.1.0")]});Q5=makeQuery(id+"F3.opFillet","BLEND_EDGE",EDGE,{"blendedFrom":[makeQuery(id+"F1.opExtrude","CAP_EDGE",EDGE,{"disambiguationData":[OSD([subQ1]),TDD([makeQuery(id+"F0.imprint","IMPRINT",EDGE,{"disambiguationData":[TD([[subQ4,1.0]])],"derivedFrom":subQ1}),makeQuery(id+"F0.imprint","IMPRINT",EDGE,{"disambiguationData":[TD([[subQ3,1.0]])],"derivedFrom":subQ1}),makeQuery(id+"F0.imprint","IMPRINT",EDGE,{"disambiguationData":[TD([[subQ3,-1.0]])],"derivedFrom":subQ1})])],"isStart":true}),makeQuery(id+"F1.opExtrude","CAP_EDGE",EDGE,{"disambiguationData":[OSD([subQ0]),TDD([makeQuery(id+"F0.imprint","IMPRINT",EDGE,{"disambiguationData":[TD([[makeQuery(id+"F0.imprint","INTERSECT",VERTEX,{"disambiguationData":[OD(0.0)],"derivedFrom":[subQ1,subQ0]}),-1.0]])],"derivedFrom":subQ0})])],"isStart":true})],"blendedInto":[]});}
            var Q6;
            {var subQ0=sQuery(id+"F0.wireOp",EDGE,"E5.0");var subQ1=sQuery(id+"F0.wireOp",EDGE,"E3.0");var subQ2=makeQuery(id+"F0.imprint","INTERSECT",VERTEX,{"disambiguationData":[OD(0.0)],"derivedFrom":[subQ1,subQ0]});var subQ3=makeQuery(id+"F0.imprint","INTERSECT",VERTEX,{"disambiguationData":[OD(1.0)],"derivedFrom":[sQuery(id+"F0.wireOp",EDGE,"E2.0"),subQ1]});var subQ4=makeQuery(id+"F0.imprint","INTERSECT",VERTEX,{"disambiguationData":[OD(1.0)],"derivedFrom":[subQ1,sQuery(id+"F0.wireOp",EDGE,"E6.1.0")]});Q6=makeQuery(id+"F3.opFillet","BLEND_EDGE",EDGE,{"blendedFrom":[makeQuery(id+"F1.opExtrude","CAP_EDGE",EDGE,{"disambiguationData":[OSD([subQ1]),TDD([makeQuery(id+"F0.imprint","IMPRINT",EDGE,{"disambiguationData":[TD([[subQ4,1.0]])],"derivedFrom":subQ1}),makeQuery(id+"F0.imprint","IMPRINT",EDGE,{"disambiguationData":[TD([[subQ3,1.0]])],"derivedFrom":subQ1}),makeQuery(id+"F0.imprint","IMPRINT",EDGE,{"disambiguationData":[TD([[subQ3,-1.0]])],"derivedFrom":subQ1})])],"isStart":true}),makeQuery(id+"F1.opExtrude","CAP_EDGE",EDGE,{"disambiguationData":[OSD([subQ0]),TDD([makeQuery(id+"F0.imprint","IMPRINT",EDGE,{"disambiguationData":[TD([[subQ2,-1.0]])],"derivedFrom":subQ0})])],"isStart":true})],"blendedInto":[]});}
            var Q7;
            {var subQ0=sQuery(id+"F0.wireOp",EDGE,"E6.11.1");var subQ1=sQuery(id+"F0.wireOp",EDGE,"E3.0");var subQ2=makeQuery(id+"F0.imprint","INTERSECT",VERTEX,{"disambiguationData":[OD(0.0)],"derivedFrom":[subQ1,subQ0]});var subQ3=makeQuery(id+"F0.imprint","INTERSECT",VERTEX,{"disambiguationData":[OD(0.0)],"derivedFrom":[subQ1,sQuery(id+"F0.wireOp",EDGE,"E6.11.0")]});var subQ4=makeQuery(id+"F0.imprint","INTERSECT",VERTEX,{"disambiguationData":[OD(0.0)],"derivedFrom":[sQuery(id+"F0.wireOp",EDGE,"E2.0"),subQ1]});Q7=makeQuery(id+"F3.opFillet","BLEND_EDGE",EDGE,{"blendedFrom":[makeQuery(id+"F1.opExtrude","CAP_EDGE",EDGE,{"disambiguationData":[OSD([subQ1]),TDD([makeQuery(id+"F0.imprint","IMPRINT",EDGE,{"disambiguationData":[TD([[subQ4,1.0]])],"derivedFrom":subQ1}),makeQuery(id+"F0.imprint","IMPRINT",EDGE,{"disambiguationData":[TD([[subQ4,-1.0]])],"derivedFrom":subQ1}),makeQuery(id+"F0.imprint","IMPRINT",EDGE,{"disambiguationData":[TD([[subQ3,-1.0]])],"derivedFrom":subQ1})])],"isStart":false}),makeQuery(id+"F1.opExtrude","CAP_EDGE",EDGE,{"disambiguationData":[OSD([subQ0]),TDD([makeQuery(id+"F0.imprint","IMPRINT",EDGE,{"disambiguationData":[TD([[subQ2,-1.0]])],"derivedFrom":subQ0})])],"isStart":false})],"blendedInto":[]});}
            var Q8;
            {var subQ0=sQuery(id+"F0.wireOp",EDGE,"E6.10.1");var subQ1=sQuery(id+"F0.wireOp",EDGE,"E3.0");var subQ2=makeQuery(id+"F0.imprint","INTERSECT",VERTEX,{"disambiguationData":[OD(0.0)],"derivedFrom":[subQ1,subQ0]});var subQ3=makeQuery(id+"F0.imprint","INTERSECT",VERTEX,{"disambiguationData":[OD(0.0)],"derivedFrom":[subQ1,sQuery(id+"F0.wireOp",EDGE,"E6.10.0")]});var subQ4=makeQuery(id+"F0.imprint","INTERSECT",VERTEX,{"disambiguationData":[OD(1.0)],"derivedFrom":[subQ1,sQuery(id+"F0.wireOp",EDGE,"E6.11.0")]});Q8=makeQuery(id+"F3.opFillet","BLEND_EDGE",EDGE,{"blendedFrom":[makeQuery(id+"F1.opExtrude","CAP_EDGE",EDGE,{"disambiguationData":[OSD([subQ1]),TDD([makeQuery(id+"F0.imprint","IMPRINT",EDGE,{"disambiguationData":[TD([[subQ4,1.0]])],"derivedFrom":subQ1}),makeQuery(id+"F0.imprint","IMPRINT",EDGE,{"disambiguationData":[TD([[subQ4,-1.0]])],"derivedFrom":subQ1}),makeQuery(id+"F0.imprint","IMPRINT",EDGE,{"disambiguationData":[TD([[subQ3,-1.0]])],"derivedFrom":subQ1})])],"isStart":false}),makeQuery(id+"F1.opExtrude","CAP_EDGE",EDGE,{"disambiguationData":[OSD([subQ0]),TDD([makeQuery(id+"F0.imprint","IMPRINT",EDGE,{"disambiguationData":[TD([[subQ2,-1.0]])],"derivedFrom":subQ0})])],"isStart":false})],"blendedInto":[]});}
            var Q9;
            {var subQ0=sQuery(id+"F0.wireOp",EDGE,"E6.9.1");var subQ1=sQuery(id+"F0.wireOp",EDGE,"E3.0");var subQ2=makeQuery(id+"F0.imprint","INTERSECT",VERTEX,{"disambiguationData":[OD(0.0)],"derivedFrom":[subQ1,subQ0]});var subQ3=makeQuery(id+"F0.imprint","INTERSECT",VERTEX,{"disambiguationData":[OD(0.0)],"derivedFrom":[subQ1,sQuery(id+"F0.wireOp",EDGE,"E6.9.0")]});var subQ4=makeQuery(id+"F0.imprint","INTERSECT",VERTEX,{"disambiguationData":[OD(1.0)],"derivedFrom":[subQ1,sQuery(id+"F0.wireOp",EDGE,"E6.10.0")]});Q9=makeQuery(id+"F3.opFillet","BLEND_EDGE",EDGE,{"blendedFrom":[makeQuery(id+"F1.opExtrude","CAP_EDGE",EDGE,{"disambiguationData":[OSD([subQ1]),TDD([makeQuery(id+"F0.imprint","IMPRINT",EDGE,{"disambiguationData":[TD([[subQ4,1.0]])],"derivedFrom":subQ1}),makeQuery(id+"F0.imprint","IMPRINT",EDGE,{"disambiguationData":[TD([[subQ4,-1.0]])],"derivedFrom":subQ1}),makeQuery(id+"F0.imprint","IMPRINT",EDGE,{"disambiguationData":[TD([[subQ3,-1.0]])],"derivedFrom":subQ1})])],"isStart":false}),makeQuery(id+"F1.opExtrude","CAP_EDGE",EDGE,{"disambiguationData":[OSD([subQ0]),TDD([makeQuery(id+"F0.imprint","IMPRINT",EDGE,{"disambiguationData":[TD([[subQ2,-1.0]])],"derivedFrom":subQ0})])],"isStart":false})],"blendedInto":[]});}
            var Q10;
            {var subQ0=sQuery(id+"F0.wireOp",EDGE,"E6.8.1");var subQ1=sQuery(id+"F0.wireOp",EDGE,"E3.0");var subQ2=makeQuery(id+"F0.imprint","INTERSECT",VERTEX,{"disambiguationData":[OD(0.0)],"derivedFrom":[subQ1,subQ0]});var subQ3=makeQuery(id+"F0.imprint","INTERSECT",VERTEX,{"disambiguationData":[OD(0.0)],"derivedFrom":[subQ1,sQuery(id+"F0.wireOp",EDGE,"E6.8.0")]});var subQ4=makeQuery(id+"F0.imprint","INTERSECT",VERTEX,{"disambiguationData":[OD(1.0)],"derivedFrom":[subQ1,sQuery(id+"F0.wireOp",EDGE,"E6.9.0")]});Q10=makeQuery(id+"F3.opFillet","BLEND_EDGE",EDGE,{"blendedFrom":[makeQuery(id+"F1.opExtrude","CAP_EDGE",EDGE,{"disambiguationData":[OSD([subQ1]),TDD([makeQuery(id+"F0.imprint","IMPRINT",EDGE,{"disambiguationData":[TD([[subQ4,1.0]])],"derivedFrom":subQ1}),makeQuery(id+"F0.imprint","IMPRINT",EDGE,{"disambiguationData":[TD([[subQ4,-1.0]])],"derivedFrom":subQ1}),makeQuery(id+"F0.imprint","IMPRINT",EDGE,{"disambiguationData":[TD([[subQ3,-1.0]])],"derivedFrom":subQ1})])],"isStart":false}),makeQuery(id+"F1.opExtrude","CAP_EDGE",EDGE,{"disambiguationData":[OSD([subQ0]),TDD([makeQuery(id+"F0.imprint","IMPRINT",EDGE,{"disambiguationData":[TD([[subQ2,-1.0]])],"derivedFrom":subQ0})])],"isStart":false})],"blendedInto":[]});}
            var Q11;
            {var subQ0=sQuery(id+"F0.wireOp",EDGE,"E6.7.1");var subQ1=sQuery(id+"F0.wireOp",EDGE,"E3.0");var subQ2=makeQuery(id+"F0.imprint","INTERSECT",VERTEX,{"disambiguationData":[OD(0.0)],"derivedFrom":[subQ1,subQ0]});var subQ3=makeQuery(id+"F0.imprint","INTERSECT",VERTEX,{"disambiguationData":[OD(0.0)],"derivedFrom":[subQ1,sQuery(id+"F0.wireOp",EDGE,"E6.7.0")]});var subQ4=makeQuery(id+"F0.imprint","INTERSECT",VERTEX,{"disambiguationData":[OD(1.0)],"derivedFrom":[subQ1,sQuery(id+"F0.wireOp",EDGE,"E6.8.0")]});Q11=makeQuery(id+"F3.opFillet","BLEND_EDGE",EDGE,{"blendedFrom":[makeQuery(id+"F1.opExtrude","CAP_EDGE",EDGE,{"disambiguationData":[OSD([subQ1]),TDD([makeQuery(id+"F0.imprint","IMPRINT",EDGE,{"disambiguationData":[TD([[subQ4,1.0]])],"derivedFrom":subQ1}),makeQuery(id+"F0.imprint","IMPRINT",EDGE,{"disambiguationData":[TD([[subQ4,-1.0]])],"derivedFrom":subQ1}),makeQuery(id+"F0.imprint","IMPRINT",EDGE,{"disambiguationData":[TD([[subQ3,-1.0]])],"derivedFrom":subQ1})])],"isStart":false}),makeQuery(id+"F1.opExtrude","CAP_EDGE",EDGE,{"disambiguationData":[OSD([subQ0]),TDD([makeQuery(id+"F0.imprint","IMPRINT",EDGE,{"disambiguationData":[TD([[subQ2,-1.0]])],"derivedFrom":subQ0})])],"isStart":false})],"blendedInto":[]});}
            var Q12;
            {var subQ0=sQuery(id+"F0.wireOp",EDGE,"E6.6.1");var subQ1=sQuery(id+"F0.wireOp",EDGE,"E3.0");var subQ2=makeQuery(id+"F0.imprint","INTERSECT",VERTEX,{"disambiguationData":[OD(0.0)],"derivedFrom":[subQ1,subQ0]});var subQ3=makeQuery(id+"F0.imprint","INTERSECT",VERTEX,{"disambiguationData":[OD(0.0)],"derivedFrom":[subQ1,sQuery(id+"F0.wireOp",EDGE,"E6.6.0")]});var subQ4=makeQuery(id+"F0.imprint","INTERSECT",VERTEX,{"disambiguationData":[OD(1.0)],"derivedFrom":[subQ1,sQuery(id+"F0.wireOp",EDGE,"E6.7.0")]});Q12=makeQuery(id+"F3.opFillet","BLEND_EDGE",EDGE,{"blendedFrom":[makeQuery(id+"F1.opExtrude","CAP_EDGE",EDGE,{"disambiguationData":[OSD([subQ1]),TDD([makeQuery(id+"F0.imprint","IMPRINT",EDGE,{"disambiguationData":[TD([[subQ4,1.0]])],"derivedFrom":subQ1}),makeQuery(id+"F0.imprint","IMPRINT",EDGE,{"disambiguationData":[TD([[subQ4,-1.0]])],"derivedFrom":subQ1}),makeQuery(id+"F0.imprint","IMPRINT",EDGE,{"disambiguationData":[TD([[subQ3,-1.0]])],"derivedFrom":subQ1})])],"isStart":false}),makeQuery(id+"F1.opExtrude","CAP_EDGE",EDGE,{"disambiguationData":[OSD([subQ0]),TDD([makeQuery(id+"F0.imprint","IMPRINT",EDGE,{"disambiguationData":[TD([[subQ2,-1.0]])],"derivedFrom":subQ0})])],"isStart":false})],"blendedInto":[]});}
            var Q13;
            {var subQ0=sQuery(id+"F0.wireOp",EDGE,"E6.5.1");var subQ1=sQuery(id+"F0.wireOp",EDGE,"E3.0");var subQ2=makeQuery(id+"F0.imprint","INTERSECT",VERTEX,{"disambiguationData":[OD(0.0)],"derivedFrom":[subQ1,subQ0]});var subQ3=makeQuery(id+"F0.imprint","INTERSECT",VERTEX,{"disambiguationData":[OD(0.0)],"derivedFrom":[subQ1,sQuery(id+"F0.wireOp",EDGE,"E6.5.0")]});var subQ4=makeQuery(id+"F0.imprint","INTERSECT",VERTEX,{"disambiguationData":[OD(1.0)],"derivedFrom":[subQ1,sQuery(id+"F0.wireOp",EDGE,"E6.6.0")]});Q13=makeQuery(id+"F3.opFillet","BLEND_EDGE",EDGE,{"blendedFrom":[makeQuery(id+"F1.opExtrude","CAP_EDGE",EDGE,{"disambiguationData":[OSD([subQ1]),TDD([makeQuery(id+"F0.imprint","IMPRINT",EDGE,{"disambiguationData":[TD([[subQ4,1.0]])],"derivedFrom":subQ1}),makeQuery(id+"F0.imprint","IMPRINT",EDGE,{"disambiguationData":[TD([[subQ4,-1.0]])],"derivedFrom":subQ1}),makeQuery(id+"F0.imprint","IMPRINT",EDGE,{"disambiguationData":[TD([[subQ3,-1.0]])],"derivedFrom":subQ1})])],"isStart":false}),makeQuery(id+"F1.opExtrude","CAP_EDGE",EDGE,{"disambiguationData":[OSD([subQ0]),TDD([makeQuery(id+"F0.imprint","IMPRINT",EDGE,{"disambiguationData":[TD([[subQ2,-1.0]])],"derivedFrom":subQ0})])],"isStart":false})],"blendedInto":[]});}
            var Q14;
            {var subQ0=sQuery(id+"F0.wireOp",EDGE,"E6.4.1");var subQ1=sQuery(id+"F0.wireOp",EDGE,"E3.0");var subQ2=makeQuery(id+"F0.imprint","INTERSECT",VERTEX,{"disambiguationData":[OD(0.0)],"derivedFrom":[subQ1,subQ0]});var subQ3=makeQuery(id+"F0.imprint","INTERSECT",VERTEX,{"disambiguationData":[OD(0.0)],"derivedFrom":[subQ1,sQuery(id+"F0.wireOp",EDGE,"E6.4.0")]});var subQ4=makeQuery(id+"F0.imprint","INTERSECT",VERTEX,{"disambiguationData":[OD(1.0)],"derivedFrom":[subQ1,sQuery(id+"F0.wireOp",EDGE,"E6.5.0")]});Q14=makeQuery(id+"F3.opFillet","BLEND_EDGE",EDGE,{"blendedFrom":[makeQuery(id+"F1.opExtrude","CAP_EDGE",EDGE,{"disambiguationData":[OSD([subQ1]),TDD([makeQuery(id+"F0.imprint","IMPRINT",EDGE,{"disambiguationData":[TD([[subQ4,1.0]])],"derivedFrom":subQ1}),makeQuery(id+"F0.imprint","IMPRINT",EDGE,{"disambiguationData":[TD([[subQ4,-1.0]])],"derivedFrom":subQ1}),makeQuery(id+"F0.imprint","IMPRINT",EDGE,{"disambiguationData":[TD([[subQ3,-1.0]])],"derivedFrom":subQ1})])],"isStart":false}),makeQuery(id+"F1.opExtrude","CAP_EDGE",EDGE,{"disambiguationData":[OSD([subQ0]),TDD([makeQuery(id+"F0.imprint","IMPRINT",EDGE,{"disambiguationData":[TD([[subQ2,-1.0]])],"derivedFrom":subQ0})])],"isStart":false})],"blendedInto":[]});}
            var Q15;
            {var subQ0=sQuery(id+"F0.wireOp",EDGE,"E6.3.1");var subQ1=sQuery(id+"F0.wireOp",EDGE,"E3.0");var subQ2=makeQuery(id+"F0.imprint","INTERSECT",VERTEX,{"disambiguationData":[OD(0.0)],"derivedFrom":[subQ1,subQ0]});var subQ3=makeQuery(id+"F0.imprint","INTERSECT",VERTEX,{"disambiguationData":[OD(0.0)],"derivedFrom":[subQ1,sQuery(id+"F0.wireOp",EDGE,"E6.2.0")]});var subQ4=makeQuery(id+"F0.imprint","INTERSECT",VERTEX,{"disambiguationData":[OD(0.0)],"derivedFrom":[subQ1,sQuery(id+"F0.wireOp",EDGE,"E6.3.0")]});Q15=makeQuery(id+"F3.opFillet","BLEND_EDGE",EDGE,{"blendedFrom":[makeQuery(id+"F1.opExtrude","CAP_EDGE",EDGE,{"disambiguationData":[OSD([subQ1]),TDD([makeQuery(id+"F0.imprint","IMPRINT",EDGE,{"disambiguationData":[TD([[subQ4,1.0]])],"derivedFrom":subQ1}),makeQuery(id+"F0.imprint","IMPRINT",EDGE,{"disambiguationData":[TD([[subQ4,-1.0]])],"derivedFrom":subQ1}),makeQuery(id+"F0.imprint","IMPRINT",EDGE,{"disambiguationData":[TD([[subQ3,-1.0]])],"derivedFrom":subQ1})])],"isStart":false}),makeQuery(id+"F1.opExtrude","CAP_EDGE",EDGE,{"disambiguationData":[OSD([subQ0]),TDD([makeQuery(id+"F0.imprint","IMPRINT",EDGE,{"disambiguationData":[TD([[subQ2,1.0]])],"derivedFrom":subQ0})])],"isStart":false})],"blendedInto":[]});}
            var Q16;
            {var subQ0=sQuery(id+"F0.wireOp",EDGE,"E5.0");var subQ1=sQuery(id+"F0.wireOp",EDGE,"E3.0");var subQ3=makeQuery(id+"F0.imprint","INTERSECT",VERTEX,{"disambiguationData":[OD(0.0)],"derivedFrom":[subQ1,sQuery(id+"F0.wireOp",EDGE,"E6.11.0")]});var subQ4=makeQuery(id+"F0.imprint","INTERSECT",VERTEX,{"disambiguationData":[OD(0.0)],"derivedFrom":[sQuery(id+"F0.wireOp",EDGE,"E2.0"),subQ1]});Q16=makeQuery(id+"F3.opFillet","BLEND_EDGE",EDGE,{"blendedFrom":[makeQuery(id+"F1.opExtrude","CAP_EDGE",EDGE,{"disambiguationData":[OSD([subQ1]),TDD([makeQuery(id+"F0.imprint","IMPRINT",EDGE,{"disambiguationData":[TD([[subQ4,1.0]])],"derivedFrom":subQ1}),makeQuery(id+"F0.imprint","IMPRINT",EDGE,{"disambiguationData":[TD([[subQ4,-1.0]])],"derivedFrom":subQ1}),makeQuery(id+"F0.imprint","IMPRINT",EDGE,{"disambiguationData":[TD([[subQ3,-1.0]])],"derivedFrom":subQ1})])],"isStart":true}),makeQuery(id+"F1.opExtrude","CAP_EDGE",EDGE,{"disambiguationData":[OSD([subQ0]),TDD([makeQuery(id+"F0.imprint","IMPRINT",EDGE,{"disambiguationData":[TD([[makeQuery(id+"F0.imprint","INTERSECT",VERTEX,{"disambiguationData":[OD(0.0)],"derivedFrom":[subQ1,subQ0]}),-1.0]])],"derivedFrom":subQ0})])],"isStart":true})],"blendedInto":[]});}
            var Q17;
            {var subQ0=sQuery(id+"F0.wireOp",EDGE,"E6.11.1");var subQ1=sQuery(id+"F0.wireOp",EDGE,"E3.0");var subQ3=makeQuery(id+"F0.imprint","INTERSECT",VERTEX,{"disambiguationData":[OD(0.0)],"derivedFrom":[subQ1,sQuery(id+"F0.wireOp",EDGE,"E6.10.0")]});var subQ4=makeQuery(id+"F0.imprint","INTERSECT",VERTEX,{"disambiguationData":[OD(1.0)],"derivedFrom":[subQ1,sQuery(id+"F0.wireOp",EDGE,"E6.11.0")]});Q17=makeQuery(id+"F3.opFillet","BLEND_EDGE",EDGE,{"blendedFrom":[makeQuery(id+"F1.opExtrude","CAP_EDGE",EDGE,{"disambiguationData":[OSD([subQ1]),TDD([makeQuery(id+"F0.imprint","IMPRINT",EDGE,{"disambiguationData":[TD([[subQ4,1.0]])],"derivedFrom":subQ1}),makeQuery(id+"F0.imprint","IMPRINT",EDGE,{"disambiguationData":[TD([[subQ4,-1.0]])],"derivedFrom":subQ1}),makeQuery(id+"F0.imprint","IMPRINT",EDGE,{"disambiguationData":[TD([[subQ3,-1.0]])],"derivedFrom":subQ1})])],"isStart":true}),makeQuery(id+"F1.opExtrude","CAP_EDGE",EDGE,{"disambiguationData":[OSD([subQ0]),TDD([makeQuery(id+"F0.imprint","IMPRINT",EDGE,{"disambiguationData":[TD([[makeQuery(id+"F0.imprint","INTERSECT",VERTEX,{"disambiguationData":[OD(0.0)],"derivedFrom":[subQ1,subQ0]}),-1.0]])],"derivedFrom":subQ0})])],"isStart":true})],"blendedInto":[]});}
            var Q18;
            {var subQ0=sQuery(id+"F0.wireOp",EDGE,"E6.10.1");var subQ1=sQuery(id+"F0.wireOp",EDGE,"E3.0");var subQ3=makeQuery(id+"F0.imprint","INTERSECT",VERTEX,{"disambiguationData":[OD(0.0)],"derivedFrom":[subQ1,sQuery(id+"F0.wireOp",EDGE,"E6.9.0")]});var subQ4=makeQuery(id+"F0.imprint","INTERSECT",VERTEX,{"disambiguationData":[OD(1.0)],"derivedFrom":[subQ1,sQuery(id+"F0.wireOp",EDGE,"E6.10.0")]});Q18=makeQuery(id+"F3.opFillet","BLEND_EDGE",EDGE,{"blendedFrom":[makeQuery(id+"F1.opExtrude","CAP_EDGE",EDGE,{"disambiguationData":[OSD([subQ1]),TDD([makeQuery(id+"F0.imprint","IMPRINT",EDGE,{"disambiguationData":[TD([[subQ4,1.0]])],"derivedFrom":subQ1}),makeQuery(id+"F0.imprint","IMPRINT",EDGE,{"disambiguationData":[TD([[subQ4,-1.0]])],"derivedFrom":subQ1}),makeQuery(id+"F0.imprint","IMPRINT",EDGE,{"disambiguationData":[TD([[subQ3,-1.0]])],"derivedFrom":subQ1})])],"isStart":true}),makeQuery(id+"F1.opExtrude","CAP_EDGE",EDGE,{"disambiguationData":[OSD([subQ0]),TDD([makeQuery(id+"F0.imprint","IMPRINT",EDGE,{"disambiguationData":[TD([[makeQuery(id+"F0.imprint","INTERSECT",VERTEX,{"disambiguationData":[OD(0.0)],"derivedFrom":[subQ1,subQ0]}),-1.0]])],"derivedFrom":subQ0})])],"isStart":true})],"blendedInto":[]});}
            var Q19;
            {var subQ0=sQuery(id+"F0.wireOp",EDGE,"E6.9.1");var subQ1=sQuery(id+"F0.wireOp",EDGE,"E3.0");var subQ3=makeQuery(id+"F0.imprint","INTERSECT",VERTEX,{"disambiguationData":[OD(0.0)],"derivedFrom":[subQ1,sQuery(id+"F0.wireOp",EDGE,"E6.8.0")]});var subQ4=makeQuery(id+"F0.imprint","INTERSECT",VERTEX,{"disambiguationData":[OD(1.0)],"derivedFrom":[subQ1,sQuery(id+"F0.wireOp",EDGE,"E6.9.0")]});Q19=makeQuery(id+"F3.opFillet","BLEND_EDGE",EDGE,{"blendedFrom":[makeQuery(id+"F1.opExtrude","CAP_EDGE",EDGE,{"disambiguationData":[OSD([subQ1]),TDD([makeQuery(id+"F0.imprint","IMPRINT",EDGE,{"disambiguationData":[TD([[subQ4,1.0]])],"derivedFrom":subQ1}),makeQuery(id+"F0.imprint","IMPRINT",EDGE,{"disambiguationData":[TD([[subQ4,-1.0]])],"derivedFrom":subQ1}),makeQuery(id+"F0.imprint","IMPRINT",EDGE,{"disambiguationData":[TD([[subQ3,-1.0]])],"derivedFrom":subQ1})])],"isStart":true}),makeQuery(id+"F1.opExtrude","CAP_EDGE",EDGE,{"disambiguationData":[OSD([subQ0]),TDD([makeQuery(id+"F0.imprint","IMPRINT",EDGE,{"disambiguationData":[TD([[makeQuery(id+"F0.imprint","INTERSECT",VERTEX,{"disambiguationData":[OD(0.0)],"derivedFrom":[subQ1,subQ0]}),-1.0]])],"derivedFrom":subQ0})])],"isStart":true})],"blendedInto":[]});}
            var Q20;
            {var subQ0=sQuery(id+"F0.wireOp",EDGE,"E6.8.1");var subQ1=sQuery(id+"F0.wireOp",EDGE,"E3.0");var subQ3=makeQuery(id+"F0.imprint","INTERSECT",VERTEX,{"disambiguationData":[OD(0.0)],"derivedFrom":[subQ1,sQuery(id+"F0.wireOp",EDGE,"E6.7.0")]});var subQ4=makeQuery(id+"F0.imprint","INTERSECT",VERTEX,{"disambiguationData":[OD(1.0)],"derivedFrom":[subQ1,sQuery(id+"F0.wireOp",EDGE,"E6.8.0")]});Q20=makeQuery(id+"F3.opFillet","BLEND_EDGE",EDGE,{"blendedFrom":[makeQuery(id+"F1.opExtrude","CAP_EDGE",EDGE,{"disambiguationData":[OSD([subQ1]),TDD([makeQuery(id+"F0.imprint","IMPRINT",EDGE,{"disambiguationData":[TD([[subQ4,1.0]])],"derivedFrom":subQ1}),makeQuery(id+"F0.imprint","IMPRINT",EDGE,{"disambiguationData":[TD([[subQ4,-1.0]])],"derivedFrom":subQ1}),makeQuery(id+"F0.imprint","IMPRINT",EDGE,{"disambiguationData":[TD([[subQ3,-1.0]])],"derivedFrom":subQ1})])],"isStart":true}),makeQuery(id+"F1.opExtrude","CAP_EDGE",EDGE,{"disambiguationData":[OSD([subQ0]),TDD([makeQuery(id+"F0.imprint","IMPRINT",EDGE,{"disambiguationData":[TD([[makeQuery(id+"F0.imprint","INTERSECT",VERTEX,{"disambiguationData":[OD(0.0)],"derivedFrom":[subQ1,subQ0]}),-1.0]])],"derivedFrom":subQ0})])],"isStart":true})],"blendedInto":[]});}
            var Q21;
            {var subQ0=sQuery(id+"F0.wireOp",EDGE,"E6.7.1");var subQ1=sQuery(id+"F0.wireOp",EDGE,"E3.0");var subQ3=makeQuery(id+"F0.imprint","INTERSECT",VERTEX,{"disambiguationData":[OD(0.0)],"derivedFrom":[subQ1,sQuery(id+"F0.wireOp",EDGE,"E6.6.0")]});var subQ4=makeQuery(id+"F0.imprint","INTERSECT",VERTEX,{"disambiguationData":[OD(1.0)],"derivedFrom":[subQ1,sQuery(id+"F0.wireOp",EDGE,"E6.7.0")]});Q21=makeQuery(id+"F3.opFillet","BLEND_EDGE",EDGE,{"blendedFrom":[makeQuery(id+"F1.opExtrude","CAP_EDGE",EDGE,{"disambiguationData":[OSD([subQ1]),TDD([makeQuery(id+"F0.imprint","IMPRINT",EDGE,{"disambiguationData":[TD([[subQ4,1.0]])],"derivedFrom":subQ1}),makeQuery(id+"F0.imprint","IMPRINT",EDGE,{"disambiguationData":[TD([[subQ4,-1.0]])],"derivedFrom":subQ1}),makeQuery(id+"F0.imprint","IMPRINT",EDGE,{"disambiguationData":[TD([[subQ3,-1.0]])],"derivedFrom":subQ1})])],"isStart":true}),makeQuery(id+"F1.opExtrude","CAP_EDGE",EDGE,{"disambiguationData":[OSD([subQ0]),TDD([makeQuery(id+"F0.imprint","IMPRINT",EDGE,{"disambiguationData":[TD([[makeQuery(id+"F0.imprint","INTERSECT",VERTEX,{"disambiguationData":[OD(0.0)],"derivedFrom":[subQ1,subQ0]}),-1.0]])],"derivedFrom":subQ0})])],"isStart":true})],"blendedInto":[]});}
            var Q22;
            {var subQ0=sQuery(id+"F0.wireOp",EDGE,"E6.6.1");var subQ1=sQuery(id+"F0.wireOp",EDGE,"E3.0");var subQ3=makeQuery(id+"F0.imprint","INTERSECT",VERTEX,{"disambiguationData":[OD(0.0)],"derivedFrom":[subQ1,sQuery(id+"F0.wireOp",EDGE,"E6.5.0")]});var subQ4=makeQuery(id+"F0.imprint","INTERSECT",VERTEX,{"disambiguationData":[OD(1.0)],"derivedFrom":[subQ1,sQuery(id+"F0.wireOp",EDGE,"E6.6.0")]});Q22=makeQuery(id+"F3.opFillet","BLEND_EDGE",EDGE,{"blendedFrom":[makeQuery(id+"F1.opExtrude","CAP_EDGE",EDGE,{"disambiguationData":[OSD([subQ1]),TDD([makeQuery(id+"F0.imprint","IMPRINT",EDGE,{"disambiguationData":[TD([[subQ4,1.0]])],"derivedFrom":subQ1}),makeQuery(id+"F0.imprint","IMPRINT",EDGE,{"disambiguationData":[TD([[subQ4,-1.0]])],"derivedFrom":subQ1}),makeQuery(id+"F0.imprint","IMPRINT",EDGE,{"disambiguationData":[TD([[subQ3,-1.0]])],"derivedFrom":subQ1})])],"isStart":true}),makeQuery(id+"F1.opExtrude","CAP_EDGE",EDGE,{"disambiguationData":[OSD([subQ0]),TDD([makeQuery(id+"F0.imprint","IMPRINT",EDGE,{"disambiguationData":[TD([[makeQuery(id+"F0.imprint","INTERSECT",VERTEX,{"disambiguationData":[OD(0.0)],"derivedFrom":[subQ1,subQ0]}),-1.0]])],"derivedFrom":subQ0})])],"isStart":true})],"blendedInto":[]});}
            var Q23;
            {var subQ0=sQuery(id+"F0.wireOp",EDGE,"E6.5.1");var subQ1=sQuery(id+"F0.wireOp",EDGE,"E3.0");var subQ3=makeQuery(id+"F0.imprint","INTERSECT",VERTEX,{"disambiguationData":[OD(0.0)],"derivedFrom":[subQ1,sQuery(id+"F0.wireOp",EDGE,"E6.4.0")]});var subQ4=makeQuery(id+"F0.imprint","INTERSECT",VERTEX,{"disambiguationData":[OD(1.0)],"derivedFrom":[subQ1,sQuery(id+"F0.wireOp",EDGE,"E6.5.0")]});Q23=makeQuery(id+"F3.opFillet","BLEND_EDGE",EDGE,{"blendedFrom":[makeQuery(id+"F1.opExtrude","CAP_EDGE",EDGE,{"disambiguationData":[OSD([subQ1]),TDD([makeQuery(id+"F0.imprint","IMPRINT",EDGE,{"disambiguationData":[TD([[subQ4,1.0]])],"derivedFrom":subQ1}),makeQuery(id+"F0.imprint","IMPRINT",EDGE,{"disambiguationData":[TD([[subQ4,-1.0]])],"derivedFrom":subQ1}),makeQuery(id+"F0.imprint","IMPRINT",EDGE,{"disambiguationData":[TD([[subQ3,-1.0]])],"derivedFrom":subQ1})])],"isStart":true}),makeQuery(id+"F1.opExtrude","CAP_EDGE",EDGE,{"disambiguationData":[OSD([subQ0]),TDD([makeQuery(id+"F0.imprint","IMPRINT",EDGE,{"disambiguationData":[TD([[makeQuery(id+"F0.imprint","INTERSECT",VERTEX,{"disambiguationData":[OD(0.0)],"derivedFrom":[subQ1,subQ0]}),-1.0]])],"derivedFrom":subQ0})])],"isStart":true})],"blendedInto":[]});}
            fillet(context, id + "F4", {"entities" : qUnion([Q0, Q1, Q2, Q3, Q4, Q5, Q6, Q7, Q8, Q9, Q10, Q11, Q12, Q13, Q14, Q15, Q16, Q17, Q18, Q19, Q20, Q21, Q22, Q23]), "radius" : 3 * mm, "tangentPropagation" : true, "allowEdgeOverflow" : false});
        }
        {
            var Q0;
            {var subQ0=sQuery(id+"F0.wireOp",EDGE,"E6.7.1");var subQ1=sQuery(id+"F0.wireOp",EDGE,"E4.0");Q0=makeQuery(id+"F1.opExtrude","CAP_EDGE",EDGE,{"disambiguationData":[OSD([subQ0]),TDD([makeQuery(id+"F0.imprint","IMPRINT",EDGE,{"disambiguationData":[TD([[makeQuery(id+"F0.imprint","INTERSECT",VERTEX,{"disambiguationData":[OD(0.0)],"derivedFrom":[subQ1,subQ0]}),1.0]])],"derivedFrom":subQ0})])],"isStart":false});}
            var Q1;
            {var subQ0=sQuery(id+"F0.wireOp",EDGE,"E6.8.1");var subQ1=sQuery(id+"F0.wireOp",EDGE,"E4.0");Q1=makeQuery(id+"F1.opExtrude","CAP_EDGE",EDGE,{"disambiguationData":[OSD([subQ0]),TDD([makeQuery(id+"F0.imprint","IMPRINT",EDGE,{"disambiguationData":[TD([[makeQuery(id+"F0.imprint","INTERSECT",VERTEX,{"disambiguationData":[OD(0.0)],"derivedFrom":[subQ1,subQ0]}),1.0]])],"derivedFrom":subQ0})])],"isStart":false});}
            var Q2;
            {var subQ0=sQuery(id+"F0.wireOp",EDGE,"E6.9.1");var subQ1=sQuery(id+"F0.wireOp",EDGE,"E4.0");Q2=makeQuery(id+"F1.opExtrude","CAP_EDGE",EDGE,{"disambiguationData":[OSD([subQ0]),TDD([makeQuery(id+"F0.imprint","IMPRINT",EDGE,{"disambiguationData":[TD([[makeQuery(id+"F0.imprint","INTERSECT",VERTEX,{"disambiguationData":[OD(0.0)],"derivedFrom":[subQ1,subQ0]}),1.0]])],"derivedFrom":subQ0})])],"isStart":false});}
            var Q3;
            {var subQ0=sQuery(id+"F0.wireOp",EDGE,"E6.10.1");var subQ1=sQuery(id+"F0.wireOp",EDGE,"E4.0");Q3=makeQuery(id+"F1.opExtrude","CAP_EDGE",EDGE,{"disambiguationData":[OSD([subQ0]),TDD([makeQuery(id+"F0.imprint","IMPRINT",EDGE,{"disambiguationData":[TD([[makeQuery(id+"F0.imprint","INTERSECT",VERTEX,{"disambiguationData":[OD(0.0)],"derivedFrom":[subQ1,subQ0]}),1.0]])],"derivedFrom":subQ0})])],"isStart":false});}
            var Q4;
            {var subQ0=sQuery(id+"F0.wireOp",EDGE,"E6.11.1");var subQ1=sQuery(id+"F0.wireOp",EDGE,"E4.0");Q4=makeQuery(id+"F1.opExtrude","CAP_EDGE",EDGE,{"disambiguationData":[OSD([subQ0]),TDD([makeQuery(id+"F0.imprint","IMPRINT",EDGE,{"disambiguationData":[TD([[makeQuery(id+"F0.imprint","INTERSECT",VERTEX,{"disambiguationData":[OD(0.0)],"derivedFrom":[subQ1,subQ0]}),1.0]])],"derivedFrom":subQ0})])],"isStart":false});}
            var Q5;
            {var subQ0=sQuery(id+"F0.wireOp",EDGE,"E5.0");var subQ1=sQuery(id+"F0.wireOp",EDGE,"E4.0");Q5=makeQuery(id+"F1.opExtrude","CAP_EDGE",EDGE,{"disambiguationData":[OSD([subQ0]),TDD([makeQuery(id+"F0.imprint","IMPRINT",EDGE,{"disambiguationData":[TD([[makeQuery(id+"F0.imprint","INTERSECT",VERTEX,{"disambiguationData":[OD(0.0)],"derivedFrom":[subQ1,subQ0]}),1.0]])],"derivedFrom":subQ0})])],"isStart":false});}
            var Q6;
            {var subQ0=sQuery(id+"F0.wireOp",EDGE,"E6.1.1");var subQ1=sQuery(id+"F0.wireOp",EDGE,"E4.0");Q6=makeQuery(id+"F1.opExtrude","CAP_EDGE",EDGE,{"disambiguationData":[OSD([subQ0]),TDD([makeQuery(id+"F0.imprint","IMPRINT",EDGE,{"disambiguationData":[TD([[makeQuery(id+"F0.imprint","INTERSECT",VERTEX,{"disambiguationData":[OD(0.0)],"derivedFrom":[subQ1,subQ0]}),1.0]])],"derivedFrom":subQ0})])],"isStart":false});}
            var Q7;
            {var subQ0=sQuery(id+"F0.wireOp",EDGE,"E6.2.1");var subQ1=sQuery(id+"F0.wireOp",EDGE,"E4.0");Q7=makeQuery(id+"F1.opExtrude","CAP_EDGE",EDGE,{"disambiguationData":[OSD([subQ0]),TDD([makeQuery(id+"F0.imprint","IMPRINT",EDGE,{"disambiguationData":[TD([[makeQuery(id+"F0.imprint","INTERSECT",VERTEX,{"disambiguationData":[OD(0.0)],"derivedFrom":[subQ1,subQ0]}),1.0]])],"derivedFrom":subQ0})])],"isStart":false});}
            var Q8;
            {var subQ0=sQuery(id+"F0.wireOp",EDGE,"E6.3.1");var subQ1=sQuery(id+"F0.wireOp",EDGE,"E4.0");Q8=makeQuery(id+"F1.opExtrude","CAP_EDGE",EDGE,{"disambiguationData":[OSD([subQ0]),TDD([makeQuery(id+"F0.imprint","IMPRINT",EDGE,{"disambiguationData":[TD([[makeQuery(id+"F0.imprint","INTERSECT",VERTEX,{"disambiguationData":[OD(0.0)],"derivedFrom":[subQ1,subQ0]}),-1.0]])],"derivedFrom":subQ0})])],"isStart":false});}
            var Q9;
            {var subQ0=sQuery(id+"F0.wireOp",EDGE,"E6.4.1");var subQ1=sQuery(id+"F0.wireOp",EDGE,"E4.0");Q9=makeQuery(id+"F1.opExtrude","CAP_EDGE",EDGE,{"disambiguationData":[OSD([subQ0]),TDD([makeQuery(id+"F0.imprint","IMPRINT",EDGE,{"disambiguationData":[TD([[makeQuery(id+"F0.imprint","INTERSECT",VERTEX,{"disambiguationData":[OD(0.0)],"derivedFrom":[subQ1,subQ0]}),1.0]])],"derivedFrom":subQ0})])],"isStart":false});}
            var Q10;
            {var subQ0=sQuery(id+"F0.wireOp",EDGE,"E6.5.1");var subQ1=sQuery(id+"F0.wireOp",EDGE,"E4.0");Q10=makeQuery(id+"F1.opExtrude","CAP_EDGE",EDGE,{"disambiguationData":[OSD([subQ0]),TDD([makeQuery(id+"F0.imprint","IMPRINT",EDGE,{"disambiguationData":[TD([[makeQuery(id+"F0.imprint","INTERSECT",VERTEX,{"disambiguationData":[OD(0.0)],"derivedFrom":[subQ1,subQ0]}),1.0]])],"derivedFrom":subQ0})])],"isStart":false});}
            var Q11;
            {var subQ0=sQuery(id+"F0.wireOp",EDGE,"E6.6.1");var subQ1=sQuery(id+"F0.wireOp",EDGE,"E4.0");Q11=makeQuery(id+"F1.opExtrude","CAP_EDGE",EDGE,{"disambiguationData":[OSD([subQ0]),TDD([makeQuery(id+"F0.imprint","IMPRINT",EDGE,{"disambiguationData":[TD([[makeQuery(id+"F0.imprint","INTERSECT",VERTEX,{"disambiguationData":[OD(0.0)],"derivedFrom":[subQ1,subQ0]}),1.0]])],"derivedFrom":subQ0})])],"isStart":false});}
            var Q12;
            {var subQ0=sQuery(id+"F0.wireOp",EDGE,"E6.11.1");var subQ1=sQuery(id+"F0.wireOp",EDGE,"E4.0");Q12=makeQuery(id+"F1.opExtrude","CAP_EDGE",EDGE,{"disambiguationData":[OSD([subQ0]),TDD([makeQuery(id+"F0.imprint","IMPRINT",EDGE,{"disambiguationData":[TD([[makeQuery(id+"F0.imprint","INTERSECT",VERTEX,{"disambiguationData":[OD(0.0)],"derivedFrom":[subQ1,subQ0]}),1.0]])],"derivedFrom":subQ0})])],"isStart":true});}
            var Q13;
            {var subQ0=sQuery(id+"F0.wireOp",EDGE,"E6.10.1");var subQ1=sQuery(id+"F0.wireOp",EDGE,"E4.0");Q13=makeQuery(id+"F1.opExtrude","CAP_EDGE",EDGE,{"disambiguationData":[OSD([subQ0]),TDD([makeQuery(id+"F0.imprint","IMPRINT",EDGE,{"disambiguationData":[TD([[makeQuery(id+"F0.imprint","INTERSECT",VERTEX,{"disambiguationData":[OD(0.0)],"derivedFrom":[subQ1,subQ0]}),1.0]])],"derivedFrom":subQ0})])],"isStart":true});}
            var Q14;
            {var subQ0=sQuery(id+"F0.wireOp",EDGE,"E6.9.1");var subQ1=sQuery(id+"F0.wireOp",EDGE,"E4.0");Q14=makeQuery(id+"F1.opExtrude","CAP_EDGE",EDGE,{"disambiguationData":[OSD([subQ0]),TDD([makeQuery(id+"F0.imprint","IMPRINT",EDGE,{"disambiguationData":[TD([[makeQuery(id+"F0.imprint","INTERSECT",VERTEX,{"disambiguationData":[OD(0.0)],"derivedFrom":[subQ1,subQ0]}),1.0]])],"derivedFrom":subQ0})])],"isStart":true});}
            var Q15;
            {var subQ0=sQuery(id+"F0.wireOp",EDGE,"E6.8.1");var subQ1=sQuery(id+"F0.wireOp",EDGE,"E4.0");Q15=makeQuery(id+"F1.opExtrude","CAP_EDGE",EDGE,{"disambiguationData":[OSD([subQ0]),TDD([makeQuery(id+"F0.imprint","IMPRINT",EDGE,{"disambiguationData":[TD([[makeQuery(id+"F0.imprint","INTERSECT",VERTEX,{"disambiguationData":[OD(0.0)],"derivedFrom":[subQ1,subQ0]}),1.0]])],"derivedFrom":subQ0})])],"isStart":true});}
            var Q16;
            {var subQ0=sQuery(id+"F0.wireOp",EDGE,"E6.7.1");var subQ1=sQuery(id+"F0.wireOp",EDGE,"E4.0");Q16=makeQuery(id+"F1.opExtrude","CAP_EDGE",EDGE,{"disambiguationData":[OSD([subQ0]),TDD([makeQuery(id+"F0.imprint","IMPRINT",EDGE,{"disambiguationData":[TD([[makeQuery(id+"F0.imprint","INTERSECT",VERTEX,{"disambiguationData":[OD(0.0)],"derivedFrom":[subQ1,subQ0]}),1.0]])],"derivedFrom":subQ0})])],"isStart":true});}
            var Q17;
            {var subQ0=sQuery(id+"F0.wireOp",EDGE,"E6.6.1");var subQ1=sQuery(id+"F0.wireOp",EDGE,"E4.0");Q17=makeQuery(id+"F1.opExtrude","CAP_EDGE",EDGE,{"disambiguationData":[OSD([subQ0]),TDD([makeQuery(id+"F0.imprint","IMPRINT",EDGE,{"disambiguationData":[TD([[makeQuery(id+"F0.imprint","INTERSECT",VERTEX,{"disambiguationData":[OD(0.0)],"derivedFrom":[subQ1,subQ0]}),1.0]])],"derivedFrom":subQ0})])],"isStart":true});}
            var Q18;
            {var subQ0=sQuery(id+"F0.wireOp",EDGE,"E6.5.1");var subQ1=sQuery(id+"F0.wireOp",EDGE,"E4.0");Q18=makeQuery(id+"F1.opExtrude","CAP_EDGE",EDGE,{"disambiguationData":[OSD([subQ0]),TDD([makeQuery(id+"F0.imprint","IMPRINT",EDGE,{"disambiguationData":[TD([[makeQuery(id+"F0.imprint","INTERSECT",VERTEX,{"disambiguationData":[OD(0.0)],"derivedFrom":[subQ1,subQ0]}),1.0]])],"derivedFrom":subQ0})])],"isStart":true});}
            var Q19;
            {var subQ0=sQuery(id+"F0.wireOp",EDGE,"E6.4.1");var subQ1=sQuery(id+"F0.wireOp",EDGE,"E4.0");Q19=makeQuery(id+"F1.opExtrude","CAP_EDGE",EDGE,{"disambiguationData":[OSD([subQ0]),TDD([makeQuery(id+"F0.imprint","IMPRINT",EDGE,{"disambiguationData":[TD([[makeQuery(id+"F0.imprint","INTERSECT",VERTEX,{"disambiguationData":[OD(0.0)],"derivedFrom":[subQ1,subQ0]}),1.0]])],"derivedFrom":subQ0})])],"isStart":true});}
            var Q20;
            {var subQ0=sQuery(id+"F0.wireOp",EDGE,"E6.1.1");var subQ1=sQuery(id+"F0.wireOp",EDGE,"E4.0");Q20=makeQuery(id+"F1.opExtrude","CAP_EDGE",EDGE,{"disambiguationData":[OSD([subQ0]),TDD([makeQuery(id+"F0.imprint","IMPRINT",EDGE,{"disambiguationData":[TD([[makeQuery(id+"F0.imprint","INTERSECT",VERTEX,{"disambiguationData":[OD(0.0)],"derivedFrom":[subQ1,subQ0]}),1.0]])],"derivedFrom":subQ0})])],"isStart":true});}
            var Q21;
            {var subQ0=sQuery(id+"F0.wireOp",EDGE,"E5.0");var subQ1=sQuery(id+"F0.wireOp",EDGE,"E4.0");Q21=makeQuery(id+"F1.opExtrude","CAP_EDGE",EDGE,{"disambiguationData":[OSD([subQ0]),TDD([makeQuery(id+"F0.imprint","IMPRINT",EDGE,{"disambiguationData":[TD([[makeQuery(id+"F0.imprint","INTERSECT",VERTEX,{"disambiguationData":[OD(0.0)],"derivedFrom":[subQ1,subQ0]}),1.0]])],"derivedFrom":subQ0})])],"isStart":true});}
            var Q22;
            {var subQ0=sQuery(id+"F0.wireOp",EDGE,"E6.2.1");var subQ1=sQuery(id+"F0.wireOp",EDGE,"E4.0");Q22=makeQuery(id+"F1.opExtrude","CAP_EDGE",EDGE,{"disambiguationData":[OSD([subQ0]),TDD([makeQuery(id+"F0.imprint","IMPRINT",EDGE,{"disambiguationData":[TD([[makeQuery(id+"F0.imprint","INTERSECT",VERTEX,{"disambiguationData":[OD(0.0)],"derivedFrom":[subQ1,subQ0]}),1.0]])],"derivedFrom":subQ0})])],"isStart":true});}
            var Q23;
            {var subQ0=sQuery(id+"F0.wireOp",EDGE,"E6.3.1");var subQ1=sQuery(id+"F0.wireOp",EDGE,"E4.0");Q23=makeQuery(id+"F1.opExtrude","CAP_EDGE",EDGE,{"disambiguationData":[OSD([subQ0]),TDD([makeQuery(id+"F0.imprint","IMPRINT",EDGE,{"disambiguationData":[TD([[makeQuery(id+"F0.imprint","INTERSECT",VERTEX,{"disambiguationData":[OD(0.0)],"derivedFrom":[subQ1,subQ0]}),-1.0]])],"derivedFrom":subQ0})])],"isStart":true});}
            fillet(context, id + "F5", {"entities" : qUnion([Q0, Q1, Q2, Q3, Q4, Q5, Q6, Q7, Q8, Q9, Q10, Q11, Q12, Q13, Q14, Q15, Q16, Q17, Q18, Q19, Q20, Q21, Q22, Q23]), "radius" : 1 * mm, "tangentPropagation" : true, "allowEdgeOverflow" : false});
        }
        {
            var Q0;
            {var subQ0=sQuery(id+"F0.wireOp",EDGE,"E4.0");var subQ1=makeQuery(id+"F0.imprint","INTERSECT",VERTEX,{"disambiguationData":[OD(0.0)],"derivedFrom":[subQ0,sQuery(id+"F0.wireOp",EDGE,"E6.9.0")]});var subQ2=makeQuery(id+"F0.imprint","INTERSECT",VERTEX,{"disambiguationData":[OD(1.0)],"derivedFrom":[subQ0,sQuery(id+"F0.wireOp",EDGE,"E6.10.0")]});var subQ3=sQuery(id+"F0.wireOp",EDGE,"E6.10.1");var subQ4=makeQuery(id+"F0.imprint","INTERSECT",VERTEX,{"disambiguationData":[OD(1.0)],"derivedFrom":[subQ0,subQ3]});Q0=makeQuery(id+"F5.opFillet","BLEND_EDGE",EDGE,{"blendedFrom":[makeQuery(id+"F1.opExtrude","CAP_EDGE",EDGE,{"disambiguationData":[OSD([subQ3]),TDD([makeQuery(id+"F0.imprint","IMPRINT",EDGE,{"disambiguationData":[TD([[makeQuery(id+"F0.imprint","INTERSECT",VERTEX,{"disambiguationData":[OD(0.0)],"derivedFrom":[subQ0,subQ3]}),1.0]])],"derivedFrom":subQ3})])],"isStart":false}),makeQuery(id+"F2.opFillet","BLEND_FACE",FACE,{"disambiguationData":[OSD([subQ0]),TDD([makeQuery(id+"F1.opExtrude","CAP_EDGE",EDGE,{"disambiguationData":[OSD([subQ0]),TDD([makeQuery(id+"F0.imprint","IMPRINT",EDGE,{"disambiguationData":[TD([[subQ4,-1.0]])],"derivedFrom":subQ0}),makeQuery(id+"F0.imprint","IMPRINT",EDGE,{"disambiguationData":[TD([[subQ2,-1.0]])],"derivedFrom":subQ0}),makeQuery(id+"F0.imprint","IMPRINT",EDGE,{"disambiguationData":[TD([[subQ1,-1.0]])],"derivedFrom":subQ0})])],"isStart":true})])]})],"blendedInto":[makeQuery(id+"F2.opFillet","BLEND_FACE",FACE,{"disambiguationData":[OSD([subQ0]),TDD([makeQuery(id+"F1.opExtrude","CAP_EDGE",EDGE,{"disambiguationData":[OSD([subQ0]),TDD([makeQuery(id+"F0.imprint","IMPRINT",EDGE,{"disambiguationData":[TD([[subQ4,-1.0]])],"derivedFrom":subQ0}),makeQuery(id+"F0.imprint","IMPRINT",EDGE,{"disambiguationData":[TD([[subQ2,-1.0]])],"derivedFrom":subQ0}),makeQuery(id+"F0.imprint","IMPRINT",EDGE,{"disambiguationData":[TD([[subQ1,-1.0]])],"derivedFrom":subQ0})])],"isStart":true})])]})]});}
            var Q1;
            {var subQ0=sQuery(id+"F0.wireOp",EDGE,"E4.0");var subQ1=makeQuery(id+"F0.imprint","INTERSECT",VERTEX,{"disambiguationData":[OD(0.0)],"derivedFrom":[subQ0,sQuery(id+"F0.wireOp",EDGE,"E6.10.0")]});var subQ2=sQuery(id+"F0.wireOp",EDGE,"E6.10.1");var subQ3=makeQuery(id+"F0.imprint","INTERSECT",VERTEX,{"disambiguationData":[OD(0.0)],"derivedFrom":[subQ0,subQ2]});var subQ4=makeQuery(id+"F0.imprint","INTERSECT",VERTEX,{"disambiguationData":[OD(1.0)],"derivedFrom":[subQ0,sQuery(id+"F0.wireOp",EDGE,"E6.11.0")]});Q1=makeQuery(id+"F5.opFillet","BLEND_EDGE",EDGE,{"blendedFrom":[makeQuery(id+"F1.opExtrude","CAP_EDGE",EDGE,{"disambiguationData":[OSD([subQ2]),TDD([makeQuery(id+"F0.imprint","IMPRINT",EDGE,{"disambiguationData":[TD([[subQ3,1.0]])],"derivedFrom":subQ2})])],"isStart":false}),makeQuery(id+"F2.opFillet","BLEND_FACE",FACE,{"disambiguationData":[OSD([subQ0]),TDD([makeQuery(id+"F1.opExtrude","CAP_EDGE",EDGE,{"disambiguationData":[OSD([subQ0]),TDD([makeQuery(id+"F0.imprint","IMPRINT",EDGE,{"disambiguationData":[TD([[makeQuery(id+"F0.imprint","INTERSECT",VERTEX,{"disambiguationData":[OD(1.0)],"derivedFrom":[subQ0,sQuery(id+"F0.wireOp",EDGE,"E6.11.1")]}),-1.0]])],"derivedFrom":subQ0}),makeQuery(id+"F0.imprint","IMPRINT",EDGE,{"disambiguationData":[TD([[subQ4,-1.0]])],"derivedFrom":subQ0}),makeQuery(id+"F0.imprint","IMPRINT",EDGE,{"disambiguationData":[TD([[subQ1,-1.0]])],"derivedFrom":subQ0})])],"isStart":true})])]})],"blendedInto":[makeQuery(id+"F2.opFillet","BLEND_FACE",FACE,{"disambiguationData":[OSD([subQ0]),TDD([makeQuery(id+"F1.opExtrude","CAP_EDGE",EDGE,{"disambiguationData":[OSD([subQ0]),TDD([makeQuery(id+"F0.imprint","IMPRINT",EDGE,{"disambiguationData":[TD([[makeQuery(id+"F0.imprint","INTERSECT",VERTEX,{"disambiguationData":[OD(1.0)],"derivedFrom":[subQ0,sQuery(id+"F0.wireOp",EDGE,"E6.11.1")]}),-1.0]])],"derivedFrom":subQ0}),makeQuery(id+"F0.imprint","IMPRINT",EDGE,{"disambiguationData":[TD([[subQ4,-1.0]])],"derivedFrom":subQ0}),makeQuery(id+"F0.imprint","IMPRINT",EDGE,{"disambiguationData":[TD([[subQ1,-1.0]])],"derivedFrom":subQ0})])],"isStart":true})])]})]});}
            var Q2;
            {var subQ0=sQuery(id+"F0.wireOp",EDGE,"E4.0");var subQ1=makeQuery(id+"F0.imprint","INTERSECT",VERTEX,{"disambiguationData":[OD(0.0)],"derivedFrom":[subQ0,sQuery(id+"F0.wireOp",EDGE,"E6.9.0")]});var subQ2=sQuery(id+"F0.wireOp",EDGE,"E6.9.1");var subQ3=makeQuery(id+"F0.imprint","INTERSECT",VERTEX,{"disambiguationData":[OD(0.0)],"derivedFrom":[subQ0,subQ2]});var subQ4=makeQuery(id+"F0.imprint","INTERSECT",VERTEX,{"disambiguationData":[OD(1.0)],"derivedFrom":[subQ0,sQuery(id+"F0.wireOp",EDGE,"E6.10.0")]});Q2=makeQuery(id+"F5.opFillet","BLEND_EDGE",EDGE,{"blendedFrom":[makeQuery(id+"F1.opExtrude","CAP_EDGE",EDGE,{"disambiguationData":[OSD([subQ2]),TDD([makeQuery(id+"F0.imprint","IMPRINT",EDGE,{"disambiguationData":[TD([[subQ3,1.0]])],"derivedFrom":subQ2})])],"isStart":false}),makeQuery(id+"F2.opFillet","BLEND_FACE",FACE,{"disambiguationData":[OSD([subQ0]),TDD([makeQuery(id+"F1.opExtrude","CAP_EDGE",EDGE,{"disambiguationData":[OSD([subQ0]),TDD([makeQuery(id+"F0.imprint","IMPRINT",EDGE,{"disambiguationData":[TD([[makeQuery(id+"F0.imprint","INTERSECT",VERTEX,{"disambiguationData":[OD(1.0)],"derivedFrom":[subQ0,sQuery(id+"F0.wireOp",EDGE,"E6.10.1")]}),-1.0]])],"derivedFrom":subQ0}),makeQuery(id+"F0.imprint","IMPRINT",EDGE,{"disambiguationData":[TD([[subQ4,-1.0]])],"derivedFrom":subQ0}),makeQuery(id+"F0.imprint","IMPRINT",EDGE,{"disambiguationData":[TD([[subQ1,-1.0]])],"derivedFrom":subQ0})])],"isStart":true})])]})],"blendedInto":[makeQuery(id+"F2.opFillet","BLEND_FACE",FACE,{"disambiguationData":[OSD([subQ0]),TDD([makeQuery(id+"F1.opExtrude","CAP_EDGE",EDGE,{"disambiguationData":[OSD([subQ0]),TDD([makeQuery(id+"F0.imprint","IMPRINT",EDGE,{"disambiguationData":[TD([[makeQuery(id+"F0.imprint","INTERSECT",VERTEX,{"disambiguationData":[OD(1.0)],"derivedFrom":[subQ0,sQuery(id+"F0.wireOp",EDGE,"E6.10.1")]}),-1.0]])],"derivedFrom":subQ0}),makeQuery(id+"F0.imprint","IMPRINT",EDGE,{"disambiguationData":[TD([[subQ4,-1.0]])],"derivedFrom":subQ0}),makeQuery(id+"F0.imprint","IMPRINT",EDGE,{"disambiguationData":[TD([[subQ1,-1.0]])],"derivedFrom":subQ0})])],"isStart":true})])]})]});}
            var Q3;
            {var subQ0=sQuery(id+"F0.wireOp",EDGE,"E4.0");var subQ1=makeQuery(id+"F0.imprint","INTERSECT",VERTEX,{"disambiguationData":[OD(0.0)],"derivedFrom":[subQ0,sQuery(id+"F0.wireOp",EDGE,"E6.7.0")]});var subQ2=makeQuery(id+"F0.imprint","INTERSECT",VERTEX,{"disambiguationData":[OD(1.0)],"derivedFrom":[subQ0,sQuery(id+"F0.wireOp",EDGE,"E6.8.0")]});var subQ3=sQuery(id+"F0.wireOp",EDGE,"E6.8.1");var subQ4=makeQuery(id+"F0.imprint","INTERSECT",VERTEX,{"disambiguationData":[OD(1.0)],"derivedFrom":[subQ0,subQ3]});Q3=makeQuery(id+"F5.opFillet","BLEND_EDGE",EDGE,{"blendedFrom":[makeQuery(id+"F1.opExtrude","CAP_EDGE",EDGE,{"disambiguationData":[OSD([subQ3]),TDD([makeQuery(id+"F0.imprint","IMPRINT",EDGE,{"disambiguationData":[TD([[makeQuery(id+"F0.imprint","INTERSECT",VERTEX,{"disambiguationData":[OD(0.0)],"derivedFrom":[subQ0,subQ3]}),1.0]])],"derivedFrom":subQ3})])],"isStart":false}),makeQuery(id+"F2.opFillet","BLEND_FACE",FACE,{"disambiguationData":[OSD([subQ0]),TDD([makeQuery(id+"F1.opExtrude","CAP_EDGE",EDGE,{"disambiguationData":[OSD([subQ0]),TDD([makeQuery(id+"F0.imprint","IMPRINT",EDGE,{"disambiguationData":[TD([[subQ4,-1.0]])],"derivedFrom":subQ0}),makeQuery(id+"F0.imprint","IMPRINT",EDGE,{"disambiguationData":[TD([[subQ2,-1.0]])],"derivedFrom":subQ0}),makeQuery(id+"F0.imprint","IMPRINT",EDGE,{"disambiguationData":[TD([[subQ1,-1.0]])],"derivedFrom":subQ0})])],"isStart":true})])]})],"blendedInto":[makeQuery(id+"F2.opFillet","BLEND_FACE",FACE,{"disambiguationData":[OSD([subQ0]),TDD([makeQuery(id+"F1.opExtrude","CAP_EDGE",EDGE,{"disambiguationData":[OSD([subQ0]),TDD([makeQuery(id+"F0.imprint","IMPRINT",EDGE,{"disambiguationData":[TD([[subQ4,-1.0]])],"derivedFrom":subQ0}),makeQuery(id+"F0.imprint","IMPRINT",EDGE,{"disambiguationData":[TD([[subQ2,-1.0]])],"derivedFrom":subQ0}),makeQuery(id+"F0.imprint","IMPRINT",EDGE,{"disambiguationData":[TD([[subQ1,-1.0]])],"derivedFrom":subQ0})])],"isStart":true})])]})]});}
            var Q4;
            {var subQ0=sQuery(id+"F0.wireOp",EDGE,"E4.0");var subQ1=makeQuery(id+"F0.imprint","INTERSECT",VERTEX,{"disambiguationData":[OD(0.0)],"derivedFrom":[subQ0,sQuery(id+"F0.wireOp",EDGE,"E6.8.0")]});var subQ2=sQuery(id+"F0.wireOp",EDGE,"E6.8.1");var subQ3=makeQuery(id+"F0.imprint","INTERSECT",VERTEX,{"disambiguationData":[OD(0.0)],"derivedFrom":[subQ0,subQ2]});var subQ4=makeQuery(id+"F0.imprint","INTERSECT",VERTEX,{"disambiguationData":[OD(1.0)],"derivedFrom":[subQ0,sQuery(id+"F0.wireOp",EDGE,"E6.9.0")]});Q4=makeQuery(id+"F5.opFillet","BLEND_EDGE",EDGE,{"blendedFrom":[makeQuery(id+"F1.opExtrude","CAP_EDGE",EDGE,{"disambiguationData":[OSD([subQ2]),TDD([makeQuery(id+"F0.imprint","IMPRINT",EDGE,{"disambiguationData":[TD([[subQ3,1.0]])],"derivedFrom":subQ2})])],"isStart":false}),makeQuery(id+"F2.opFillet","BLEND_FACE",FACE,{"disambiguationData":[OSD([subQ0]),TDD([makeQuery(id+"F1.opExtrude","CAP_EDGE",EDGE,{"disambiguationData":[OSD([subQ0]),TDD([makeQuery(id+"F0.imprint","IMPRINT",EDGE,{"disambiguationData":[TD([[makeQuery(id+"F0.imprint","INTERSECT",VERTEX,{"disambiguationData":[OD(1.0)],"derivedFrom":[subQ0,sQuery(id+"F0.wireOp",EDGE,"E6.9.1")]}),-1.0]])],"derivedFrom":subQ0}),makeQuery(id+"F0.imprint","IMPRINT",EDGE,{"disambiguationData":[TD([[subQ4,-1.0]])],"derivedFrom":subQ0}),makeQuery(id+"F0.imprint","IMPRINT",EDGE,{"disambiguationData":[TD([[subQ1,-1.0]])],"derivedFrom":subQ0})])],"isStart":true})])]})],"blendedInto":[makeQuery(id+"F2.opFillet","BLEND_FACE",FACE,{"disambiguationData":[OSD([subQ0]),TDD([makeQuery(id+"F1.opExtrude","CAP_EDGE",EDGE,{"disambiguationData":[OSD([subQ0]),TDD([makeQuery(id+"F0.imprint","IMPRINT",EDGE,{"disambiguationData":[TD([[makeQuery(id+"F0.imprint","INTERSECT",VERTEX,{"disambiguationData":[OD(1.0)],"derivedFrom":[subQ0,sQuery(id+"F0.wireOp",EDGE,"E6.9.1")]}),-1.0]])],"derivedFrom":subQ0}),makeQuery(id+"F0.imprint","IMPRINT",EDGE,{"disambiguationData":[TD([[subQ4,-1.0]])],"derivedFrom":subQ0}),makeQuery(id+"F0.imprint","IMPRINT",EDGE,{"disambiguationData":[TD([[subQ1,-1.0]])],"derivedFrom":subQ0})])],"isStart":true})])]})]});}
            var Q5;
            {var subQ0=sQuery(id+"F0.wireOp",EDGE,"E4.0");var subQ1=makeQuery(id+"F0.imprint","INTERSECT",VERTEX,{"disambiguationData":[OD(0.0)],"derivedFrom":[subQ0,sQuery(id+"F0.wireOp",EDGE,"E6.7.0")]});var subQ2=sQuery(id+"F0.wireOp",EDGE,"E6.7.1");var subQ3=makeQuery(id+"F0.imprint","INTERSECT",VERTEX,{"disambiguationData":[OD(0.0)],"derivedFrom":[subQ0,subQ2]});var subQ4=makeQuery(id+"F0.imprint","INTERSECT",VERTEX,{"disambiguationData":[OD(1.0)],"derivedFrom":[subQ0,sQuery(id+"F0.wireOp",EDGE,"E6.8.0")]});Q5=makeQuery(id+"F5.opFillet","BLEND_EDGE",EDGE,{"blendedFrom":[makeQuery(id+"F1.opExtrude","CAP_EDGE",EDGE,{"disambiguationData":[OSD([subQ2]),TDD([makeQuery(id+"F0.imprint","IMPRINT",EDGE,{"disambiguationData":[TD([[subQ3,1.0]])],"derivedFrom":subQ2})])],"isStart":false}),makeQuery(id+"F2.opFillet","BLEND_FACE",FACE,{"disambiguationData":[OSD([subQ0]),TDD([makeQuery(id+"F1.opExtrude","CAP_EDGE",EDGE,{"disambiguationData":[OSD([subQ0]),TDD([makeQuery(id+"F0.imprint","IMPRINT",EDGE,{"disambiguationData":[TD([[makeQuery(id+"F0.imprint","INTERSECT",VERTEX,{"disambiguationData":[OD(1.0)],"derivedFrom":[subQ0,sQuery(id+"F0.wireOp",EDGE,"E6.8.1")]}),-1.0]])],"derivedFrom":subQ0}),makeQuery(id+"F0.imprint","IMPRINT",EDGE,{"disambiguationData":[TD([[subQ4,-1.0]])],"derivedFrom":subQ0}),makeQuery(id+"F0.imprint","IMPRINT",EDGE,{"disambiguationData":[TD([[subQ1,-1.0]])],"derivedFrom":subQ0})])],"isStart":true})])]})],"blendedInto":[makeQuery(id+"F2.opFillet","BLEND_FACE",FACE,{"disambiguationData":[OSD([subQ0]),TDD([makeQuery(id+"F1.opExtrude","CAP_EDGE",EDGE,{"disambiguationData":[OSD([subQ0]),TDD([makeQuery(id+"F0.imprint","IMPRINT",EDGE,{"disambiguationData":[TD([[makeQuery(id+"F0.imprint","INTERSECT",VERTEX,{"disambiguationData":[OD(1.0)],"derivedFrom":[subQ0,sQuery(id+"F0.wireOp",EDGE,"E6.8.1")]}),-1.0]])],"derivedFrom":subQ0}),makeQuery(id+"F0.imprint","IMPRINT",EDGE,{"disambiguationData":[TD([[subQ4,-1.0]])],"derivedFrom":subQ0}),makeQuery(id+"F0.imprint","IMPRINT",EDGE,{"disambiguationData":[TD([[subQ1,-1.0]])],"derivedFrom":subQ0})])],"isStart":true})])]})]});}
            var Q6;
            {var subQ0=sQuery(id+"F0.wireOp",EDGE,"E4.0");var subQ1=makeQuery(id+"F0.imprint","INTERSECT",VERTEX,{"disambiguationData":[OD(0.0)],"derivedFrom":[subQ0,sQuery(id+"F0.wireOp",EDGE,"E6.6.0")]});var subQ2=makeQuery(id+"F0.imprint","INTERSECT",VERTEX,{"disambiguationData":[OD(1.0)],"derivedFrom":[subQ0,sQuery(id+"F0.wireOp",EDGE,"E6.7.0")]});var subQ3=sQuery(id+"F0.wireOp",EDGE,"E6.7.1");var subQ4=makeQuery(id+"F0.imprint","INTERSECT",VERTEX,{"disambiguationData":[OD(1.0)],"derivedFrom":[subQ0,subQ3]});Q6=makeQuery(id+"F5.opFillet","BLEND_EDGE",EDGE,{"blendedFrom":[makeQuery(id+"F1.opExtrude","CAP_EDGE",EDGE,{"disambiguationData":[OSD([subQ3]),TDD([makeQuery(id+"F0.imprint","IMPRINT",EDGE,{"disambiguationData":[TD([[makeQuery(id+"F0.imprint","INTERSECT",VERTEX,{"disambiguationData":[OD(0.0)],"derivedFrom":[subQ0,subQ3]}),1.0]])],"derivedFrom":subQ3})])],"isStart":false}),makeQuery(id+"F2.opFillet","BLEND_FACE",FACE,{"disambiguationData":[OSD([subQ0]),TDD([makeQuery(id+"F1.opExtrude","CAP_EDGE",EDGE,{"disambiguationData":[OSD([subQ0]),TDD([makeQuery(id+"F0.imprint","IMPRINT",EDGE,{"disambiguationData":[TD([[subQ4,-1.0]])],"derivedFrom":subQ0}),makeQuery(id+"F0.imprint","IMPRINT",EDGE,{"disambiguationData":[TD([[subQ2,-1.0]])],"derivedFrom":subQ0}),makeQuery(id+"F0.imprint","IMPRINT",EDGE,{"disambiguationData":[TD([[subQ1,-1.0]])],"derivedFrom":subQ0})])],"isStart":true})])]})],"blendedInto":[makeQuery(id+"F2.opFillet","BLEND_FACE",FACE,{"disambiguationData":[OSD([subQ0]),TDD([makeQuery(id+"F1.opExtrude","CAP_EDGE",EDGE,{"disambiguationData":[OSD([subQ0]),TDD([makeQuery(id+"F0.imprint","IMPRINT",EDGE,{"disambiguationData":[TD([[subQ4,-1.0]])],"derivedFrom":subQ0}),makeQuery(id+"F0.imprint","IMPRINT",EDGE,{"disambiguationData":[TD([[subQ2,-1.0]])],"derivedFrom":subQ0}),makeQuery(id+"F0.imprint","IMPRINT",EDGE,{"disambiguationData":[TD([[subQ1,-1.0]])],"derivedFrom":subQ0})])],"isStart":true})])]})]});}
            var Q7;
            {var subQ0=sQuery(id+"F0.wireOp",EDGE,"E4.0");var subQ1=makeQuery(id+"F0.imprint","INTERSECT",VERTEX,{"disambiguationData":[OD(0.0)],"derivedFrom":[subQ0,sQuery(id+"F0.wireOp",EDGE,"E6.5.0")]});var subQ2=makeQuery(id+"F0.imprint","INTERSECT",VERTEX,{"disambiguationData":[OD(1.0)],"derivedFrom":[subQ0,sQuery(id+"F0.wireOp",EDGE,"E6.6.0")]});var subQ3=sQuery(id+"F0.wireOp",EDGE,"E6.6.1");var subQ4=makeQuery(id+"F0.imprint","INTERSECT",VERTEX,{"disambiguationData":[OD(1.0)],"derivedFrom":[subQ0,subQ3]});Q7=makeQuery(id+"F5.opFillet","BLEND_EDGE",EDGE,{"blendedFrom":[makeQuery(id+"F1.opExtrude","CAP_EDGE",EDGE,{"disambiguationData":[OSD([subQ3]),TDD([makeQuery(id+"F0.imprint","IMPRINT",EDGE,{"disambiguationData":[TD([[makeQuery(id+"F0.imprint","INTERSECT",VERTEX,{"disambiguationData":[OD(0.0)],"derivedFrom":[subQ0,subQ3]}),1.0]])],"derivedFrom":subQ3})])],"isStart":false}),makeQuery(id+"F2.opFillet","BLEND_FACE",FACE,{"disambiguationData":[OSD([subQ0]),TDD([makeQuery(id+"F1.opExtrude","CAP_EDGE",EDGE,{"disambiguationData":[OSD([subQ0]),TDD([makeQuery(id+"F0.imprint","IMPRINT",EDGE,{"disambiguationData":[TD([[subQ4,-1.0]])],"derivedFrom":subQ0}),makeQuery(id+"F0.imprint","IMPRINT",EDGE,{"disambiguationData":[TD([[subQ2,-1.0]])],"derivedFrom":subQ0}),makeQuery(id+"F0.imprint","IMPRINT",EDGE,{"disambiguationData":[TD([[subQ1,-1.0]])],"derivedFrom":subQ0})])],"isStart":true})])]})],"blendedInto":[makeQuery(id+"F2.opFillet","BLEND_FACE",FACE,{"disambiguationData":[OSD([subQ0]),TDD([makeQuery(id+"F1.opExtrude","CAP_EDGE",EDGE,{"disambiguationData":[OSD([subQ0]),TDD([makeQuery(id+"F0.imprint","IMPRINT",EDGE,{"disambiguationData":[TD([[subQ4,-1.0]])],"derivedFrom":subQ0}),makeQuery(id+"F0.imprint","IMPRINT",EDGE,{"disambiguationData":[TD([[subQ2,-1.0]])],"derivedFrom":subQ0}),makeQuery(id+"F0.imprint","IMPRINT",EDGE,{"disambiguationData":[TD([[subQ1,-1.0]])],"derivedFrom":subQ0})])],"isStart":true})])]})]});}
            var Q8;
            {var subQ0=sQuery(id+"F0.wireOp",EDGE,"E4.0");var subQ1=makeQuery(id+"F0.imprint","INTERSECT",VERTEX,{"disambiguationData":[OD(0.0)],"derivedFrom":[subQ0,sQuery(id+"F0.wireOp",EDGE,"E6.11.0")]});var subQ2=sQuery(id+"F0.wireOp",EDGE,"E6.11.1");var subQ3=makeQuery(id+"F0.imprint","INTERSECT",VERTEX,{"disambiguationData":[OD(0.0)],"derivedFrom":[subQ0,subQ2]});var subQ4=makeQuery(id+"F0.imprint","INTERSECT",VERTEX,{"disambiguationData":[OD(0.0)],"derivedFrom":[sQuery(id+"F0.wireOp",EDGE,"E2.0"),subQ0]});Q8=makeQuery(id+"F5.opFillet","BLEND_EDGE",EDGE,{"blendedFrom":[makeQuery(id+"F1.opExtrude","CAP_EDGE",EDGE,{"disambiguationData":[OSD([subQ2]),TDD([makeQuery(id+"F0.imprint","IMPRINT",EDGE,{"disambiguationData":[TD([[subQ3,1.0]])],"derivedFrom":subQ2})])],"isStart":false}),makeQuery(id+"F2.opFillet","BLEND_FACE",FACE,{"disambiguationData":[OSD([subQ0]),TDD([makeQuery(id+"F1.opExtrude","CAP_EDGE",EDGE,{"disambiguationData":[OSD([subQ0]),TDD([makeQuery(id+"F0.imprint","IMPRINT",EDGE,{"disambiguationData":[TD([[subQ4,1.0]])],"derivedFrom":subQ0}),makeQuery(id+"F0.imprint","IMPRINT",EDGE,{"disambiguationData":[TD([[subQ4,-1.0]])],"derivedFrom":subQ0}),makeQuery(id+"F0.imprint","IMPRINT",EDGE,{"disambiguationData":[TD([[subQ1,-1.0]])],"derivedFrom":subQ0})])],"isStart":true})])]})],"blendedInto":[makeQuery(id+"F2.opFillet","BLEND_FACE",FACE,{"disambiguationData":[OSD([subQ0]),TDD([makeQuery(id+"F1.opExtrude","CAP_EDGE",EDGE,{"disambiguationData":[OSD([subQ0]),TDD([makeQuery(id+"F0.imprint","IMPRINT",EDGE,{"disambiguationData":[TD([[subQ4,1.0]])],"derivedFrom":subQ0}),makeQuery(id+"F0.imprint","IMPRINT",EDGE,{"disambiguationData":[TD([[subQ4,-1.0]])],"derivedFrom":subQ0}),makeQuery(id+"F0.imprint","IMPRINT",EDGE,{"disambiguationData":[TD([[subQ1,-1.0]])],"derivedFrom":subQ0})])],"isStart":true})])]})]});}
            var Q9;
            {var subQ0=sQuery(id+"F0.wireOp",EDGE,"E4.0");var subQ1=makeQuery(id+"F0.imprint","INTERSECT",VERTEX,{"disambiguationData":[OD(0.0)],"derivedFrom":[subQ0,sQuery(id+"F0.wireOp",EDGE,"E6.10.0")]});var subQ2=makeQuery(id+"F0.imprint","INTERSECT",VERTEX,{"disambiguationData":[OD(1.0)],"derivedFrom":[subQ0,sQuery(id+"F0.wireOp",EDGE,"E6.11.0")]});var subQ3=sQuery(id+"F0.wireOp",EDGE,"E6.11.1");var subQ4=makeQuery(id+"F0.imprint","INTERSECT",VERTEX,{"disambiguationData":[OD(1.0)],"derivedFrom":[subQ0,subQ3]});Q9=makeQuery(id+"F5.opFillet","BLEND_EDGE",EDGE,{"blendedFrom":[makeQuery(id+"F1.opExtrude","CAP_EDGE",EDGE,{"disambiguationData":[OSD([subQ3]),TDD([makeQuery(id+"F0.imprint","IMPRINT",EDGE,{"disambiguationData":[TD([[makeQuery(id+"F0.imprint","INTERSECT",VERTEX,{"disambiguationData":[OD(0.0)],"derivedFrom":[subQ0,subQ3]}),1.0]])],"derivedFrom":subQ3})])],"isStart":false}),makeQuery(id+"F2.opFillet","BLEND_FACE",FACE,{"disambiguationData":[OSD([subQ0]),TDD([makeQuery(id+"F1.opExtrude","CAP_EDGE",EDGE,{"disambiguationData":[OSD([subQ0]),TDD([makeQuery(id+"F0.imprint","IMPRINT",EDGE,{"disambiguationData":[TD([[subQ4,-1.0]])],"derivedFrom":subQ0}),makeQuery(id+"F0.imprint","IMPRINT",EDGE,{"disambiguationData":[TD([[subQ2,-1.0]])],"derivedFrom":subQ0}),makeQuery(id+"F0.imprint","IMPRINT",EDGE,{"disambiguationData":[TD([[subQ1,-1.0]])],"derivedFrom":subQ0})])],"isStart":true})])]})],"blendedInto":[makeQuery(id+"F2.opFillet","BLEND_FACE",FACE,{"disambiguationData":[OSD([subQ0]),TDD([makeQuery(id+"F1.opExtrude","CAP_EDGE",EDGE,{"disambiguationData":[OSD([subQ0]),TDD([makeQuery(id+"F0.imprint","IMPRINT",EDGE,{"disambiguationData":[TD([[subQ4,-1.0]])],"derivedFrom":subQ0}),makeQuery(id+"F0.imprint","IMPRINT",EDGE,{"disambiguationData":[TD([[subQ2,-1.0]])],"derivedFrom":subQ0}),makeQuery(id+"F0.imprint","IMPRINT",EDGE,{"disambiguationData":[TD([[subQ1,-1.0]])],"derivedFrom":subQ0})])],"isStart":true})])]})]});}
            var Q10;
            {var subQ0=sQuery(id+"F0.wireOp",EDGE,"E4.0");var subQ1=makeQuery(id+"F0.imprint","INTERSECT",VERTEX,{"disambiguationData":[OD(1.0)],"derivedFrom":[sQuery(id+"F0.wireOp",EDGE,"E2.0"),subQ0]});var subQ2=sQuery(id+"F0.wireOp",EDGE,"E5.0");var subQ3=makeQuery(id+"F0.imprint","INTERSECT",VERTEX,{"disambiguationData":[OD(0.0)],"derivedFrom":[subQ0,subQ2]});Q10=makeQuery(id+"F5.opFillet","BLEND_EDGE",EDGE,{"blendedFrom":[makeQuery(id+"F1.opExtrude","CAP_EDGE",EDGE,{"disambiguationData":[OSD([subQ2]),TDD([makeQuery(id+"F0.imprint","IMPRINT",EDGE,{"disambiguationData":[TD([[subQ3,1.0]])],"derivedFrom":subQ2})])],"isStart":false}),makeQuery(id+"F2.opFillet","BLEND_FACE",FACE,{"disambiguationData":[OSD([subQ0]),TDD([makeQuery(id+"F1.opExtrude","CAP_EDGE",EDGE,{"disambiguationData":[OSD([subQ0]),TDD([makeQuery(id+"F0.imprint","IMPRINT",EDGE,{"disambiguationData":[TD([[makeQuery(id+"F0.imprint","INTERSECT",VERTEX,{"disambiguationData":[OD(1.0)],"derivedFrom":[subQ0,sQuery(id+"F0.wireOp",EDGE,"E6.1.1")]}),-1.0]])],"derivedFrom":subQ0}),makeQuery(id+"F0.imprint","IMPRINT",EDGE,{"disambiguationData":[TD([[subQ1,1.0]])],"derivedFrom":subQ0}),makeQuery(id+"F0.imprint","IMPRINT",EDGE,{"disambiguationData":[TD([[subQ1,-1.0]])],"derivedFrom":subQ0})])],"isStart":true})])]})],"blendedInto":[makeQuery(id+"F2.opFillet","BLEND_FACE",FACE,{"disambiguationData":[OSD([subQ0]),TDD([makeQuery(id+"F1.opExtrude","CAP_EDGE",EDGE,{"disambiguationData":[OSD([subQ0]),TDD([makeQuery(id+"F0.imprint","IMPRINT",EDGE,{"disambiguationData":[TD([[makeQuery(id+"F0.imprint","INTERSECT",VERTEX,{"disambiguationData":[OD(1.0)],"derivedFrom":[subQ0,sQuery(id+"F0.wireOp",EDGE,"E6.1.1")]}),-1.0]])],"derivedFrom":subQ0}),makeQuery(id+"F0.imprint","IMPRINT",EDGE,{"disambiguationData":[TD([[subQ1,1.0]])],"derivedFrom":subQ0}),makeQuery(id+"F0.imprint","IMPRINT",EDGE,{"disambiguationData":[TD([[subQ1,-1.0]])],"derivedFrom":subQ0})])],"isStart":true})])]})]});}
            var Q11;
            {var subQ0=sQuery(id+"F0.wireOp",EDGE,"E4.0");var subQ1=makeQuery(id+"F0.imprint","INTERSECT",VERTEX,{"disambiguationData":[OD(0.0)],"derivedFrom":[subQ0,sQuery(id+"F0.wireOp",EDGE,"E6.11.0")]});var subQ2=makeQuery(id+"F0.imprint","INTERSECT",VERTEX,{"disambiguationData":[OD(0.0)],"derivedFrom":[sQuery(id+"F0.wireOp",EDGE,"E2.0"),subQ0]});var subQ3=sQuery(id+"F0.wireOp",EDGE,"E5.0");Q11=makeQuery(id+"F5.opFillet","BLEND_EDGE",EDGE,{"blendedFrom":[makeQuery(id+"F1.opExtrude","CAP_EDGE",EDGE,{"disambiguationData":[OSD([subQ3]),TDD([makeQuery(id+"F0.imprint","IMPRINT",EDGE,{"disambiguationData":[TD([[makeQuery(id+"F0.imprint","INTERSECT",VERTEX,{"disambiguationData":[OD(0.0)],"derivedFrom":[subQ0,subQ3]}),1.0]])],"derivedFrom":subQ3})])],"isStart":false}),makeQuery(id+"F2.opFillet","BLEND_FACE",FACE,{"disambiguationData":[OSD([subQ0]),TDD([makeQuery(id+"F1.opExtrude","CAP_EDGE",EDGE,{"disambiguationData":[OSD([subQ0]),TDD([makeQuery(id+"F0.imprint","IMPRINT",EDGE,{"disambiguationData":[TD([[subQ2,1.0]])],"derivedFrom":subQ0}),makeQuery(id+"F0.imprint","IMPRINT",EDGE,{"disambiguationData":[TD([[subQ2,-1.0]])],"derivedFrom":subQ0}),makeQuery(id+"F0.imprint","IMPRINT",EDGE,{"disambiguationData":[TD([[subQ1,-1.0]])],"derivedFrom":subQ0})])],"isStart":true})])]})],"blendedInto":[makeQuery(id+"F2.opFillet","BLEND_FACE",FACE,{"disambiguationData":[OSD([subQ0]),TDD([makeQuery(id+"F1.opExtrude","CAP_EDGE",EDGE,{"disambiguationData":[OSD([subQ0]),TDD([makeQuery(id+"F0.imprint","IMPRINT",EDGE,{"disambiguationData":[TD([[subQ2,1.0]])],"derivedFrom":subQ0}),makeQuery(id+"F0.imprint","IMPRINT",EDGE,{"disambiguationData":[TD([[subQ2,-1.0]])],"derivedFrom":subQ0}),makeQuery(id+"F0.imprint","IMPRINT",EDGE,{"disambiguationData":[TD([[subQ1,-1.0]])],"derivedFrom":subQ0})])],"isStart":true})])]})]});}
            var Q12;
            {var subQ0=sQuery(id+"F0.wireOp",EDGE,"E4.0");var subQ1=makeQuery(id+"F0.imprint","INTERSECT",VERTEX,{"disambiguationData":[OD(0.0)],"derivedFrom":[subQ0,sQuery(id+"F0.wireOp",EDGE,"E6.1.0")]});var subQ2=sQuery(id+"F0.wireOp",EDGE,"E6.1.1");var subQ3=makeQuery(id+"F0.imprint","INTERSECT",VERTEX,{"disambiguationData":[OD(0.0)],"derivedFrom":[subQ0,subQ2]});var subQ4=makeQuery(id+"F0.imprint","INTERSECT",VERTEX,{"disambiguationData":[OD(1.0)],"derivedFrom":[subQ0,sQuery(id+"F0.wireOp",EDGE,"E6.2.0")]});Q12=makeQuery(id+"F5.opFillet","BLEND_EDGE",EDGE,{"blendedFrom":[makeQuery(id+"F1.opExtrude","CAP_EDGE",EDGE,{"disambiguationData":[OSD([subQ2]),TDD([makeQuery(id+"F0.imprint","IMPRINT",EDGE,{"disambiguationData":[TD([[subQ3,1.0]])],"derivedFrom":subQ2})])],"isStart":false}),makeQuery(id+"F2.opFillet","BLEND_FACE",FACE,{"disambiguationData":[OSD([subQ0]),TDD([makeQuery(id+"F1.opExtrude","CAP_EDGE",EDGE,{"disambiguationData":[OSD([subQ0]),TDD([makeQuery(id+"F0.imprint","IMPRINT",EDGE,{"disambiguationData":[TD([[makeQuery(id+"F0.imprint","INTERSECT",VERTEX,{"disambiguationData":[OD(1.0)],"derivedFrom":[subQ0,sQuery(id+"F0.wireOp",EDGE,"E6.2.1")]}),-1.0]])],"derivedFrom":subQ0}),makeQuery(id+"F0.imprint","IMPRINT",EDGE,{"disambiguationData":[TD([[subQ4,-1.0]])],"derivedFrom":subQ0}),makeQuery(id+"F0.imprint","IMPRINT",EDGE,{"disambiguationData":[TD([[subQ1,-1.0]])],"derivedFrom":subQ0})])],"isStart":true})])]})],"blendedInto":[makeQuery(id+"F2.opFillet","BLEND_FACE",FACE,{"disambiguationData":[OSD([subQ0]),TDD([makeQuery(id+"F1.opExtrude","CAP_EDGE",EDGE,{"disambiguationData":[OSD([subQ0]),TDD([makeQuery(id+"F0.imprint","IMPRINT",EDGE,{"disambiguationData":[TD([[makeQuery(id+"F0.imprint","INTERSECT",VERTEX,{"disambiguationData":[OD(1.0)],"derivedFrom":[subQ0,sQuery(id+"F0.wireOp",EDGE,"E6.2.1")]}),-1.0]])],"derivedFrom":subQ0}),makeQuery(id+"F0.imprint","IMPRINT",EDGE,{"disambiguationData":[TD([[subQ4,-1.0]])],"derivedFrom":subQ0}),makeQuery(id+"F0.imprint","IMPRINT",EDGE,{"disambiguationData":[TD([[subQ1,-1.0]])],"derivedFrom":subQ0})])],"isStart":true})])]})]});}
            var Q13;
            {var subQ0=sQuery(id+"F0.wireOp",EDGE,"E4.0");var subQ1=makeQuery(id+"F0.imprint","INTERSECT",VERTEX,{"disambiguationData":[OD(1.0)],"derivedFrom":[sQuery(id+"F0.wireOp",EDGE,"E2.0"),subQ0]});var subQ3=sQuery(id+"F0.wireOp",EDGE,"E6.1.1");var subQ4=makeQuery(id+"F0.imprint","INTERSECT",VERTEX,{"disambiguationData":[OD(1.0)],"derivedFrom":[subQ0,subQ3]});Q13=makeQuery(id+"F5.opFillet","BLEND_EDGE",EDGE,{"blendedFrom":[makeQuery(id+"F1.opExtrude","CAP_EDGE",EDGE,{"disambiguationData":[OSD([subQ3]),TDD([makeQuery(id+"F0.imprint","IMPRINT",EDGE,{"disambiguationData":[TD([[makeQuery(id+"F0.imprint","INTERSECT",VERTEX,{"disambiguationData":[OD(0.0)],"derivedFrom":[subQ0,subQ3]}),1.0]])],"derivedFrom":subQ3})])],"isStart":false}),makeQuery(id+"F2.opFillet","BLEND_FACE",FACE,{"disambiguationData":[OSD([subQ0]),TDD([makeQuery(id+"F1.opExtrude","CAP_EDGE",EDGE,{"disambiguationData":[OSD([subQ0]),TDD([makeQuery(id+"F0.imprint","IMPRINT",EDGE,{"disambiguationData":[TD([[subQ4,-1.0]])],"derivedFrom":subQ0}),makeQuery(id+"F0.imprint","IMPRINT",EDGE,{"disambiguationData":[TD([[subQ1,1.0]])],"derivedFrom":subQ0}),makeQuery(id+"F0.imprint","IMPRINT",EDGE,{"disambiguationData":[TD([[subQ1,-1.0]])],"derivedFrom":subQ0})])],"isStart":true})])]})],"blendedInto":[makeQuery(id+"F2.opFillet","BLEND_FACE",FACE,{"disambiguationData":[OSD([subQ0]),TDD([makeQuery(id+"F1.opExtrude","CAP_EDGE",EDGE,{"disambiguationData":[OSD([subQ0]),TDD([makeQuery(id+"F0.imprint","IMPRINT",EDGE,{"disambiguationData":[TD([[subQ4,-1.0]])],"derivedFrom":subQ0}),makeQuery(id+"F0.imprint","IMPRINT",EDGE,{"disambiguationData":[TD([[subQ1,1.0]])],"derivedFrom":subQ0}),makeQuery(id+"F0.imprint","IMPRINT",EDGE,{"disambiguationData":[TD([[subQ1,-1.0]])],"derivedFrom":subQ0})])],"isStart":true})])]})]});}
            var Q14;
            {var subQ0=sQuery(id+"F0.wireOp",EDGE,"E4.0");var subQ1=makeQuery(id+"F0.imprint","INTERSECT",VERTEX,{"disambiguationData":[OD(0.0)],"derivedFrom":[subQ0,sQuery(id+"F0.wireOp",EDGE,"E6.2.0")]});var subQ2=sQuery(id+"F0.wireOp",EDGE,"E6.2.1");var subQ3=makeQuery(id+"F0.imprint","INTERSECT",VERTEX,{"disambiguationData":[OD(0.0)],"derivedFrom":[subQ0,subQ2]});var subQ4=makeQuery(id+"F0.imprint","INTERSECT",VERTEX,{"disambiguationData":[OD(0.0)],"derivedFrom":[subQ0,sQuery(id+"F0.wireOp",EDGE,"E6.3.0")]});Q14=makeQuery(id+"F5.opFillet","BLEND_EDGE",EDGE,{"blendedFrom":[makeQuery(id+"F1.opExtrude","CAP_EDGE",EDGE,{"disambiguationData":[OSD([subQ2]),TDD([makeQuery(id+"F0.imprint","IMPRINT",EDGE,{"disambiguationData":[TD([[subQ3,1.0]])],"derivedFrom":subQ2})])],"isStart":false}),makeQuery(id+"F2.opFillet","BLEND_FACE",FACE,{"disambiguationData":[OSD([subQ0]),TDD([makeQuery(id+"F1.opExtrude","CAP_EDGE",EDGE,{"disambiguationData":[OSD([subQ0]),TDD([makeQuery(id+"F0.imprint","IMPRINT",EDGE,{"disambiguationData":[TD([[subQ4,1.0]])],"derivedFrom":subQ0}),makeQuery(id+"F0.imprint","IMPRINT",EDGE,{"disambiguationData":[TD([[subQ4,-1.0]])],"derivedFrom":subQ0}),makeQuery(id+"F0.imprint","IMPRINT",EDGE,{"disambiguationData":[TD([[subQ1,-1.0]])],"derivedFrom":subQ0})])],"isStart":true})])]})],"blendedInto":[makeQuery(id+"F2.opFillet","BLEND_FACE",FACE,{"disambiguationData":[OSD([subQ0]),TDD([makeQuery(id+"F1.opExtrude","CAP_EDGE",EDGE,{"disambiguationData":[OSD([subQ0]),TDD([makeQuery(id+"F0.imprint","IMPRINT",EDGE,{"disambiguationData":[TD([[subQ4,1.0]])],"derivedFrom":subQ0}),makeQuery(id+"F0.imprint","IMPRINT",EDGE,{"disambiguationData":[TD([[subQ4,-1.0]])],"derivedFrom":subQ0}),makeQuery(id+"F0.imprint","IMPRINT",EDGE,{"disambiguationData":[TD([[subQ1,-1.0]])],"derivedFrom":subQ0})])],"isStart":true})])]})]});}
            var Q15;
            {var subQ0=sQuery(id+"F0.wireOp",EDGE,"E4.0");var subQ1=makeQuery(id+"F0.imprint","INTERSECT",VERTEX,{"disambiguationData":[OD(0.0)],"derivedFrom":[subQ0,sQuery(id+"F0.wireOp",EDGE,"E6.1.0")]});var subQ2=makeQuery(id+"F0.imprint","INTERSECT",VERTEX,{"disambiguationData":[OD(1.0)],"derivedFrom":[subQ0,sQuery(id+"F0.wireOp",EDGE,"E6.2.0")]});var subQ3=sQuery(id+"F0.wireOp",EDGE,"E6.2.1");var subQ4=makeQuery(id+"F0.imprint","INTERSECT",VERTEX,{"disambiguationData":[OD(1.0)],"derivedFrom":[subQ0,subQ3]});Q15=makeQuery(id+"F5.opFillet","BLEND_EDGE",EDGE,{"blendedFrom":[makeQuery(id+"F1.opExtrude","CAP_EDGE",EDGE,{"disambiguationData":[OSD([subQ3]),TDD([makeQuery(id+"F0.imprint","IMPRINT",EDGE,{"disambiguationData":[TD([[makeQuery(id+"F0.imprint","INTERSECT",VERTEX,{"disambiguationData":[OD(0.0)],"derivedFrom":[subQ0,subQ3]}),1.0]])],"derivedFrom":subQ3})])],"isStart":false}),makeQuery(id+"F2.opFillet","BLEND_FACE",FACE,{"disambiguationData":[OSD([subQ0]),TDD([makeQuery(id+"F1.opExtrude","CAP_EDGE",EDGE,{"disambiguationData":[OSD([subQ0]),TDD([makeQuery(id+"F0.imprint","IMPRINT",EDGE,{"disambiguationData":[TD([[subQ4,-1.0]])],"derivedFrom":subQ0}),makeQuery(id+"F0.imprint","IMPRINT",EDGE,{"disambiguationData":[TD([[subQ2,-1.0]])],"derivedFrom":subQ0}),makeQuery(id+"F0.imprint","IMPRINT",EDGE,{"disambiguationData":[TD([[subQ1,-1.0]])],"derivedFrom":subQ0})])],"isStart":true})])]})],"blendedInto":[makeQuery(id+"F2.opFillet","BLEND_FACE",FACE,{"disambiguationData":[OSD([subQ0]),TDD([makeQuery(id+"F1.opExtrude","CAP_EDGE",EDGE,{"disambiguationData":[OSD([subQ0]),TDD([makeQuery(id+"F0.imprint","IMPRINT",EDGE,{"disambiguationData":[TD([[subQ4,-1.0]])],"derivedFrom":subQ0}),makeQuery(id+"F0.imprint","IMPRINT",EDGE,{"disambiguationData":[TD([[subQ2,-1.0]])],"derivedFrom":subQ0}),makeQuery(id+"F0.imprint","IMPRINT",EDGE,{"disambiguationData":[TD([[subQ1,-1.0]])],"derivedFrom":subQ0})])],"isStart":true})])]})]});}
            var Q16;
            {var subQ0=sQuery(id+"F0.wireOp",EDGE,"E4.0");var subQ1=makeQuery(id+"F0.imprint","INTERSECT",VERTEX,{"disambiguationData":[OD(1.0)],"derivedFrom":[subQ0,sQuery(id+"F0.wireOp",EDGE,"E6.3.0")]});var subQ2=sQuery(id+"F0.wireOp",EDGE,"E6.3.1");var subQ4=makeQuery(id+"F0.imprint","INTERSECT",VERTEX,{"disambiguationData":[OD(1.0)],"derivedFrom":[subQ0,sQuery(id+"F0.wireOp",EDGE,"E6.4.0")]});Q16=makeQuery(id+"F5.opFillet","BLEND_EDGE",EDGE,{"blendedFrom":[makeQuery(id+"F1.opExtrude","CAP_EDGE",EDGE,{"disambiguationData":[OSD([subQ2]),TDD([makeQuery(id+"F0.imprint","IMPRINT",EDGE,{"disambiguationData":[TD([[makeQuery(id+"F0.imprint","INTERSECT",VERTEX,{"disambiguationData":[OD(0.0)],"derivedFrom":[subQ0,subQ2]}),-1.0]])],"derivedFrom":subQ2})])],"isStart":false}),makeQuery(id+"F2.opFillet","BLEND_FACE",FACE,{"disambiguationData":[OSD([subQ0]),TDD([makeQuery(id+"F1.opExtrude","CAP_EDGE",EDGE,{"disambiguationData":[OSD([subQ0]),TDD([makeQuery(id+"F0.imprint","IMPRINT",EDGE,{"disambiguationData":[TD([[makeQuery(id+"F0.imprint","INTERSECT",VERTEX,{"disambiguationData":[OD(1.0)],"derivedFrom":[subQ0,sQuery(id+"F0.wireOp",EDGE,"E6.4.1")]}),-1.0]])],"derivedFrom":subQ0}),makeQuery(id+"F0.imprint","IMPRINT",EDGE,{"disambiguationData":[TD([[subQ4,-1.0]])],"derivedFrom":subQ0}),makeQuery(id+"F0.imprint","IMPRINT",EDGE,{"disambiguationData":[TD([[subQ1,-1.0]])],"derivedFrom":subQ0})])],"isStart":true})])]})],"blendedInto":[makeQuery(id+"F2.opFillet","BLEND_FACE",FACE,{"disambiguationData":[OSD([subQ0]),TDD([makeQuery(id+"F1.opExtrude","CAP_EDGE",EDGE,{"disambiguationData":[OSD([subQ0]),TDD([makeQuery(id+"F0.imprint","IMPRINT",EDGE,{"disambiguationData":[TD([[makeQuery(id+"F0.imprint","INTERSECT",VERTEX,{"disambiguationData":[OD(1.0)],"derivedFrom":[subQ0,sQuery(id+"F0.wireOp",EDGE,"E6.4.1")]}),-1.0]])],"derivedFrom":subQ0}),makeQuery(id+"F0.imprint","IMPRINT",EDGE,{"disambiguationData":[TD([[subQ4,-1.0]])],"derivedFrom":subQ0}),makeQuery(id+"F0.imprint","IMPRINT",EDGE,{"disambiguationData":[TD([[subQ1,-1.0]])],"derivedFrom":subQ0})])],"isStart":true})])]})]});}
            var Q17;
            {var subQ0=sQuery(id+"F0.wireOp",EDGE,"E4.0");var subQ1=makeQuery(id+"F0.imprint","INTERSECT",VERTEX,{"disambiguationData":[OD(0.0)],"derivedFrom":[subQ0,sQuery(id+"F0.wireOp",EDGE,"E6.2.0")]});var subQ2=makeQuery(id+"F0.imprint","INTERSECT",VERTEX,{"disambiguationData":[OD(0.0)],"derivedFrom":[subQ0,sQuery(id+"F0.wireOp",EDGE,"E6.3.0")]});var subQ3=sQuery(id+"F0.wireOp",EDGE,"E6.3.1");var subQ4=makeQuery(id+"F0.imprint","INTERSECT",VERTEX,{"disambiguationData":[OD(0.0)],"derivedFrom":[subQ0,subQ3]});Q17=makeQuery(id+"F5.opFillet","BLEND_EDGE",EDGE,{"blendedFrom":[makeQuery(id+"F1.opExtrude","CAP_EDGE",EDGE,{"disambiguationData":[OSD([subQ3]),TDD([makeQuery(id+"F0.imprint","IMPRINT",EDGE,{"disambiguationData":[TD([[subQ4,-1.0]])],"derivedFrom":subQ3})])],"isStart":false}),makeQuery(id+"F2.opFillet","BLEND_FACE",FACE,{"disambiguationData":[OSD([subQ0]),TDD([makeQuery(id+"F1.opExtrude","CAP_EDGE",EDGE,{"disambiguationData":[OSD([subQ0]),TDD([makeQuery(id+"F0.imprint","IMPRINT",EDGE,{"disambiguationData":[TD([[subQ2,1.0]])],"derivedFrom":subQ0}),makeQuery(id+"F0.imprint","IMPRINT",EDGE,{"disambiguationData":[TD([[subQ2,-1.0]])],"derivedFrom":subQ0}),makeQuery(id+"F0.imprint","IMPRINT",EDGE,{"disambiguationData":[TD([[subQ1,-1.0]])],"derivedFrom":subQ0})])],"isStart":true})])]})],"blendedInto":[makeQuery(id+"F2.opFillet","BLEND_FACE",FACE,{"disambiguationData":[OSD([subQ0]),TDD([makeQuery(id+"F1.opExtrude","CAP_EDGE",EDGE,{"disambiguationData":[OSD([subQ0]),TDD([makeQuery(id+"F0.imprint","IMPRINT",EDGE,{"disambiguationData":[TD([[subQ2,1.0]])],"derivedFrom":subQ0}),makeQuery(id+"F0.imprint","IMPRINT",EDGE,{"disambiguationData":[TD([[subQ2,-1.0]])],"derivedFrom":subQ0}),makeQuery(id+"F0.imprint","IMPRINT",EDGE,{"disambiguationData":[TD([[subQ1,-1.0]])],"derivedFrom":subQ0})])],"isStart":true})])]})]});}
            var Q18;
            {var subQ0=sQuery(id+"F0.wireOp",EDGE,"E4.0");var subQ1=makeQuery(id+"F0.imprint","INTERSECT",VERTEX,{"disambiguationData":[OD(1.0)],"derivedFrom":[subQ0,sQuery(id+"F0.wireOp",EDGE,"E6.3.0")]});var subQ2=makeQuery(id+"F0.imprint","INTERSECT",VERTEX,{"disambiguationData":[OD(1.0)],"derivedFrom":[subQ0,sQuery(id+"F0.wireOp",EDGE,"E6.4.0")]});var subQ3=sQuery(id+"F0.wireOp",EDGE,"E6.4.1");var subQ4=makeQuery(id+"F0.imprint","INTERSECT",VERTEX,{"disambiguationData":[OD(1.0)],"derivedFrom":[subQ0,subQ3]});Q18=makeQuery(id+"F5.opFillet","BLEND_EDGE",EDGE,{"blendedFrom":[makeQuery(id+"F1.opExtrude","CAP_EDGE",EDGE,{"disambiguationData":[OSD([subQ3]),TDD([makeQuery(id+"F0.imprint","IMPRINT",EDGE,{"disambiguationData":[TD([[makeQuery(id+"F0.imprint","INTERSECT",VERTEX,{"disambiguationData":[OD(0.0)],"derivedFrom":[subQ0,subQ3]}),1.0]])],"derivedFrom":subQ3})])],"isStart":false}),makeQuery(id+"F2.opFillet","BLEND_FACE",FACE,{"disambiguationData":[OSD([subQ0]),TDD([makeQuery(id+"F1.opExtrude","CAP_EDGE",EDGE,{"disambiguationData":[OSD([subQ0]),TDD([makeQuery(id+"F0.imprint","IMPRINT",EDGE,{"disambiguationData":[TD([[subQ4,-1.0]])],"derivedFrom":subQ0}),makeQuery(id+"F0.imprint","IMPRINT",EDGE,{"disambiguationData":[TD([[subQ2,-1.0]])],"derivedFrom":subQ0}),makeQuery(id+"F0.imprint","IMPRINT",EDGE,{"disambiguationData":[TD([[subQ1,-1.0]])],"derivedFrom":subQ0})])],"isStart":true})])]})],"blendedInto":[makeQuery(id+"F2.opFillet","BLEND_FACE",FACE,{"disambiguationData":[OSD([subQ0]),TDD([makeQuery(id+"F1.opExtrude","CAP_EDGE",EDGE,{"disambiguationData":[OSD([subQ0]),TDD([makeQuery(id+"F0.imprint","IMPRINT",EDGE,{"disambiguationData":[TD([[subQ4,-1.0]])],"derivedFrom":subQ0}),makeQuery(id+"F0.imprint","IMPRINT",EDGE,{"disambiguationData":[TD([[subQ2,-1.0]])],"derivedFrom":subQ0}),makeQuery(id+"F0.imprint","IMPRINT",EDGE,{"disambiguationData":[TD([[subQ1,-1.0]])],"derivedFrom":subQ0})])],"isStart":true})])]})]});}
            var Q19;
            {var subQ0=sQuery(id+"F0.wireOp",EDGE,"E4.0");var subQ1=makeQuery(id+"F0.imprint","INTERSECT",VERTEX,{"disambiguationData":[OD(0.0)],"derivedFrom":[subQ0,sQuery(id+"F0.wireOp",EDGE,"E6.4.0")]});var subQ2=sQuery(id+"F0.wireOp",EDGE,"E6.4.1");var subQ3=makeQuery(id+"F0.imprint","INTERSECT",VERTEX,{"disambiguationData":[OD(0.0)],"derivedFrom":[subQ0,subQ2]});var subQ4=makeQuery(id+"F0.imprint","INTERSECT",VERTEX,{"disambiguationData":[OD(1.0)],"derivedFrom":[subQ0,sQuery(id+"F0.wireOp",EDGE,"E6.5.0")]});Q19=makeQuery(id+"F5.opFillet","BLEND_EDGE",EDGE,{"blendedFrom":[makeQuery(id+"F1.opExtrude","CAP_EDGE",EDGE,{"disambiguationData":[OSD([subQ2]),TDD([makeQuery(id+"F0.imprint","IMPRINT",EDGE,{"disambiguationData":[TD([[subQ3,1.0]])],"derivedFrom":subQ2})])],"isStart":false}),makeQuery(id+"F2.opFillet","BLEND_FACE",FACE,{"disambiguationData":[OSD([subQ0]),TDD([makeQuery(id+"F1.opExtrude","CAP_EDGE",EDGE,{"disambiguationData":[OSD([subQ0]),TDD([makeQuery(id+"F0.imprint","IMPRINT",EDGE,{"disambiguationData":[TD([[makeQuery(id+"F0.imprint","INTERSECT",VERTEX,{"disambiguationData":[OD(1.0)],"derivedFrom":[subQ0,sQuery(id+"F0.wireOp",EDGE,"E6.5.1")]}),-1.0]])],"derivedFrom":subQ0}),makeQuery(id+"F0.imprint","IMPRINT",EDGE,{"disambiguationData":[TD([[subQ4,-1.0]])],"derivedFrom":subQ0}),makeQuery(id+"F0.imprint","IMPRINT",EDGE,{"disambiguationData":[TD([[subQ1,-1.0]])],"derivedFrom":subQ0})])],"isStart":true})])]})],"blendedInto":[makeQuery(id+"F2.opFillet","BLEND_FACE",FACE,{"disambiguationData":[OSD([subQ0]),TDD([makeQuery(id+"F1.opExtrude","CAP_EDGE",EDGE,{"disambiguationData":[OSD([subQ0]),TDD([makeQuery(id+"F0.imprint","IMPRINT",EDGE,{"disambiguationData":[TD([[makeQuery(id+"F0.imprint","INTERSECT",VERTEX,{"disambiguationData":[OD(1.0)],"derivedFrom":[subQ0,sQuery(id+"F0.wireOp",EDGE,"E6.5.1")]}),-1.0]])],"derivedFrom":subQ0}),makeQuery(id+"F0.imprint","IMPRINT",EDGE,{"disambiguationData":[TD([[subQ4,-1.0]])],"derivedFrom":subQ0}),makeQuery(id+"F0.imprint","IMPRINT",EDGE,{"disambiguationData":[TD([[subQ1,-1.0]])],"derivedFrom":subQ0})])],"isStart":true})])]})]});}
            var Q20;
            {var subQ0=sQuery(id+"F0.wireOp",EDGE,"E4.0");var subQ1=makeQuery(id+"F0.imprint","INTERSECT",VERTEX,{"disambiguationData":[OD(0.0)],"derivedFrom":[subQ0,sQuery(id+"F0.wireOp",EDGE,"E6.4.0")]});var subQ2=makeQuery(id+"F0.imprint","INTERSECT",VERTEX,{"disambiguationData":[OD(1.0)],"derivedFrom":[subQ0,sQuery(id+"F0.wireOp",EDGE,"E6.5.0")]});var subQ3=sQuery(id+"F0.wireOp",EDGE,"E6.5.1");var subQ4=makeQuery(id+"F0.imprint","INTERSECT",VERTEX,{"disambiguationData":[OD(1.0)],"derivedFrom":[subQ0,subQ3]});Q20=makeQuery(id+"F5.opFillet","BLEND_EDGE",EDGE,{"blendedFrom":[makeQuery(id+"F1.opExtrude","CAP_EDGE",EDGE,{"disambiguationData":[OSD([subQ3]),TDD([makeQuery(id+"F0.imprint","IMPRINT",EDGE,{"disambiguationData":[TD([[makeQuery(id+"F0.imprint","INTERSECT",VERTEX,{"disambiguationData":[OD(0.0)],"derivedFrom":[subQ0,subQ3]}),1.0]])],"derivedFrom":subQ3})])],"isStart":false}),makeQuery(id+"F2.opFillet","BLEND_FACE",FACE,{"disambiguationData":[OSD([subQ0]),TDD([makeQuery(id+"F1.opExtrude","CAP_EDGE",EDGE,{"disambiguationData":[OSD([subQ0]),TDD([makeQuery(id+"F0.imprint","IMPRINT",EDGE,{"disambiguationData":[TD([[subQ4,-1.0]])],"derivedFrom":subQ0}),makeQuery(id+"F0.imprint","IMPRINT",EDGE,{"disambiguationData":[TD([[subQ2,-1.0]])],"derivedFrom":subQ0}),makeQuery(id+"F0.imprint","IMPRINT",EDGE,{"disambiguationData":[TD([[subQ1,-1.0]])],"derivedFrom":subQ0})])],"isStart":true})])]})],"blendedInto":[makeQuery(id+"F2.opFillet","BLEND_FACE",FACE,{"disambiguationData":[OSD([subQ0]),TDD([makeQuery(id+"F1.opExtrude","CAP_EDGE",EDGE,{"disambiguationData":[OSD([subQ0]),TDD([makeQuery(id+"F0.imprint","IMPRINT",EDGE,{"disambiguationData":[TD([[subQ4,-1.0]])],"derivedFrom":subQ0}),makeQuery(id+"F0.imprint","IMPRINT",EDGE,{"disambiguationData":[TD([[subQ2,-1.0]])],"derivedFrom":subQ0}),makeQuery(id+"F0.imprint","IMPRINT",EDGE,{"disambiguationData":[TD([[subQ1,-1.0]])],"derivedFrom":subQ0})])],"isStart":true})])]})]});}
            var Q21;
            {var subQ0=sQuery(id+"F0.wireOp",EDGE,"E4.0");var subQ1=makeQuery(id+"F0.imprint","INTERSECT",VERTEX,{"disambiguationData":[OD(0.0)],"derivedFrom":[subQ0,sQuery(id+"F0.wireOp",EDGE,"E6.5.0")]});var subQ2=sQuery(id+"F0.wireOp",EDGE,"E6.5.1");var subQ3=makeQuery(id+"F0.imprint","INTERSECT",VERTEX,{"disambiguationData":[OD(0.0)],"derivedFrom":[subQ0,subQ2]});var subQ4=makeQuery(id+"F0.imprint","INTERSECT",VERTEX,{"disambiguationData":[OD(1.0)],"derivedFrom":[subQ0,sQuery(id+"F0.wireOp",EDGE,"E6.6.0")]});Q21=makeQuery(id+"F5.opFillet","BLEND_EDGE",EDGE,{"blendedFrom":[makeQuery(id+"F1.opExtrude","CAP_EDGE",EDGE,{"disambiguationData":[OSD([subQ2]),TDD([makeQuery(id+"F0.imprint","IMPRINT",EDGE,{"disambiguationData":[TD([[subQ3,1.0]])],"derivedFrom":subQ2})])],"isStart":false}),makeQuery(id+"F2.opFillet","BLEND_FACE",FACE,{"disambiguationData":[OSD([subQ0]),TDD([makeQuery(id+"F1.opExtrude","CAP_EDGE",EDGE,{"disambiguationData":[OSD([subQ0]),TDD([makeQuery(id+"F0.imprint","IMPRINT",EDGE,{"disambiguationData":[TD([[makeQuery(id+"F0.imprint","INTERSECT",VERTEX,{"disambiguationData":[OD(1.0)],"derivedFrom":[subQ0,sQuery(id+"F0.wireOp",EDGE,"E6.6.1")]}),-1.0]])],"derivedFrom":subQ0}),makeQuery(id+"F0.imprint","IMPRINT",EDGE,{"disambiguationData":[TD([[subQ4,-1.0]])],"derivedFrom":subQ0}),makeQuery(id+"F0.imprint","IMPRINT",EDGE,{"disambiguationData":[TD([[subQ1,-1.0]])],"derivedFrom":subQ0})])],"isStart":true})])]})],"blendedInto":[makeQuery(id+"F2.opFillet","BLEND_FACE",FACE,{"disambiguationData":[OSD([subQ0]),TDD([makeQuery(id+"F1.opExtrude","CAP_EDGE",EDGE,{"disambiguationData":[OSD([subQ0]),TDD([makeQuery(id+"F0.imprint","IMPRINT",EDGE,{"disambiguationData":[TD([[makeQuery(id+"F0.imprint","INTERSECT",VERTEX,{"disambiguationData":[OD(1.0)],"derivedFrom":[subQ0,sQuery(id+"F0.wireOp",EDGE,"E6.6.1")]}),-1.0]])],"derivedFrom":subQ0}),makeQuery(id+"F0.imprint","IMPRINT",EDGE,{"disambiguationData":[TD([[subQ4,-1.0]])],"derivedFrom":subQ0}),makeQuery(id+"F0.imprint","IMPRINT",EDGE,{"disambiguationData":[TD([[subQ1,-1.0]])],"derivedFrom":subQ0})])],"isStart":true})])]})]});}
            var Q22;
            {var subQ0=sQuery(id+"F0.wireOp",EDGE,"E4.0");var subQ1=makeQuery(id+"F0.imprint","INTERSECT",VERTEX,{"disambiguationData":[OD(0.0)],"derivedFrom":[subQ0,sQuery(id+"F0.wireOp",EDGE,"E6.8.0")]});var subQ2=makeQuery(id+"F0.imprint","INTERSECT",VERTEX,{"disambiguationData":[OD(1.0)],"derivedFrom":[subQ0,sQuery(id+"F0.wireOp",EDGE,"E6.9.0")]});var subQ3=sQuery(id+"F0.wireOp",EDGE,"E6.9.1");var subQ4=makeQuery(id+"F0.imprint","INTERSECT",VERTEX,{"disambiguationData":[OD(1.0)],"derivedFrom":[subQ0,subQ3]});Q22=makeQuery(id+"F5.opFillet","BLEND_EDGE",EDGE,{"blendedFrom":[makeQuery(id+"F1.opExtrude","CAP_EDGE",EDGE,{"disambiguationData":[OSD([subQ3]),TDD([makeQuery(id+"F0.imprint","IMPRINT",EDGE,{"disambiguationData":[TD([[makeQuery(id+"F0.imprint","INTERSECT",VERTEX,{"disambiguationData":[OD(0.0)],"derivedFrom":[subQ0,subQ3]}),1.0]])],"derivedFrom":subQ3})])],"isStart":false}),makeQuery(id+"F2.opFillet","BLEND_FACE",FACE,{"disambiguationData":[OSD([subQ0]),TDD([makeQuery(id+"F1.opExtrude","CAP_EDGE",EDGE,{"disambiguationData":[OSD([subQ0]),TDD([makeQuery(id+"F0.imprint","IMPRINT",EDGE,{"disambiguationData":[TD([[subQ4,-1.0]])],"derivedFrom":subQ0}),makeQuery(id+"F0.imprint","IMPRINT",EDGE,{"disambiguationData":[TD([[subQ2,-1.0]])],"derivedFrom":subQ0}),makeQuery(id+"F0.imprint","IMPRINT",EDGE,{"disambiguationData":[TD([[subQ1,-1.0]])],"derivedFrom":subQ0})])],"isStart":true})])]})],"blendedInto":[makeQuery(id+"F2.opFillet","BLEND_FACE",FACE,{"disambiguationData":[OSD([subQ0]),TDD([makeQuery(id+"F1.opExtrude","CAP_EDGE",EDGE,{"disambiguationData":[OSD([subQ0]),TDD([makeQuery(id+"F0.imprint","IMPRINT",EDGE,{"disambiguationData":[TD([[subQ4,-1.0]])],"derivedFrom":subQ0}),makeQuery(id+"F0.imprint","IMPRINT",EDGE,{"disambiguationData":[TD([[subQ2,-1.0]])],"derivedFrom":subQ0}),makeQuery(id+"F0.imprint","IMPRINT",EDGE,{"disambiguationData":[TD([[subQ1,-1.0]])],"derivedFrom":subQ0})])],"isStart":true})])]})]});}
            var Q23;
            {var subQ0=sQuery(id+"F0.wireOp",EDGE,"E4.0");var subQ1=makeQuery(id+"F0.imprint","INTERSECT",VERTEX,{"disambiguationData":[OD(0.0)],"derivedFrom":[subQ0,sQuery(id+"F0.wireOp",EDGE,"E6.6.0")]});var subQ2=sQuery(id+"F0.wireOp",EDGE,"E6.6.1");var subQ3=makeQuery(id+"F0.imprint","INTERSECT",VERTEX,{"disambiguationData":[OD(0.0)],"derivedFrom":[subQ0,subQ2]});var subQ4=makeQuery(id+"F0.imprint","INTERSECT",VERTEX,{"disambiguationData":[OD(1.0)],"derivedFrom":[subQ0,sQuery(id+"F0.wireOp",EDGE,"E6.7.0")]});Q23=makeQuery(id+"F5.opFillet","BLEND_EDGE",EDGE,{"blendedFrom":[makeQuery(id+"F1.opExtrude","CAP_EDGE",EDGE,{"disambiguationData":[OSD([subQ2]),TDD([makeQuery(id+"F0.imprint","IMPRINT",EDGE,{"disambiguationData":[TD([[subQ3,1.0]])],"derivedFrom":subQ2})])],"isStart":false}),makeQuery(id+"F2.opFillet","BLEND_FACE",FACE,{"disambiguationData":[OSD([subQ0]),TDD([makeQuery(id+"F1.opExtrude","CAP_EDGE",EDGE,{"disambiguationData":[OSD([subQ0]),TDD([makeQuery(id+"F0.imprint","IMPRINT",EDGE,{"disambiguationData":[TD([[makeQuery(id+"F0.imprint","INTERSECT",VERTEX,{"disambiguationData":[OD(1.0)],"derivedFrom":[subQ0,sQuery(id+"F0.wireOp",EDGE,"E6.7.1")]}),-1.0]])],"derivedFrom":subQ0}),makeQuery(id+"F0.imprint","IMPRINT",EDGE,{"disambiguationData":[TD([[subQ4,-1.0]])],"derivedFrom":subQ0}),makeQuery(id+"F0.imprint","IMPRINT",EDGE,{"disambiguationData":[TD([[subQ1,-1.0]])],"derivedFrom":subQ0})])],"isStart":true})])]})],"blendedInto":[makeQuery(id+"F2.opFillet","BLEND_FACE",FACE,{"disambiguationData":[OSD([subQ0]),TDD([makeQuery(id+"F1.opExtrude","CAP_EDGE",EDGE,{"disambiguationData":[OSD([subQ0]),TDD([makeQuery(id+"F0.imprint","IMPRINT",EDGE,{"disambiguationData":[TD([[makeQuery(id+"F0.imprint","INTERSECT",VERTEX,{"disambiguationData":[OD(1.0)],"derivedFrom":[subQ0,sQuery(id+"F0.wireOp",EDGE,"E6.7.1")]}),-1.0]])],"derivedFrom":subQ0}),makeQuery(id+"F0.imprint","IMPRINT",EDGE,{"disambiguationData":[TD([[subQ4,-1.0]])],"derivedFrom":subQ0}),makeQuery(id+"F0.imprint","IMPRINT",EDGE,{"disambiguationData":[TD([[subQ1,-1.0]])],"derivedFrom":subQ0})])],"isStart":true})])]})]});}
            fillet(context, id + "F6", {"entities" : qUnion([Q0, Q1, Q2, Q3, Q4, Q5, Q6, Q7, Q8, Q9, Q10, Q11, Q12, Q13, Q14, Q15, Q16, Q17, Q18, Q19, Q20, Q21, Q22, Q23]), "radius" : 3 * mm, "tangentPropagation" : true, "allowEdgeOverflow" : false});
        }
    });
